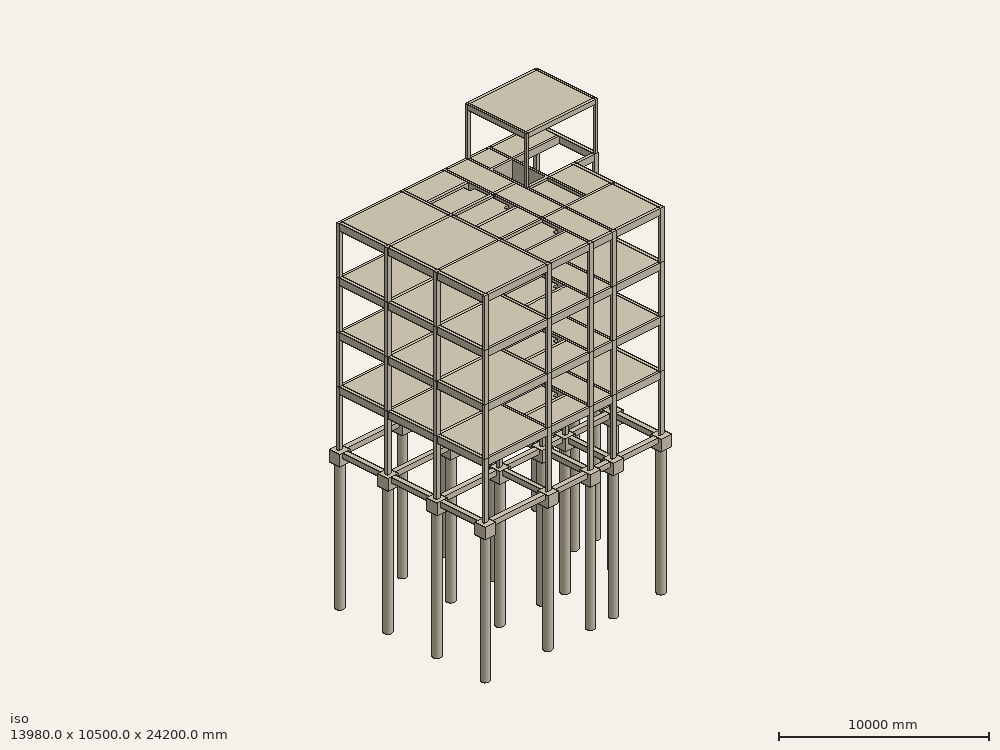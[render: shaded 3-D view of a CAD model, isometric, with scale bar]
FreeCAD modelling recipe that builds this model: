
FCSTD DOCUMENT  (FreeCAD 0.19R23074 (Git))
Label: 2020-12-18 Piloto estructural
License: All rights reserved
objects: Part::FeaturePython×393, Part::Part2DObjectPython×35, App::GeometryPython×28, App::FeaturePython×3, App::DocumentObjectGroup×2, TechDraw::DrawSVGTemplate×2, TechDraw::DrawViewArch×2, TechDraw::DrawPage×2, Spreadsheet::Sheet×1
note: 459 computed .brp shape members not serialized (recipe doc carries the construction recipe); baked Part::Feature solids carry a one-line shape summary decoded from their .brp

FEATURE [Part::FeaturePython] Axis  label="Vertical"  # WARN: FeaturePython — macro-defined, semantics opaque (R4)
  Angles = [0,0,0,0,0,0,0]
  Distances = [1930,4230,2850,1550,1450,1770,1430]
  Length = 12000
  Placement = pos=(0,-1350,0) rot=(0,0,1;0rad)
FEATURE [Part::FeaturePython] Axis002  label="HorizontaL"  # WARN: FeaturePython — macro-defined, semantics opaque (R4)
  Angles = [0,0,0,0,0,0]
  Distances = [100,3250,2620,670,1730,1530]
  Length = 32000
  Placement = pos=(31000,1.077e-12,0) rot=(0,0,1;1.5708rad)
FEATURE [App::DocumentObjectGroup] Group  label="Rejillas"
  Group = -> [Axis002,Axis]
FEATURE [TechDraw::DrawSVGTemplate] Template004
  Height = 841
  Orientation = 1
  Width = 1189
FEATURE [Part::Part2DObjectPython] Rectangle001  label="Lote"  # Draft 2D object (typed FeaturePython)
  Area = 0
  ChamferSize = 0
  Columns = 1
  FilletRadius = 0
  Height = 10000
  Length = 30000
  MakeFace = false
  Rows = 1
FEATURE [TechDraw::DrawSVGTemplate] Template005
  Height = 841
  Orientation = 1
  Width = 1189
FEATURE [Part::Part2DObjectPython] Rectangle002  # Draft 2D object (typed FeaturePython)
  Area = 0
  ChamferSize = 0
  Columns = 1
  FilletRadius = 0
  Height = 700
  Length = 700
  MakeFace = false
  Placement = pos=(14860,9550,0) rot=(0,0,1;0rad)
  Rows = 1
  expr: Height = <<Estructura>>.CabAncho
  expr: Length = <<Estructura>>.CabAncho
FEATURE [Part::Part2DObjectPython] Circle  # Draft 2D object (typed FeaturePython)
  Area = 0
  FirstAngle = 0
  LastAngle = 0
  MakeFace = false
  Placement = pos=(15210,9900,0) rot=(0,0,1;0rad)
  Radius = 250
  expr: Radius = <<Estructura>>.PilRad
FEATURE [Part::FeaturePython] Structure  label="CAB PIL 1"  # Arch/BIM 77 (typed FeaturePython)
  Base = -> Rectangle002
  Description = Pilote rectangular
  FaceMaker = 0
  Height = 700
  HorizontalArea = 490000
  IfcData = attributes={"GlobalId": {"name": "GlobalId", "type": "IfcGloballyUniqueId", "is_enum": false, "enum_values": []}, "Description": {"... (+532 chars omitted),+1 more (map truncated)
  IfcType = 77
  Length = 0
  MoveBase = false
  MoveWithHost = false
  Nodes = (2) [(15210,9900,0),(15210,9900,-700)]
  NodesOffset = 0
  Normal = (0,0,-1)
  PerimeterLength = 2800
  Placement = pos=(-13280,1.819e-12,-500) rot=(0,0,1;0rad)
  PredefinedType = 3
  VerticalArea = 1960000
  Width = 0
  expr: Height = <<Estructura>>.CabEsp
FEATURE [Part::FeaturePython] Structure001  label="PIL 1"  # Arch/BIM 96 (typed FeaturePython)
  Base = -> Circle
  ConstructionType = 0
  Description = Pilote circular
  FaceMaker = 0
  Height = 8000
  HorizontalArea = 196350
  IfcData = attributes={"GlobalId": {"name": "GlobalId", "type": "IfcGloballyUniqueId", "is_enum": false, "enum_values": []}, "Description": {"... (+752 chars omitted),+1 more (map truncated)
  IfcType = 96
  Length = 0
  MoveBase = false
  MoveWithHost = false
  Nodes = (2) [(15210,9900,0),(15210,9900,-8000)]
  NodesOffset = 0
  Normal = (0,0,-1)
  PerimeterLength = 1570.8
  Placement = pos=(-13280,1.819e-12,-1200) rot=(0,0,1;0rad)
  PredefinedType = 5
  VerticalArea = 1.25664e+07
  Width = 100
  expr: Height = <<Estructura>>.PilProf
FEATURE [Part::FeaturePython] Structure002  label="CAB PIL 6"  # Arch/BIM 172 (typed FeaturePython)
  CloneOf = -> Structure
  FaceMaker = 0
  Height = 700
  HorizontalArea = 490000
  IfcData = attributes={"GlobalId": {"name": "GlobalId", "type": "IfcGloballyUniqueId", "is_enum": false, "enum_values": []}, "Description": {"... (+484 chars omitted),+1 more (map truncated)
  IfcType = 172
  Length = 0
  MoveBase = false
  MoveWithHost = false
  Nodes = (2) [(15210,9900,0),(15210,9900,-700)]
  NodesOffset = 0
  Normal = (0,0,0)
  PerimeterLength = 2800
  Placement = pos=(-13280,-3260,-500) rot=(0,0,1;0rad)
  PredefinedType = 0
  VerticalArea = 1960000
  Width = 0
FEATURE [Part::FeaturePython] Structure003  label="PIL 6"  # Arch/BIM 172 (typed FeaturePython)
  CloneOf = -> Structure001
  FaceMaker = 0
  Height = 8000
  HorizontalArea = 196350
  IfcData = attributes={"GlobalId": {"name": "GlobalId", "type": "IfcGloballyUniqueId", "is_enum": false, "enum_values": []}, "Description": {"... (+484 chars omitted),+1 more (map truncated)
  IfcType = 172
  Length = 0
  MoveBase = false
  MoveWithHost = false
  Nodes = (2) [(15210,9900,0),(15210,9900,-8000)]
  NodesOffset = 0
  Normal = (0,0,0)
  PerimeterLength = 1570.8
  Placement = pos=(-13280,-3260,-1200) rot=(0,0,1;0rad)
  PredefinedType = 0
  VerticalArea = 1.25664e+07
  Width = 100
FEATURE [Part::FeaturePython] Structure004  label="CAB PIL 11"  # Arch/BIM 172 (typed FeaturePython)
  CloneOf = -> Structure
  FaceMaker = 0
  Height = 700
  HorizontalArea = 490000
  IfcData = attributes={"GlobalId": {"name": "GlobalId", "type": "IfcGloballyUniqueId", "is_enum": false, "enum_values": []}, "Description": {"... (+484 chars omitted),+1 more (map truncated)
  IfcType = 172
  Length = 0
  MoveBase = false
  MoveWithHost = false
  Nodes = (2) [(15210,9900,0),(15210,9900,-700)]
  NodesOffset = 0
  Normal = (0,0,0)
  PerimeterLength = 2800
  Placement = pos=(-13280,-6550,-500) rot=(0,0,1;0rad)
  PredefinedType = 0
  VerticalArea = 1960000
  Width = 0
FEATURE [Part::FeaturePython] Structure005  label="PIL 11"  # Arch/BIM 172 (typed FeaturePython)
  CloneOf = -> Structure001
  FaceMaker = 0
  Height = 8000
  HorizontalArea = 196350
  IfcData = attributes={"GlobalId": {"name": "GlobalId", "type": "IfcGloballyUniqueId", "is_enum": false, "enum_values": []}, "Description": {"... (+484 chars omitted),+1 more (map truncated)
  IfcType = 172
  Length = 0
  MoveBase = false
  MoveWithHost = false
  Nodes = (2) [(15210,9900,0),(15210,9900,-8000)]
  NodesOffset = 0
  Normal = (0,0,0)
  PerimeterLength = 1570.8
  Placement = pos=(-13280,-6550,-1200) rot=(0,0,1;0rad)
  PredefinedType = 0
  VerticalArea = 1.25664e+07
  Width = 100
FEATURE [Part::FeaturePython] Structure006  label="CAB PIL 2"  # Arch/BIM 172 (typed FeaturePython)
  CloneOf = -> Structure
  FaceMaker = 0
  Height = 700
  HorizontalArea = 490000
  IfcData = attributes={"GlobalId": {"name": "GlobalId", "type": "IfcGloballyUniqueId", "is_enum": false, "enum_values": []}, "Description": {"... (+484 chars omitted),+1 more (map truncated)
  IfcType = 172
  Length = 0
  MoveBase = false
  MoveWithHost = false
  Nodes = (2) [(15210,9900,0),(15210,9900,-700)]
  NodesOffset = 0
  Normal = (0,0,0)
  PerimeterLength = 2800
  Placement = pos=(-9050,0,-500) rot=(0,0,1;0rad)
  PredefinedType = 0
  VerticalArea = 1960000
  Width = 0
FEATURE [Part::FeaturePython] Structure007  label="PIL 2"  # Arch/BIM 172 (typed FeaturePython)
  CloneOf = -> Structure001
  FaceMaker = 0
  Height = 8000
  HorizontalArea = 196350
  IfcData = attributes={"GlobalId": {"name": "GlobalId", "type": "IfcGloballyUniqueId", "is_enum": false, "enum_values": []}, "Description": {"... (+484 chars omitted),+1 more (map truncated)
  IfcType = 172
  Length = 0
  MoveBase = false
  MoveWithHost = false
  Nodes = (2) [(15210,9900,0),(15210,9900,-8000)]
  NodesOffset = 0
  Normal = (0,0,0)
  PerimeterLength = 1570.8
  Placement = pos=(-9050,0,-1200) rot=(0,0,1;0rad)
  PredefinedType = 0
  VerticalArea = 1.25664e+07
  Width = 100
FEATURE [Part::FeaturePython] Structure008  label="CAB PIL 3"  # Arch/BIM 172 (typed FeaturePython)
  CloneOf = -> Structure
  FaceMaker = 0
  Height = 700
  HorizontalArea = 490000
  IfcData = attributes={"GlobalId": {"name": "GlobalId", "type": "IfcGloballyUniqueId", "is_enum": false, "enum_values": []}, "Description": {"... (+484 chars omitted),+1 more (map truncated)
  IfcType = 172
  Length = 0
  MoveBase = false
  MoveWithHost = false
  Nodes = (2) [(15210,9900,0),(15210,9900,-700)]
  NodesOffset = 0
  Normal = (0,0,0)
  PerimeterLength = 2800
  Placement = pos=(-6200,0,-500) rot=(0,0,1;0rad)
  PredefinedType = 0
  VerticalArea = 1960000
  Width = 0
FEATURE [Part::FeaturePython] Structure009  label="PIL 3"  # Arch/BIM 172 (typed FeaturePython)
  CloneOf = -> Structure001
  FaceMaker = 0
  Height = 8000
  HorizontalArea = 196350
  IfcData = attributes={"GlobalId": {"name": "GlobalId", "type": "IfcGloballyUniqueId", "is_enum": false, "enum_values": []}, "Description": {"... (+484 chars omitted),+1 more (map truncated)
  IfcType = 172
  Length = 0
  MoveBase = false
  MoveWithHost = false
  Nodes = (2) [(15210,9900,0),(15210,9900,-8000)]
  NodesOffset = 0
  Normal = (0,0,0)
  PerimeterLength = 1570.8
  Placement = pos=(-6200,0,-1200) rot=(0,0,1;0rad)
  PredefinedType = 0
  VerticalArea = 1.25664e+07
  Width = 100
FEATURE [Part::FeaturePython] Structure010  label="CAB PIL 4"  # Arch/BIM 172 (typed FeaturePython)
  CloneOf = -> Structure
  FaceMaker = 0
  Height = 700
  HorizontalArea = 490000
  IfcData = attributes={"GlobalId": {"name": "GlobalId", "type": "IfcGloballyUniqueId", "is_enum": false, "enum_values": []}, "Description": {"... (+484 chars omitted),+1 more (map truncated)
  IfcType = 172
  Length = 0
  MoveBase = false
  MoveWithHost = false
  Nodes = (2) [(15210,9900,0),(15210,9900,-700)]
  NodesOffset = 0
  Normal = (0,0,0)
  PerimeterLength = 2800
  Placement = pos=(-3200,0,-500) rot=(0,0,1;0rad)
  PredefinedType = 0
  VerticalArea = 1960000
  Width = 0
FEATURE [Part::FeaturePython] Structure011  label="PIL 4"  # Arch/BIM 172 (typed FeaturePython)
  CloneOf = -> Structure001
  FaceMaker = 0
  Height = 8000
  HorizontalArea = 196350
  IfcData = attributes={"GlobalId": {"name": "GlobalId", "type": "IfcGloballyUniqueId", "is_enum": false, "enum_values": []}, "Description": {"... (+484 chars omitted),+1 more (map truncated)
  IfcType = 172
  Length = 0
  MoveBase = false
  MoveWithHost = false
  Nodes = (2) [(15210,9900,0),(15210,9900,-8000)]
  NodesOffset = 0
  Normal = (0,0,0)
  PerimeterLength = 1570.8
  Placement = pos=(-3200,0,-1200) rot=(0,0,1;0rad)
  PredefinedType = 0
  VerticalArea = 1.25664e+07
  Width = 100
FEATURE [Part::FeaturePython] Structure012  label="CAB PIL 5"  # Arch/BIM 172 (typed FeaturePython)
  CloneOf = -> Structure
  FaceMaker = 0
  Height = 700
  HorizontalArea = 490000
  IfcData = attributes={"GlobalId": {"name": "GlobalId", "type": "IfcGloballyUniqueId", "is_enum": false, "enum_values": []}, "Description": {"... (+484 chars omitted),+1 more (map truncated)
  IfcType = 172
  Length = 0
  MoveBase = false
  MoveWithHost = false
  Nodes = (2) [(15210,9900,0),(15210,9900,-700)]
  NodesOffset = 0
  Normal = (0,0,0)
  PerimeterLength = 2800
  Placement = pos=(-9.09e-13,0,-500) rot=(0,0,1;0rad)
  PredefinedType = 0
  VerticalArea = 1960000
  Width = 0
FEATURE [Part::FeaturePython] Structure013  label="PIL 5"  # Arch/BIM 172 (typed FeaturePython)
  CloneOf = -> Structure001
  FaceMaker = 0
  Height = 8000
  HorizontalArea = 196350
  IfcData = attributes={"GlobalId": {"name": "GlobalId", "type": "IfcGloballyUniqueId", "is_enum": false, "enum_values": []}, "Description": {"... (+484 chars omitted),+1 more (map truncated)
  IfcType = 172
  Length = 0
  MoveBase = false
  MoveWithHost = false
  Nodes = (2) [(15210,9900,0),(15210,9900,-8000)]
  NodesOffset = 0
  Normal = (0,0,0)
  PerimeterLength = 1570.8
  Placement = pos=(-9.09e-13,0,-1200) rot=(0,0,1;0rad)
  PredefinedType = 0
  VerticalArea = 1.25664e+07
  Width = 100
FEATURE [Part::FeaturePython] Structure014  label="CAB PIL 7"  # Arch/BIM 172 (typed FeaturePython)
  CloneOf = -> Structure
  FaceMaker = 0
  Height = 700
  HorizontalArea = 490000
  IfcData = attributes={"GlobalId": {"name": "GlobalId", "type": "IfcGloballyUniqueId", "is_enum": false, "enum_values": []}, "Description": {"... (+484 chars omitted),+1 more (map truncated)
  IfcType = 172
  Length = 0
  MoveBase = false
  MoveWithHost = false
  Nodes = (2) [(15210,9900,0),(15210,9900,-700)]
  NodesOffset = 0
  Normal = (0,0,0)
  PerimeterLength = 2800
  Placement = pos=(-9050,-3260,-500) rot=(0,0,1;0rad)
  PredefinedType = 0
  VerticalArea = 1960000
  Width = 0
FEATURE [Part::FeaturePython] Structure015  label="PIL 7"  # Arch/BIM 172 (typed FeaturePython)
  CloneOf = -> Structure001
  FaceMaker = 0
  Height = 8000
  HorizontalArea = 196350
  IfcData = attributes={"GlobalId": {"name": "GlobalId", "type": "IfcGloballyUniqueId", "is_enum": false, "enum_values": []}, "Description": {"... (+484 chars omitted),+1 more (map truncated)
  IfcType = 172
  Length = 0
  MoveBase = false
  MoveWithHost = false
  Nodes = (2) [(15210,9900,0),(15210,9900,-8000)]
  NodesOffset = 0
  Normal = (0,0,0)
  PerimeterLength = 1570.8
  Placement = pos=(-9050,-3260,-1200) rot=(0,0,1;0rad)
  PredefinedType = 0
  VerticalArea = 1.25664e+07
  Width = 100
FEATURE [Part::FeaturePython] Structure016  label="CAB PIL 8"  # Arch/BIM 172 (typed FeaturePython)
  CloneOf = -> Structure
  FaceMaker = 0
  Height = 700
  HorizontalArea = 490000
  IfcData = attributes={"GlobalId": {"name": "GlobalId", "type": "IfcGloballyUniqueId", "is_enum": false, "enum_values": []}, "Description": {"... (+484 chars omitted),+1 more (map truncated)
  IfcType = 172
  Length = 0
  MoveBase = false
  MoveWithHost = false
  Nodes = (2) [(15210,9900,0),(15210,9900,-700)]
  NodesOffset = 0
  Normal = (0,0,0)
  PerimeterLength = 2800
  Placement = pos=(-6200,-3260,-500) rot=(0,0,1;0rad)
  PredefinedType = 0
  VerticalArea = 1960000
  Width = 0
FEATURE [Part::FeaturePython] Structure017  label="PIL 8"  # Arch/BIM 172 (typed FeaturePython)
  CloneOf = -> Structure001
  FaceMaker = 0
  Height = 8000
  HorizontalArea = 196350
  IfcData = attributes={"GlobalId": {"name": "GlobalId", "type": "IfcGloballyUniqueId", "is_enum": false, "enum_values": []}, "Description": {"... (+484 chars omitted),+1 more (map truncated)
  IfcType = 172
  Length = 0
  MoveBase = false
  MoveWithHost = false
  Nodes = (2) [(15210,9900,0),(15210,9900,-8000)]
  NodesOffset = 0
  Normal = (0,0,0)
  PerimeterLength = 1570.8
  Placement = pos=(-6200,-3260,-1200) rot=(0,0,1;0rad)
  PredefinedType = 0
  VerticalArea = 1.25664e+07
  Width = 100
FEATURE [Part::FeaturePython] Structure018  label="CAB PIL 9"  # Arch/BIM 172 (typed FeaturePython)
  CloneOf = -> Structure
  FaceMaker = 0
  Height = 700
  HorizontalArea = 490000
  IfcData = attributes={"GlobalId": {"name": "GlobalId", "type": "IfcGloballyUniqueId", "is_enum": false, "enum_values": []}, "Description": {"... (+484 chars omitted),+1 more (map truncated)
  IfcType = 172
  Length = 0
  MoveBase = false
  MoveWithHost = false
  Nodes = (2) [(15210,9900,0),(15210,9900,-700)]
  NodesOffset = 0
  Normal = (0,0,0)
  PerimeterLength = 2800
  Placement = pos=(-1430,-3930,-500) rot=(0,0,1;0rad)
  PredefinedType = 0
  VerticalArea = 1960000
  Width = 0
FEATURE [Part::FeaturePython] Structure019  label="PIL 9"  # Arch/BIM 172 (typed FeaturePython)
  CloneOf = -> Structure001
  FaceMaker = 0
  Height = 8000
  HorizontalArea = 196350
  IfcData = attributes={"GlobalId": {"name": "GlobalId", "type": "IfcGloballyUniqueId", "is_enum": false, "enum_values": []}, "Description": {"... (+484 chars omitted),+1 more (map truncated)
  IfcType = 172
  Length = 0
  MoveBase = false
  MoveWithHost = false
  Nodes = (2) [(15210,9900,0),(15210,9900,-8000)]
  NodesOffset = 0
  Normal = (0,0,0)
  PerimeterLength = 1570.8
  Placement = pos=(-1430,-3930,-1200) rot=(0,0,1;0rad)
  PredefinedType = 0
  VerticalArea = 1.25664e+07
  Width = 100
FEATURE [Part::FeaturePython] Structure020  label="CAB PIL 10"  # Arch/BIM 172 (typed FeaturePython)
  CloneOf = -> Structure
  FaceMaker = 0
  Height = 700
  HorizontalArea = 490000
  IfcData = attributes={"GlobalId": {"name": "GlobalId", "type": "IfcGloballyUniqueId", "is_enum": false, "enum_values": []}, "Description": {"... (+484 chars omitted),+1 more (map truncated)
  IfcType = 172
  Length = 0
  MoveBase = false
  MoveWithHost = false
  Nodes = (2) [(15210,9900,0),(15210,9900,-700)]
  NodesOffset = 0
  Normal = (0,0,0)
  PerimeterLength = 2800
  Placement = pos=(-9.09e-13,-3930,-500) rot=(0,0,1;0rad)
  PredefinedType = 0
  VerticalArea = 1960000
  Width = 0
FEATURE [Part::FeaturePython] Structure021  label="PIL 10"  # Arch/BIM 172 (typed FeaturePython)
  CloneOf = -> Structure001
  FaceMaker = 0
  Height = 8000
  HorizontalArea = 196350
  IfcData = attributes={"GlobalId": {"name": "GlobalId", "type": "IfcGloballyUniqueId", "is_enum": false, "enum_values": []}, "Description": {"... (+484 chars omitted),+1 more (map truncated)
  IfcType = 172
  Length = 0
  MoveBase = false
  MoveWithHost = false
  Nodes = (2) [(15210,9900,0),(15210,9900,-8000)]
  NodesOffset = 0
  Normal = (0,0,0)
  PerimeterLength = 1570.8
  Placement = pos=(-9.09e-13,-3930,-1200) rot=(0,0,1;0rad)
  PredefinedType = 0
  VerticalArea = 1.25664e+07
  Width = 100
FEATURE [Part::FeaturePython] Structure022  label="CAB PIL 12"  # Arch/BIM 172 (typed FeaturePython)
  CloneOf = -> Structure
  FaceMaker = 0
  Height = 700
  HorizontalArea = 490000
  IfcData = attributes={"GlobalId": {"name": "GlobalId", "type": "IfcGloballyUniqueId", "is_enum": false, "enum_values": []}, "Description": {"... (+484 chars omitted),+1 more (map truncated)
  IfcType = 172
  Length = 0
  MoveBase = false
  MoveWithHost = false
  Nodes = (2) [(15210,9900,0),(15210,9900,-700)]
  NodesOffset = 0
  Normal = (0,0,0)
  PerimeterLength = 2800
  Placement = pos=(-9050,-6550,-500) rot=(0,0,1;0rad)
  PredefinedType = 0
  VerticalArea = 1960000
  Width = 0
FEATURE [Part::FeaturePython] Structure023  label="PIL 12"  # Arch/BIM 172 (typed FeaturePython)
  CloneOf = -> Structure001
  FaceMaker = 0
  Height = 8000
  HorizontalArea = 196350
  IfcData = attributes={"GlobalId": {"name": "GlobalId", "type": "IfcGloballyUniqueId", "is_enum": false, "enum_values": []}, "Description": {"... (+484 chars omitted),+1 more (map truncated)
  IfcType = 172
  Length = 0
  MoveBase = false
  MoveWithHost = false
  Nodes = (2) [(15210,9900,0),(15210,9900,-8000)]
  NodesOffset = 0
  Normal = (0,0,0)
  PerimeterLength = 1570.8
  Placement = pos=(-9050,-6550,-1200) rot=(0,0,1;0rad)
  PredefinedType = 0
  VerticalArea = 1.25664e+07
  Width = 100
FEATURE [Part::FeaturePython] Structure024  label="CAB PIL 13"  # Arch/BIM 172 (typed FeaturePython)
  CloneOf = -> Structure
  FaceMaker = 0
  Height = 700
  HorizontalArea = 490000
  IfcData = attributes={"GlobalId": {"name": "GlobalId", "type": "IfcGloballyUniqueId", "is_enum": false, "enum_values": []}, "Description": {"... (+484 chars omitted),+1 more (map truncated)
  IfcType = 172
  Length = 0
  MoveBase = false
  MoveWithHost = false
  Nodes = (2) [(15210,9900,0),(15210,9900,-700)]
  NodesOffset = 0
  Normal = (0,0,0)
  PerimeterLength = 2800
  Placement = pos=(-6200,-6550,-500) rot=(0,0,1;0rad)
  PredefinedType = 0
  VerticalArea = 1960000
  Width = 0
FEATURE [Part::FeaturePython] Structure025  label="PIL 13"  # Arch/BIM 172 (typed FeaturePython)
  CloneOf = -> Structure001
  FaceMaker = 0
  Height = 8000
  HorizontalArea = 196350
  IfcData = attributes={"GlobalId": {"name": "GlobalId", "type": "IfcGloballyUniqueId", "is_enum": false, "enum_values": []}, "Description": {"... (+484 chars omitted),+1 more (map truncated)
  IfcType = 172
  Length = 0
  MoveBase = false
  MoveWithHost = false
  Nodes = (2) [(15210,9900,0),(15210,9900,-8000)]
  NodesOffset = 0
  Normal = (0,0,0)
  PerimeterLength = 1570.8
  Placement = pos=(-6200,-6550,-1200) rot=(0,0,1;0rad)
  PredefinedType = 0
  VerticalArea = 1.25664e+07
  Width = 100
FEATURE [Part::FeaturePython] Structure026  label="CAB PIL 14"  # Arch/BIM 172 (typed FeaturePython)
  CloneOf = -> Structure
  FaceMaker = 0
  Height = 700
  HorizontalArea = 490000
  IfcData = attributes={"GlobalId": {"name": "GlobalId", "type": "IfcGloballyUniqueId", "is_enum": false, "enum_values": []}, "Description": {"... (+484 chars omitted),+1 more (map truncated)
  IfcType = 172
  Length = 0
  MoveBase = false
  MoveWithHost = false
  Nodes = (2) [(15210,9900,0),(15210,9900,-700)]
  NodesOffset = 0
  Normal = (0,0,0)
  PerimeterLength = 2800
  Placement = pos=(-4650,-6550,-500) rot=(0,0,1;0rad)
  PredefinedType = 0
  VerticalArea = 1960000
  Width = 0
FEATURE [Part::FeaturePython] Structure027  label="PIL 14"  # Arch/BIM 172 (typed FeaturePython)
  CloneOf = -> Structure001
  FaceMaker = 0
  Height = 8000
  HorizontalArea = 196350
  IfcData = attributes={"GlobalId": {"name": "GlobalId", "type": "IfcGloballyUniqueId", "is_enum": false, "enum_values": []}, "Description": {"... (+484 chars omitted),+1 more (map truncated)
  IfcType = 172
  Length = 0
  MoveBase = false
  MoveWithHost = false
  Nodes = (2) [(15210,9900,0),(15210,9900,-8000)]
  NodesOffset = 0
  Normal = (0,0,0)
  PerimeterLength = 1570.8
  Placement = pos=(-4650,-6550,-1200) rot=(0,0,1;0rad)
  PredefinedType = 0
  VerticalArea = 1.25664e+07
  Width = 100
FEATURE [Part::FeaturePython] Structure028  label="PIL 15"  # Arch/BIM 172 (typed FeaturePython)
  CloneOf = -> Structure001
  FaceMaker = 0
  Height = 8000
  HorizontalArea = 196350
  IfcData = attributes={"GlobalId": {"name": "GlobalId", "type": "IfcGloballyUniqueId", "is_enum": false, "enum_values": []}, "Description": {"... (+484 chars omitted),+1 more (map truncated)
  IfcType = 172
  Length = 0
  MoveBase = false
  MoveWithHost = false
  Nodes = (2) [(15210,9900,0),(15210,9900,-8000)]
  NodesOffset = 0
  Normal = (0,0,0)
  PerimeterLength = 1570.8
  Placement = pos=(-1430,-6550,-1200) rot=(0,0,1;0rad)
  PredefinedType = 0
  VerticalArea = 1.25664e+07
  Width = 100
FEATURE [Part::FeaturePython] Structure029  label="CAB PIL 15"  # Arch/BIM 172 (typed FeaturePython)
  CloneOf = -> Structure
  FaceMaker = 0
  Height = 700
  HorizontalArea = 490000
  IfcData = attributes={"GlobalId": {"name": "GlobalId", "type": "IfcGloballyUniqueId", "is_enum": false, "enum_values": []}, "Description": {"... (+484 chars omitted),+1 more (map truncated)
  IfcType = 172
  Length = 0
  MoveBase = false
  MoveWithHost = false
  Nodes = (2) [(15210,9900,0),(15210,9900,-700)]
  NodesOffset = 0
  Normal = (0,0,0)
  PerimeterLength = 2800
  Placement = pos=(-1430,-6550,-500) rot=(0,0,1;0rad)
  PredefinedType = 0
  VerticalArea = 1960000
  Width = 0
FEATURE [Part::FeaturePython] Structure030  label="CAB PIL 16"  # Arch/BIM 172 (typed FeaturePython)
  CloneOf = -> Structure
  FaceMaker = 0
  Height = 700
  HorizontalArea = 490000
  IfcData = attributes={"GlobalId": {"name": "GlobalId", "type": "IfcGloballyUniqueId", "is_enum": false, "enum_values": []}, "Description": {"... (+484 chars omitted),+1 more (map truncated)
  IfcType = 172
  Length = 0
  MoveBase = false
  MoveWithHost = false
  Nodes = (2) [(15210,9900,0),(15210,9900,-700)]
  NodesOffset = 0
  Normal = (0,0,0)
  PerimeterLength = 2800
  Placement = pos=(-13280,-9800,-500) rot=(0,0,1;0rad)
  PredefinedType = 0
  VerticalArea = 1960000
  Width = 0
FEATURE [Part::FeaturePython] Structure031  label="PIL 16"  # Arch/BIM 172 (typed FeaturePython)
  CloneOf = -> Structure001
  FaceMaker = 0
  Height = 8000
  HorizontalArea = 196350
  IfcData = attributes={"GlobalId": {"name": "GlobalId", "type": "IfcGloballyUniqueId", "is_enum": false, "enum_values": []}, "Description": {"... (+484 chars omitted),+1 more (map truncated)
  IfcType = 172
  Length = 0
  MoveBase = false
  MoveWithHost = false
  Nodes = (2) [(15210,9900,0),(15210,9900,-8000)]
  NodesOffset = 0
  Normal = (0,0,0)
  PerimeterLength = 1570.8
  Placement = pos=(-13280,-9800,-1200) rot=(0,0,1;0rad)
  PredefinedType = 0
  VerticalArea = 1.25664e+07
  Width = 100
FEATURE [Part::FeaturePython] Structure032  label="CAB PIL 17"  # Arch/BIM 172 (typed FeaturePython)
  CloneOf = -> Structure
  FaceMaker = 0
  Height = 700
  HorizontalArea = 490000
  IfcData = attributes={"GlobalId": {"name": "GlobalId", "type": "IfcGloballyUniqueId", "is_enum": false, "enum_values": []}, "Description": {"... (+484 chars omitted),+1 more (map truncated)
  IfcType = 172
  Length = 0
  MoveBase = false
  MoveWithHost = false
  Nodes = (2) [(15210,9900,0),(15210,9900,-700)]
  NodesOffset = 0
  Normal = (0,0,0)
  PerimeterLength = 2800
  Placement = pos=(-9050,-9800,-500) rot=(0,0,1;0rad)
  PredefinedType = 0
  VerticalArea = 1960000
  Width = 0
FEATURE [Part::FeaturePython] Structure033  label="PIL 17"  # Arch/BIM 172 (typed FeaturePython)
  CloneOf = -> Structure001
  FaceMaker = 0
  Height = 8000
  HorizontalArea = 196350
  IfcData = attributes={"GlobalId": {"name": "GlobalId", "type": "IfcGloballyUniqueId", "is_enum": false, "enum_values": []}, "Description": {"... (+484 chars omitted),+1 more (map truncated)
  IfcType = 172
  Length = 0
  MoveBase = false
  MoveWithHost = false
  Nodes = (2) [(15210,9900,0),(15210,9900,-8000)]
  NodesOffset = 0
  Normal = (0,0,0)
  PerimeterLength = 1570.8
  Placement = pos=(-9050,-9800,-1200) rot=(0,0,1;0rad)
  PredefinedType = 0
  VerticalArea = 1.25664e+07
  Width = 100
FEATURE [Part::FeaturePython] Structure034  label="CAB PIL 18"  # Arch/BIM 172 (typed FeaturePython)
  CloneOf = -> Structure
  FaceMaker = 0
  Height = 700
  HorizontalArea = 490000
  IfcData = attributes={"GlobalId": {"name": "GlobalId", "type": "IfcGloballyUniqueId", "is_enum": false, "enum_values": []}, "Description": {"... (+484 chars omitted),+1 more (map truncated)
  IfcType = 172
  Length = 0
  MoveBase = false
  MoveWithHost = false
  Nodes = (2) [(15210,9900,0),(15210,9900,-700)]
  NodesOffset = 0
  Normal = (0,0,0)
  PerimeterLength = 2800
  Placement = pos=(-6200,-9800,-500) rot=(0,0,1;0rad)
  PredefinedType = 0
  VerticalArea = 1960000
  Width = 0
FEATURE [Part::FeaturePython] Structure035  label="PIL 18"  # Arch/BIM 172 (typed FeaturePython)
  CloneOf = -> Structure001
  FaceMaker = 0
  Height = 8000
  HorizontalArea = 196350
  IfcData = attributes={"GlobalId": {"name": "GlobalId", "type": "IfcGloballyUniqueId", "is_enum": false, "enum_values": []}, "Description": {"... (+484 chars omitted),+1 more (map truncated)
  IfcType = 172
  Length = 0
  MoveBase = false
  MoveWithHost = false
  Nodes = (2) [(15210,9900,0),(15210,9900,-8000)]
  NodesOffset = 0
  Normal = (0,0,0)
  PerimeterLength = 1570.8
  Placement = pos=(-6200,-9800,-1200) rot=(0,0,1;0rad)
  PredefinedType = 0
  VerticalArea = 1.25664e+07
  Width = 100
FEATURE [Part::FeaturePython] Structure036  label="CAB PIL 19"  # Arch/BIM 172 (typed FeaturePython)
  CloneOf = -> Structure
  FaceMaker = 0
  Height = 700
  HorizontalArea = 490000
  IfcData = attributes={"GlobalId": {"name": "GlobalId", "type": "IfcGloballyUniqueId", "is_enum": false, "enum_values": []}, "Description": {"... (+484 chars omitted),+1 more (map truncated)
  IfcType = 172
  Length = 0
  MoveBase = false
  MoveWithHost = false
  Nodes = (2) [(15210,9900,0),(15210,9900,-700)]
  NodesOffset = 0
  Normal = (0,0,0)
  PerimeterLength = 2800
  Placement = pos=(-4650,-9800,-500) rot=(0,0,1;0rad)
  PredefinedType = 0
  VerticalArea = 1960000
  Width = 0
FEATURE [Part::FeaturePython] Structure037  label="PIL 19"  # Arch/BIM 172 (typed FeaturePython)
  CloneOf = -> Structure001
  FaceMaker = 0
  Height = 8000
  HorizontalArea = 196350
  IfcData = attributes={"GlobalId": {"name": "GlobalId", "type": "IfcGloballyUniqueId", "is_enum": false, "enum_values": []}, "Description": {"... (+484 chars omitted),+1 more (map truncated)
  IfcType = 172
  Length = 0
  MoveBase = false
  MoveWithHost = false
  Nodes = (2) [(15210,9900,0),(15210,9900,-8000)]
  NodesOffset = 0
  Normal = (0,0,0)
  PerimeterLength = 1570.8
  Placement = pos=(-4650,-9800,-1200) rot=(0,0,1;0rad)
  PredefinedType = 0
  VerticalArea = 1.25664e+07
  Width = 100
FEATURE [Part::FeaturePython] Structure038  label="CAB PIL 20"  # Arch/BIM 172 (typed FeaturePython)
  CloneOf = -> Structure
  FaceMaker = 0
  Height = 700
  HorizontalArea = 490000
  IfcData = attributes={"GlobalId": {"name": "GlobalId", "type": "IfcGloballyUniqueId", "is_enum": false, "enum_values": []}, "Description": {"... (+484 chars omitted),+1 more (map truncated)
  IfcType = 172
  Length = 0
  MoveBase = false
  MoveWithHost = false
  Nodes = (2) [(15210,9900,0),(15210,9900,-700)]
  NodesOffset = 0
  Normal = (0,0,0)
  PerimeterLength = 2800
  Placement = pos=(-1430,-9800,-500) rot=(0,0,1;0rad)
  PredefinedType = 0
  VerticalArea = 1960000
  Width = 0
FEATURE [Part::FeaturePython] Structure039  label="PIL 20"  # Arch/BIM 172 (typed FeaturePython)
  CloneOf = -> Structure001
  FaceMaker = 0
  Height = 8000
  HorizontalArea = 196350
  IfcData = attributes={"GlobalId": {"name": "GlobalId", "type": "IfcGloballyUniqueId", "is_enum": false, "enum_values": []}, "Description": {"... (+484 chars omitted),+1 more (map truncated)
  IfcType = 172
  Length = 0
  MoveBase = false
  MoveWithHost = false
  Nodes = (2) [(15210,9900,0),(15210,9900,-8000)]
  NodesOffset = 0
  Normal = (0,0,0)
  PerimeterLength = 1570.8
  Placement = pos=(-1430,-9800,-1200) rot=(0,0,1;0rad)
  PredefinedType = 0
  VerticalArea = 1.25664e+07
  Width = 100
FEATURE [Part::FeaturePython] Structure040  label="L01"  # Arch/BIM 172 (typed FeaturePython)
  FaceMaker = 0
  Height = 250
  HorizontalArea = 9230000
  IfcData = attributes={"GlobalId": {"name": "GlobalId", "type": "IfcGloballyUniqueId", "is_enum": false, "enum_values": []}, "Description": {"... (+484 chars omitted),+1 more (map truncated)
  IfcType = 172
  Length = 0
  MoveBase = false
  MoveWithHost = false
  Nodes = (2) [(18300,6875,0),(18300,6875,-250)]
  NodesOffset = 0
  Normal = (0,0,-1)
  PerimeterLength = 12300
  Placement = pos=(-7015,295,-1000) rot=(0,0,1;0rad)
  PredefinedType = 0
  VerticalArea = 3075000
  Width = 100
FEATURE [Part::FeaturePython] Beam001  # Arch/BIM 7 (typed FeaturePython)
  Chamfer = 0
  DentHeight = 0
  DentLength = 0
  Height = 300
  HorizontalArea = 1059000
  IfcData = attributes={"GlobalId": {"name": "GlobalId", "type": "IfcGloballyUniqueId", "is_enum": false, "enum_values": []}, "Description": {"... (+475 chars omitted),+1 more (map truncated)
  IfcType = 7
  Length = 3530
  MoveBase = false
  MoveWithHost = false
  PerimeterLength = 7660
  Placement = pos=(2280,6490,-800) rot=(0,0,1;0rad)
  PredefinedType = 0
  VerticalArea = 2298000
  Width = 300
FEATURE [Part::FeaturePython] Structure041  label="Beam002"  # Arch/BIM 7 (typed FeaturePython)
  FaceMaker = 0
  Height = 300
  HorizontalArea = 768000
  IfcData = attributes={"GlobalId": {"name": "GlobalId", "type": "IfcGloballyUniqueId", "is_enum": false, "enum_values": []}, "Description": {"... (+475 chars omitted),+1 more (map truncated)
  IfcType = 7
  Length = 2560
  MoveBase = false
  MoveWithHost = false
  Nodes = (2) [(1.2326e-31,-1.51582e-15,5.55112e-16),(2560,-1.51582e-15,5.55112e-16)]
  NodesOffset = 0
  Normal = (0,0,0)
  PerimeterLength = 5720
  Placement = pos=(1930,9550,-650) rot=(0,0,-1;1.5708rad)
  PredefinedType = 0
  VerticalArea = 1.716e+06
  Width = 300
  expr: Height = <<Estructura>>.VRAlto
  expr: Width = <<Estructura>>.VRAncho
FEATURE [Part::FeaturePython] Structure042  label="Beam003"  # Arch/BIM 7 (typed FeaturePython)
  FaceMaker = 0
  Height = 300
  HorizontalArea = 777000
  IfcData = attributes={"GlobalId": {"name": "GlobalId", "type": "IfcGloballyUniqueId", "is_enum": false, "enum_values": []}, "Description": {"... (+475 chars omitted),+1 more (map truncated)
  IfcType = 7
  Length = 2590
  MoveBase = false
  MoveWithHost = false
  Nodes = (2) [(1.2326e-31,-1.51582e-15,5.55112e-16),(2590,-1.51582e-15,5.55112e-16)]
  NodesOffset = 0
  Normal = (0,0,0)
  PerimeterLength = 5780
  Placement = pos=(1930,6290,-650) rot=(0,0,-1;1.5708rad)
  PredefinedType = 0
  VerticalArea = 1.734e+06
  Width = 300
FEATURE [Part::FeaturePython] Structure043  label="Beam004"  # Arch/BIM 7 (typed FeaturePython)
  FaceMaker = 0
  Height = 300
  HorizontalArea = 765000
  IfcData = attributes={"GlobalId": {"name": "GlobalId", "type": "IfcGloballyUniqueId", "is_enum": false, "enum_values": []}, "Description": {"... (+475 chars omitted),+1 more (map truncated)
  IfcType = 7
  Length = 2550
  MoveBase = false
  MoveWithHost = false
  Nodes = (2) [(1.2326e-31,-1.51582e-15,5.55112e-16),(2550,-1.51582e-15,5.55112e-16)]
  NodesOffset = 0
  Normal = (0,0,0)
  PerimeterLength = 5700
  Placement = pos=(1930,3000,-650) rot=(0,0,-1;1.5708rad)
  PredefinedType = 0
  VerticalArea = 1.71e+06
  Width = 300
FEATURE [Part::FeaturePython] Structure044  label="Beam005"  # Arch/BIM 7 (typed FeaturePython)
  FaceMaker = 0
  Height = 300
  HorizontalArea = 768000
  IfcData = attributes={"GlobalId": {"name": "GlobalId", "type": "IfcGloballyUniqueId", "is_enum": false, "enum_values": []}, "Description": {"... (+475 chars omitted),+1 more (map truncated)
  IfcType = 7
  Length = 2560
  MoveBase = false
  MoveWithHost = false
  Nodes = (2) [(1.2326e-31,-1.51582e-15,5.55112e-16),(2560,-1.51582e-15,5.55112e-16)]
  NodesOffset = 0
  Normal = (0,0,0)
  PerimeterLength = 5720
  Placement = pos=(6160.36,9550,-650) rot=(0,0,-1;1.5708rad)
  PredefinedType = 0
  VerticalArea = 1.716e+06
  Width = 300
FEATURE [Part::FeaturePython] Structure045  label="Beam006"  # Arch/BIM 7 (typed FeaturePython)
  FaceMaker = 0
  Height = 300
  HorizontalArea = 777000
  IfcData = attributes={"GlobalId": {"name": "GlobalId", "type": "IfcGloballyUniqueId", "is_enum": false, "enum_values": []}, "Description": {"... (+475 chars omitted),+1 more (map truncated)
  IfcType = 7
  Length = 2590
  MoveBase = false
  MoveWithHost = false
  Nodes = (2) [(1.2326e-31,-1.51582e-15,5.55112e-16),(2590,-1.51582e-15,5.55112e-16)]
  NodesOffset = 0
  Normal = (0,0,0)
  PerimeterLength = 5780
  Placement = pos=(6160.36,6290,-650) rot=(0,0,-1;1.5708rad)
  PredefinedType = 0
  VerticalArea = 1.734e+06
  Width = 300
FEATURE [Part::FeaturePython] Structure046  label="Beam007"  # Arch/BIM 7 (typed FeaturePython)
  FaceMaker = 0
  Height = 300
  HorizontalArea = 765000
  IfcData = attributes={"GlobalId": {"name": "GlobalId", "type": "IfcGloballyUniqueId", "is_enum": false, "enum_values": []}, "Description": {"... (+475 chars omitted),+1 more (map truncated)
  IfcType = 7
  Length = 2550
  MoveBase = false
  MoveWithHost = false
  Nodes = (2) [(1.2326e-31,-1.51582e-15,5.55112e-16),(2550,-1.51582e-15,5.55112e-16)]
  NodesOffset = 0
  Normal = (0,0,0)
  PerimeterLength = 5700
  Placement = pos=(6160.36,3000,-650) rot=(0,0,-1;1.5708rad)
  PredefinedType = 0
  VerticalArea = 1.71e+06
  Width = 300
FEATURE [Part::FeaturePython] Structure048  label="Beam009"  # Arch/BIM 7 (typed FeaturePython)
  FaceMaker = 0
  Height = 300
  HorizontalArea = 777000
  IfcData = attributes={"GlobalId": {"name": "GlobalId", "type": "IfcGloballyUniqueId", "is_enum": false, "enum_values": []}, "Description": {"... (+475 chars omitted),+1 more (map truncated)
  IfcType = 7
  Length = 2590
  MoveBase = false
  MoveWithHost = false
  Nodes = (2) [(1.2326e-31,-1.51582e-15,5.55112e-16),(2590,-1.51582e-15,5.55112e-16)]
  NodesOffset = 0
  Normal = (0,0,0)
  PerimeterLength = 5780
  Placement = pos=(9010.18,6290,-650) rot=(0,0,-1;1.5708rad)
  PredefinedType = 0
  VerticalArea = 1.734e+06
  Width = 300
FEATURE [Part::FeaturePython] Structure049  label="Beam010"  # Arch/BIM 7 (typed FeaturePython)
  FaceMaker = 0
  Height = 300
  HorizontalArea = 765000
  IfcData = attributes={"GlobalId": {"name": "GlobalId", "type": "IfcGloballyUniqueId", "is_enum": false, "enum_values": []}, "Description": {"... (+475 chars omitted),+1 more (map truncated)
  IfcType = 7
  Length = 2550
  MoveBase = false
  MoveWithHost = false
  Nodes = (2) [(1.2326e-31,-1.51582e-15,5.55112e-16),(2550,-1.51582e-15,5.55112e-16)]
  NodesOffset = 0
  Normal = (0,0,0)
  PerimeterLength = 5700
  Placement = pos=(9010.18,3000,-650) rot=(0,0,-1;1.5708rad)
  PredefinedType = 0
  VerticalArea = 1.71e+06
  Width = 300
FEATURE [Part::FeaturePython] Structure053  label="Beam014"  # Arch/BIM 7 (typed FeaturePython)
  FaceMaker = 0
  Height = 300
  HorizontalArea = 765000
  IfcData = attributes={"GlobalId": {"name": "GlobalId", "type": "IfcGloballyUniqueId", "is_enum": false, "enum_values": []}, "Description": {"... (+475 chars omitted),+1 more (map truncated)
  IfcType = 7
  Length = 2550
  MoveBase = false
  MoveWithHost = false
  Nodes = (2) [(1.2326e-31,-1.51582e-15,5.55112e-16),(2550,-1.51582e-15,5.55112e-16)]
  NodesOffset = 0
  Normal = (0,0,0)
  PerimeterLength = 5700
  Placement = pos=(13778.3,3000,-650) rot=(0,0,-1;1.5708rad)
  PredefinedType = 0
  VerticalArea = 1.71e+06
  Width = 300
FEATURE [Part::FeaturePython] Structure056  label="Beam017"  # Arch/BIM 7 (typed FeaturePython)
  FaceMaker = 0
  Height = 300
  HorizontalArea = 765000
  IfcData = attributes={"GlobalId": {"name": "GlobalId", "type": "IfcGloballyUniqueId", "is_enum": false, "enum_values": []}, "Description": {"... (+475 chars omitted),+1 more (map truncated)
  IfcType = 7
  Length = 2550
  MoveBase = false
  MoveWithHost = false
  Nodes = (2) [(1.2326e-31,-1.51582e-15,5.55112e-16),(2550,-1.51582e-15,5.55112e-16)]
  NodesOffset = 0
  Normal = (0,0,0)
  PerimeterLength = 5700
  Placement = pos=(10560,3000,-650) rot=(0,0,-1;1.5708rad)
  PredefinedType = 0
  VerticalArea = 1.71e+06
  Width = 300
FEATURE [Part::FeaturePython] Structure059  label="Beam020"  # Arch/BIM 7 (typed FeaturePython)
  FaceMaker = 0
  Height = 300
  HorizontalArea = 645000
  IfcData = attributes={"GlobalId": {"name": "GlobalId", "type": "IfcGloballyUniqueId", "is_enum": false, "enum_values": []}, "Description": {"... (+475 chars omitted),+1 more (map truncated)
  IfcType = 7
  Length = 2150
  MoveBase = false
  MoveWithHost = false
  Nodes = (2) [(1.2326e-31,-1.51582e-15,5.55112e-16),(2150,-1.51582e-15,5.55112e-16)]
  NodesOffset = 0
  Normal = (0,0,0)
  PerimeterLength = 4900
  Placement = pos=(6510,9900,-650) rot=(0,0,1;0rad)
  PredefinedType = 0
  VerticalArea = 1.47e+06
  Width = 300
FEATURE [Part::FeaturePython] Structure060  label="Beam021"  # Arch/BIM 7 (typed FeaturePython)
  FaceMaker = 0
  Height = 300
  HorizontalArea = 690000
  IfcData = attributes={"GlobalId": {"name": "GlobalId", "type": "IfcGloballyUniqueId", "is_enum": false, "enum_values": []}, "Description": {"... (+475 chars omitted),+1 more (map truncated)
  IfcType = 7
  Length = 2300
  MoveBase = false
  MoveWithHost = false
  Nodes = (2) [(1.2326e-31,-1.51582e-15,5.55112e-16),(2300,-1.51582e-15,5.55112e-16)]
  NodesOffset = 0
  Normal = (0,0,0)
  PerimeterLength = 5200
  Placement = pos=(9360,9900,-650) rot=(0,0,1;0rad)
  PredefinedType = 0
  VerticalArea = 1.56e+06
  Width = 300
FEATURE [Part::FeaturePython] Structure061  label="Beam022"  # Arch/BIM 7 (typed FeaturePython)
  FaceMaker = 0
  Height = 300
  HorizontalArea = 750000
  IfcData = attributes={"GlobalId": {"name": "GlobalId", "type": "IfcGloballyUniqueId", "is_enum": false, "enum_values": []}, "Description": {"... (+475 chars omitted),+1 more (map truncated)
  IfcType = 7
  Length = 2500
  MoveBase = false
  MoveWithHost = false
  Nodes = (2) [(1.2326e-31,-1.51582e-15,5.55112e-16),(2500,-1.51582e-15,5.55112e-16)]
  NodesOffset = 0
  Normal = (0,0,0)
  PerimeterLength = 5600
  Placement = pos=(12360,9900,-650) rot=(0,0,1;0rad)
  PredefinedType = 0
  VerticalArea = 1680000
  Width = 300
FEATURE [Part::FeaturePython] Structure064  label="Beam025"  # Arch/BIM 7 (typed FeaturePython)
  FaceMaker = 0
  Height = 300
  HorizontalArea = 645000
  IfcData = attributes={"GlobalId": {"name": "GlobalId", "type": "IfcGloballyUniqueId", "is_enum": false, "enum_values": []}, "Description": {"... (+475 chars omitted),+1 more (map truncated)
  IfcType = 7
  Length = 2150
  MoveBase = false
  MoveWithHost = false
  Nodes = (2) [(1.2326e-31,-1.51582e-15,5.55112e-16),(2150,-1.51582e-15,5.55112e-16)]
  NodesOffset = 0
  Normal = (0,0,0)
  PerimeterLength = 4900
  Placement = pos=(6510,6640,-650) rot=(0,0,1;0rad)
  PredefinedType = 0
  VerticalArea = 1.47e+06
  Width = 300
FEATURE [Part::FeaturePython] Structure065  label="Beam026"  # Arch/BIM 7 (typed FeaturePython)
  FaceMaker = 0
  Height = 300
  HorizontalArea = 768000
  IfcData = attributes={"GlobalId": {"name": "GlobalId", "type": "IfcGloballyUniqueId", "is_enum": false, "enum_values": []}, "Description": {"... (+475 chars omitted),+1 more (map truncated)
  IfcType = 7
  Length = 2560
  MoveBase = false
  MoveWithHost = false
  Nodes = (2) [(1.2326e-31,-1.51582e-15,5.55112e-16),(2560,-1.51582e-15,5.55112e-16)]
  NodesOffset = 0
  Normal = (0,0,0)
  PerimeterLength = 5720
  Placement = pos=(9010,6990,-650) rot=(0,0,1;1.5708rad)
  PredefinedType = 0
  VerticalArea = 1.716e+06
  Width = 300
FEATURE [Part::FeaturePython] Structure066  label="Beam027"  # Arch/BIM 7 (typed FeaturePython)
  FaceMaker = 0
  Height = 300
  HorizontalArea = 1.059e+06
  IfcData = attributes={"GlobalId": {"name": "GlobalId", "type": "IfcGloballyUniqueId", "is_enum": false, "enum_values": []}, "Description": {"... (+475 chars omitted),+1 more (map truncated)
  IfcType = 7
  Length = 3530
  MoveBase = false
  MoveWithHost = false
  Nodes = (2) [(1.2326e-31,-1.51582e-15,5.55112e-16),(3530,-1.51582e-15,5.55112e-16)]
  NodesOffset = 0
  Normal = (0,0,0)
  PerimeterLength = 7660
  Placement = pos=(2280,3350,-650) rot=(0,0,1;0rad)
  PredefinedType = 0
  VerticalArea = 2.298e+06
  Width = 300
FEATURE [Part::FeaturePython] Structure067  label="Beam028"  # Arch/BIM 7 (typed FeaturePython)
  FaceMaker = 0
  Height = 300
  HorizontalArea = 645000
  IfcData = attributes={"GlobalId": {"name": "GlobalId", "type": "IfcGloballyUniqueId", "is_enum": false, "enum_values": []}, "Description": {"... (+475 chars omitted),+1 more (map truncated)
  IfcType = 7
  Length = 2150
  MoveBase = false
  MoveWithHost = false
  Nodes = (2) [(1.2326e-31,-1.51582e-15,5.55112e-16),(2150,-1.51582e-15,5.55112e-16)]
  NodesOffset = 0
  Normal = (0,0,0)
  PerimeterLength = 4900
  Placement = pos=(6510,3350,-650) rot=(0,0,1;0rad)
  PredefinedType = 0
  VerticalArea = 1.47e+06
  Width = 300
FEATURE [Part::FeaturePython] Structure068  label="Beam029"  # Arch/BIM 7 (typed FeaturePython)
  FaceMaker = 0
  Height = 300
  HorizontalArea = 1.059e+06
  IfcData = attributes={"GlobalId": {"name": "GlobalId", "type": "IfcGloballyUniqueId", "is_enum": false, "enum_values": []}, "Description": {"... (+475 chars omitted),+1 more (map truncated)
  IfcType = 7
  Length = 3530
  MoveBase = false
  MoveWithHost = false
  Nodes = (2) [(1.2326e-31,-1.51582e-15,5.55112e-16),(3530,-1.51582e-15,5.55112e-16)]
  NodesOffset = 0
  Normal = (0,0,0)
  PerimeterLength = 7660
  Placement = pos=(2280,100,-650) rot=(0,0,1;0rad)
  PredefinedType = 0
  VerticalArea = 2.298e+06
  Width = 300
FEATURE [Part::FeaturePython] Structure069  label="Beam030"  # Arch/BIM 7 (typed FeaturePython)
  FaceMaker = 0
  Height = 300
  HorizontalArea = 645000
  IfcData = attributes={"GlobalId": {"name": "GlobalId", "type": "IfcGloballyUniqueId", "is_enum": false, "enum_values": []}, "Description": {"... (+475 chars omitted),+1 more (map truncated)
  IfcType = 7
  Length = 2150
  MoveBase = false
  MoveWithHost = false
  Nodes = (2) [(1.2326e-31,-1.51582e-15,5.55112e-16),(2150,-1.51582e-15,5.55112e-16)]
  NodesOffset = 0
  Normal = (0,0,0)
  PerimeterLength = 4900
  Placement = pos=(6510,100,-650) rot=(0,0,1;0rad)
  PredefinedType = 0
  VerticalArea = 1.47e+06
  Width = 300
FEATURE [Part::FeaturePython] Structure070  label="Beam031"  # Arch/BIM 7 (typed FeaturePython)
  FaceMaker = 0
  Height = 300
  HorizontalArea = 255000
  IfcData = attributes={"GlobalId": {"name": "GlobalId", "type": "IfcGloballyUniqueId", "is_enum": false, "enum_values": []}, "Description": {"... (+475 chars omitted),+1 more (map truncated)
  IfcType = 7
  Length = 850
  MoveBase = false
  MoveWithHost = false
  Nodes = (2) [(1.2326e-31,-1.51582e-15,5.55112e-16),(850,-1.51582e-15,5.55112e-16)]
  NodesOffset = 0
  Normal = (0,0,0)
  PerimeterLength = 2300
  Placement = pos=(9360,100,-650) rot=(0,0,1;0rad)
  PredefinedType = 0
  VerticalArea = 690000
  Width = 300
FEATURE [Part::FeaturePython] Structure071  label="Beam032"  # Arch/BIM 7 (typed FeaturePython)
  FaceMaker = 0
  Height = 300
  HorizontalArea = 756000
  IfcData = attributes={"GlobalId": {"name": "GlobalId", "type": "IfcGloballyUniqueId", "is_enum": false, "enum_values": []}, "Description": {"... (+475 chars omitted),+1 more (map truncated)
  IfcType = 7
  Length = 2520
  MoveBase = false
  MoveWithHost = false
  Nodes = (2) [(1.2326e-31,-1.51582e-15,5.55112e-16),(2520,-1.51582e-15,5.55112e-16)]
  NodesOffset = 0
  Normal = (0,0,0)
  PerimeterLength = 5640
  Placement = pos=(10910,100,-650) rot=(0,0,1;0rad)
  PredefinedType = 0
  VerticalArea = 1.692e+06
  Width = 300
FEATURE [Part::FeaturePython] Structure072  label="Beam033"  # Arch/BIM 7 (typed FeaturePython)
  FaceMaker = 0
  Height = 300
  HorizontalArea = 255000
  IfcData = attributes={"GlobalId": {"name": "GlobalId", "type": "IfcGloballyUniqueId", "is_enum": false, "enum_values": []}, "Description": {"... (+475 chars omitted),+1 more (map truncated)
  IfcType = 7
  Length = 850
  MoveBase = false
  MoveWithHost = false
  Nodes = (2) [(1.2326e-31,-1.51582e-15,5.55112e-16),(850,-1.51582e-15,5.55112e-16)]
  NodesOffset = 0
  Normal = (0,0,0)
  PerimeterLength = 2300
  Placement = pos=(9360,3350,-650) rot=(0,0,1;0rad)
  PredefinedType = 0
  VerticalArea = 690000
  Width = 300
FEATURE [Part::FeaturePython] Structure073  label="Beam034"  # Arch/BIM 7 (typed FeaturePython)
  FaceMaker = 0
  Height = 300
  HorizontalArea = 756000
  IfcData = attributes={"GlobalId": {"name": "GlobalId", "type": "IfcGloballyUniqueId", "is_enum": false, "enum_values": []}, "Description": {"... (+475 chars omitted),+1 more (map truncated)
  IfcType = 7
  Length = 2520
  MoveBase = false
  MoveWithHost = false
  Nodes = (2) [(1.2326e-31,-1.51582e-15,5.55112e-16),(2520,-1.51582e-15,5.55112e-16)]
  NodesOffset = 0
  Normal = (0,0,0)
  PerimeterLength = 5640
  Placement = pos=(10910,3350,-650) rot=(0,0,1;0rad)
  PredefinedType = 0
  VerticalArea = 1.692e+06
  Width = 300
FEATURE [Part::FeaturePython] Structure074  label="Beam035"  # Arch/BIM 7 (typed FeaturePython)
  FaceMaker = 0
  Height = 300
  HorizontalArea = 969000
  IfcData = attributes={"GlobalId": {"name": "GlobalId", "type": "IfcGloballyUniqueId", "is_enum": false, "enum_values": []}, "Description": {"... (+475 chars omitted),+1 more (map truncated)
  IfcType = 7
  Length = 3230
  MoveBase = false
  MoveWithHost = false
  Nodes = (2) [(1.2326e-31,-1.51582e-15,5.55112e-16),(3230,-1.51582e-15,5.55112e-16)]
  NodesOffset = 0
  Normal = (0,0,0)
  PerimeterLength = 7060
  Placement = pos=(15210,9550,-650) rot=(0,0,-1;1.5708rad)
  PredefinedType = 0
  VerticalArea = 2.118e+06
  Width = 300
FEATURE [Part::FeaturePython] Structure075  label="Beam036"  # Arch/BIM 7 (typed FeaturePython)
  FaceMaker = 0
  Height = 300
  HorizontalArea = 576000
  IfcData = attributes={"GlobalId": {"name": "GlobalId", "type": "IfcGloballyUniqueId", "is_enum": false, "enum_values": []}, "Description": {"... (+475 chars omitted),+1 more (map truncated)
  IfcType = 7
  Length = 1920
  MoveBase = false
  MoveWithHost = false
  Nodes = (2) [(1.2326e-31,-1.51582e-15,5.55112e-16),(1920,-1.51582e-15,5.55112e-16)]
  NodesOffset = 0
  Normal = (0,0,0)
  PerimeterLength = 4440
  Placement = pos=(13780,3700,-650) rot=(0,0,1;1.5708rad)
  PredefinedType = 0
  VerticalArea = 1.332e+06
  Width = 300
FEATURE [Part::FeaturePython] Structure076  label="Beam037"  # Arch/BIM 7 (typed FeaturePython)
  FaceMaker = 0
  Height = 300
  HorizontalArea = 219000
  IfcData = attributes={"GlobalId": {"name": "GlobalId", "type": "IfcGloballyUniqueId", "is_enum": false, "enum_values": []}, "Description": {"... (+475 chars omitted),+1 more (map truncated)
  IfcType = 7
  Length = 730
  MoveBase = false
  MoveWithHost = false
  Nodes = (2) [(1.2326e-31,-1.51582e-15,5.55112e-16),(730,-1.51582e-15,5.55112e-16)]
  NodesOffset = 0
  Normal = (0,0,0)
  PerimeterLength = 2060
  Placement = pos=(14130,5970,-650) rot=(0,0,1;0rad)
  PredefinedType = 0
  VerticalArea = 618000
  Width = 300
FEATURE [Part::FeaturePython] Structure077  label="Beam038"  # Arch/BIM 7 (typed FeaturePython)
  FaceMaker = 0
  Height = 300
  HorizontalArea = 681000
  IfcData = attributes={"GlobalId": {"name": "GlobalId", "type": "IfcGloballyUniqueId", "is_enum": false, "enum_values": []}, "Description": {"... (+475 chars omitted),+1 more (map truncated)
  IfcType = 7
  Length = 2270
  MoveBase = false
  MoveWithHost = false
  Nodes = (2) [(1.2326e-31,-1.51582e-15,5.55112e-16),(2270,-1.51582e-15,5.55112e-16)]
  NodesOffset = 0
  Normal = (0,0,0)
  PerimeterLength = 5140
  Placement = pos=(10560,3700,-650) rot=(0,0,1;1.5708rad)
  PredefinedType = 0
  VerticalArea = 1.542e+06
  Width = 300
FEATURE [Part::FeaturePython] Structure078  label="Beam039"  # Arch/BIM 7 (typed FeaturePython)
  FaceMaker = 0
  Height = 300
  HorizontalArea = 414000
  IfcData = attributes={"GlobalId": {"name": "GlobalId", "type": "IfcGloballyUniqueId", "is_enum": false, "enum_values": []}, "Description": {"... (+475 chars omitted),+1 more (map truncated)
  IfcType = 7
  Length = 1380
  MoveBase = false
  MoveWithHost = false
  Nodes = (2) [(1.2326e-31,-1.51582e-15,5.55112e-16),(1380,-1.51582e-15,5.55112e-16)]
  NodesOffset = 0
  Normal = (0,0,0)
  PerimeterLength = 3360
  Placement = pos=(10560,9750,-650) rot=(0,0,-1;1.5708rad)
  PredefinedType = 0
  VerticalArea = 1.008e+06
  Width = 300
FEATURE [Part::FeaturePython] Structure079  label="Beam040"  # Arch/BIM 7 (typed FeaturePython)
  FaceMaker = 0
  Height = 300
  HorizontalArea = 354000
  IfcData = attributes={"GlobalId": {"name": "GlobalId", "type": "IfcGloballyUniqueId", "is_enum": false, "enum_values": []}, "Description": {"... (+475 chars omitted),+1 more (map truncated)
  IfcType = 7
  Length = 1180
  MoveBase = false
  MoveWithHost = false
  Nodes = (2) [(1.2326e-31,-1.51582e-15,5.55112e-16),(1180,-1.51582e-15,5.55112e-16)]
  NodesOffset = 0
  Normal = (0,0,0)
  PerimeterLength = 2960
  Placement = pos=(12010,9550,-650) rot=(0,0,-1;1.5708rad)
  PredefinedType = 0
  VerticalArea = 888000
  Width = 300
FEATURE [Part::FeaturePython] Structure080  label="Beam041"  # Arch/BIM 7 (typed FeaturePython)
  FaceMaker = 0
  Height = 300
  HorizontalArea = 426000
  IfcData = attributes={"GlobalId": {"name": "GlobalId", "type": "IfcGloballyUniqueId", "is_enum": false, "enum_values": []}, "Description": {"... (+475 chars omitted),+1 more (map truncated)
  IfcType = 7
  Length = 1420
  MoveBase = false
  MoveWithHost = false
  Nodes = (2) [(1.2326e-31,-1.51582e-15,5.55112e-16),(1420,-1.51582e-15,5.55112e-16)]
  NodesOffset = 0
  Normal = (0,0,0)
  PerimeterLength = 3440
  Placement = pos=(13430,5970,-650) rot=(0,0,1;3.14159rad)
  PredefinedType = 0
  VerticalArea = 1.032e+06
  Width = 300
FEATURE [Part::FeaturePython] Structure081  label="25x15 C1"  # Arch/BIM 24 (typed FeaturePython)
  FaceMaker = 0
  Height = 3500
  HorizontalArea = 37500
  IfcData = attributes={"GlobalId": {"name": "GlobalId", "type": "IfcGloballyUniqueId", "is_enum": false, "enum_values": []}, "Description": {"... (+438 chars omitted),+1 more (map truncated)
  IfcType = 24
  Length = 250
  MoveBase = false
  MoveWithHost = false
  Nodes = (2) [(-1.05471e-15,1.36424e-15,0),(-1.05471e-15,1.36424e-15,3500)]
  NodesOffset = 0
  Normal = (0,0,0)
  PerimeterLength = 800
  Placement = pos=(1930,9900,-500) rot=(0,0,1;0rad)
  PredefinedType = 0
  VerticalArea = 2.8e+06
  Width = 150
FEATURE [Part::FeaturePython] Structure084  label="25x15 C004"  # Arch/BIM 172 (typed FeaturePython)
  CloneOf = -> Structure081
  FaceMaker = 0
  Height = 3500
  HorizontalArea = 37500
  IfcData = attributes={"GlobalId": {"name": "GlobalId", "type": "IfcGloballyUniqueId", "is_enum": false, "enum_values": []}, "Description": {"... (+484 chars omitted),+1 more (map truncated)
  IfcType = 172
  Length = 250
  MoveBase = false
  MoveWithHost = false
  Nodes = (2) [(-1.05471e-15,1.36424e-15,0),(-1.05471e-15,1.36424e-15,3500)]
  NodesOffset = 0
  Normal = (0,0,0)
  PerimeterLength = 800
  Placement = pos=(1930,100,-500) rot=(0,0,1;0rad)
  PredefinedType = 0
  VerticalArea = 2.8e+06
  Width = 150
FEATURE [Part::FeaturePython] Structure085  label="25x20 C6"  # Arch/BIM 24 (typed FeaturePython)
  FaceMaker = 0
  Height = 3500
  HorizontalArea = 50000
  IfcData = attributes={"GlobalId": {"name": "GlobalId", "type": "IfcGloballyUniqueId", "is_enum": false, "enum_values": []}, "Description": {"... (+438 chars omitted),+1 more (map truncated)
  IfcType = 24
  Length = 250
  MoveBase = false
  MoveWithHost = false
  Nodes = (2) [(-1.05471e-15,-1.81899e-15,0),(-1.05471e-15,-1.81899e-15,3500)]
  NodesOffset = 0
  Normal = (0,0,0)
  PerimeterLength = 900
  Placement = pos=(1930,6640,-500) rot=(0,0,1;0rad)
  PredefinedType = 0
  VerticalArea = 3.15e+06
  Width = 200
FEATURE [Part::FeaturePython] Structure086  label="25x20 C007"  # Arch/BIM 172 (typed FeaturePython)
  CloneOf = -> Structure085
  FaceMaker = 0
  Height = 3500
  HorizontalArea = 50000
  IfcData = attributes={"GlobalId": {"name": "GlobalId", "type": "IfcGloballyUniqueId", "is_enum": false, "enum_values": []}, "Description": {"... (+484 chars omitted),+1 more (map truncated)
  IfcType = 172
  Length = 250
  MoveBase = false
  MoveWithHost = false
  Nodes = (2) [(-1.05471e-15,-1.81899e-15,0),(-1.05471e-15,-1.81899e-15,3500)]
  NodesOffset = 0
  Normal = (0,0,0)
  PerimeterLength = 900
  Placement = pos=(1930,3350,-500) rot=(0,0,1;0rad)
  PredefinedType = 0
  VerticalArea = 3.15e+06
  Width = 200
FEATURE [Part::FeaturePython] Structure088  label="25x15 C005"  # Arch/BIM 24 (typed FeaturePython)
  FaceMaker = 0
  Height = 3500
  HorizontalArea = 37500
  IfcData = attributes={"GlobalId": {"name": "GlobalId", "type": "IfcGloballyUniqueId", "is_enum": false, "enum_values": []}, "Description": {"... (+438 chars omitted),+1 more (map truncated)
  IfcType = 24
  Length = 250
  MoveBase = false
  MoveWithHost = false
  Nodes = (2) [(-1.05471e-15,1.36424e-15,0),(-1.05471e-15,1.36424e-15,3500)]
  NodesOffset = 0
  Normal = (0,0,0)
  PerimeterLength = 800
  Placement = pos=(6160,6640,-500) rot=(0,0,1;0rad)
  PredefinedType = 0
  VerticalArea = 2.8e+06
  Width = 150
FEATURE [Part::FeaturePython] Structure089  label="25x15 C006"  # Arch/BIM 24 (typed FeaturePython)
  FaceMaker = 0
  Height = 3500
  HorizontalArea = 37500
  IfcData = attributes={"GlobalId": {"name": "GlobalId", "type": "IfcGloballyUniqueId", "is_enum": false, "enum_values": []}, "Description": {"... (+438 chars omitted),+1 more (map truncated)
  IfcType = 24
  Length = 250
  MoveBase = false
  MoveWithHost = false
  Nodes = (2) [(-1.05471e-15,1.36424e-15,0),(-1.05471e-15,1.36424e-15,3500)]
  NodesOffset = 0
  Normal = (0,0,0)
  PerimeterLength = 800
  Placement = pos=(6160,3350,-500) rot=(0,0,1;0rad)
  PredefinedType = 0
  VerticalArea = 2.8e+06
  Width = 150
FEATURE [Part::FeaturePython] Structure090  label="25x15 C007"  # Arch/BIM 24 (typed FeaturePython)
  FaceMaker = 0
  Height = 3500
  HorizontalArea = 37500
  IfcData = attributes={"GlobalId": {"name": "GlobalId", "type": "IfcGloballyUniqueId", "is_enum": false, "enum_values": []}, "Description": {"... (+438 chars omitted),+1 more (map truncated)
  IfcType = 24
  Length = 250
  MoveBase = false
  MoveWithHost = false
  Nodes = (2) [(-1.05471e-15,1.36424e-15,0),(-1.05471e-15,1.36424e-15,3500)]
  NodesOffset = 0
  Normal = (0,0,0)
  PerimeterLength = 800
  Placement = pos=(6160,100,-500) rot=(0,0,1;0rad)
  PredefinedType = 0
  VerticalArea = 2.8e+06
  Width = 150
FEATURE [Part::FeaturePython] Structure091  label="25x15 C008"  # Arch/BIM 24 (typed FeaturePython)
  FaceMaker = 0
  Height = 3500
  HorizontalArea = 37500
  IfcData = attributes={"GlobalId": {"name": "GlobalId", "type": "IfcGloballyUniqueId", "is_enum": false, "enum_values": []}, "Description": {"... (+438 chars omitted),+1 more (map truncated)
  IfcType = 24
  Length = 250
  MoveBase = false
  MoveWithHost = false
  Nodes = (2) [(-1.05471e-15,1.36424e-15,0),(-1.05471e-15,1.36424e-15,3500)]
  NodesOffset = 0
  Normal = (0,0,0)
  PerimeterLength = 800
  Placement = pos=(9010,100,-500) rot=(0,0,1;0rad)
  PredefinedType = 0
  VerticalArea = 2.8e+06
  Width = 150
FEATURE [Part::FeaturePython] Structure092  label="25x15 C009"  # Arch/BIM 24 (typed FeaturePython)
  FaceMaker = 0
  Height = 3500
  HorizontalArea = 37500
  IfcData = attributes={"GlobalId": {"name": "GlobalId", "type": "IfcGloballyUniqueId", "is_enum": false, "enum_values": []}, "Description": {"... (+438 chars omitted),+1 more (map truncated)
  IfcType = 24
  Length = 250
  MoveBase = false
  MoveWithHost = false
  Nodes = (2) [(-1.05471e-15,1.36424e-15,0),(-1.05471e-15,1.36424e-15,3500)]
  NodesOffset = 0
  Normal = (0,0,0)
  PerimeterLength = 800
  Placement = pos=(10560,100,-500) rot=(0,0,1;0rad)
  PredefinedType = 0
  VerticalArea = 2.8e+06
  Width = 150
FEATURE [Part::FeaturePython] Structure093  label="25x15 C010"  # Arch/BIM 24 (typed FeaturePython)
  FaceMaker = 0
  Height = 3500
  HorizontalArea = 37500
  IfcData = attributes={"GlobalId": {"name": "GlobalId", "type": "IfcGloballyUniqueId", "is_enum": false, "enum_values": []}, "Description": {"... (+438 chars omitted),+1 more (map truncated)
  IfcType = 24
  Length = 250
  MoveBase = false
  MoveWithHost = false
  Nodes = (2) [(-1.05471e-15,1.36424e-15,0),(-1.05471e-15,1.36424e-15,3500)]
  NodesOffset = 0
  Normal = (0,0,0)
  PerimeterLength = 800
  Placement = pos=(13780,100,-500) rot=(0,0,1;0rad)
  PredefinedType = 0
  VerticalArea = 2.8e+06
  Width = 150
FEATURE [Part::FeaturePython] Structure097  label="25x15 C014"  # Arch/BIM 24 (typed FeaturePython)
  FaceMaker = 0
  Height = 3500
  HorizontalArea = 37500
  IfcData = attributes={"GlobalId": {"name": "GlobalId", "type": "IfcGloballyUniqueId", "is_enum": false, "enum_values": []}, "Description": {"... (+438 chars omitted),+1 more (map truncated)
  IfcType = 24
  Length = 250
  MoveBase = false
  MoveWithHost = false
  Nodes = (2) [(-1.05471e-15,1.36424e-15,0),(-1.05471e-15,1.36424e-15,3500)]
  NodesOffset = 0
  Normal = (0,0,0)
  PerimeterLength = 800
  Placement = pos=(15210,5970,-500) rot=(0,0,1;0rad)
  PredefinedType = 0
  VerticalArea = 2.8e+06
  Width = 150
FEATURE [Part::FeaturePython] Structure098  label="25x15 C015"  # Arch/BIM 24 (typed FeaturePython)
  FaceMaker = 0
  Height = 3500
  HorizontalArea = 37500
  IfcData = attributes={"GlobalId": {"name": "GlobalId", "type": "IfcGloballyUniqueId", "is_enum": false, "enum_values": []}, "Description": {"... (+438 chars omitted),+1 more (map truncated)
  IfcType = 24
  Length = 250
  MoveBase = false
  MoveWithHost = false
  Nodes = (2) [(-1.05471e-15,1.36424e-15,0),(-1.05471e-15,1.36424e-15,3500)]
  NodesOffset = 0
  Normal = (0,0,0)
  PerimeterLength = 800
  Placement = pos=(13780,5970,-500) rot=(0,0,1;0rad)
  PredefinedType = 0
  VerticalArea = 2.8e+06
  Width = 150
FEATURE [Part::Part2DObjectPython] Rectangle  # Draft 2D object (typed FeaturePython)
  Area = 0
  ChamferSize = 0
  Columns = 1
  FilletRadius = 0
  Height = 2550
  Length = 1600
  MakeFace = false
  Placement = pos=(10485,5895,0) rot=(0,0,1;0rad)
  Rows = 1
FEATURE [Part::FeaturePython] Wall  label="Tabique Ascensor"  # Arch/BIM 166 (typed FeaturePython)
  Align = 1
  Area = 8300000
  Base = -> Rectangle
  BlockHeight = 0
  BlockLength = 0
  CountBroken = 0
  CountEntire = 0
  Face = 0
  Height = 1000
  HorizontalArea = 1155000
  IfcData = attributes={"GlobalId": {"name": "GlobalId", "type": "IfcGloballyUniqueId", "is_enum": false, "enum_values": []}, "Description": {"... (+533 chars omitted),+1 more (map truncated)
  IfcType = 166
  Joint = 0
  Length = 8300
  MakeBlocks = false
  MoveBase = false
  MoveWithHost = false
  Normal = (0,0,0)
  OffsetFirst = 0
  OffsetSecond = 0
  PerimeterLength = 8300
  Placement = pos=(0,0,-1000) rot=(0,0,1;0rad)
  PredefinedType = 0
  VerticalArea = 15400000
  Width = 150
FEATURE [App::GeometryPython] BuildingPart006  label="Pilotes"  # Arch/BIM 172 (typed FeaturePython)
  Area = 0
  Group = -> [Structure001,Structure021,Structure005,Structure023,Structure025,Structure027,Structure028,Structure031,Structure033,Structure035,Structure037,Structure007,Structure039,Structure009,Structure011,Structure013,Structure003,Structure015,Structure017,Structure019]
  Height = 0
  HeightPropagate = true
  IfcData = attributes={"GlobalId": {"name": "GlobalId", "type": "IfcGloballyUniqueId", "is_enum": false, "enum_values": []}, "Description": {"... (+484 chars omitted),+1 more (map truncated)
  IfcType = 172
  LevelOffset = 0
  Placement = pos=(0,0,500) rot=(0,0,1;0rad)
  PredefinedType = 0
FEATURE [App::GeometryPython] BuildingPart007  label="Cabezales Pilotes"  # Arch/BIM 172 (typed FeaturePython)
  Area = 0
  Group = -> [Structure,Structure020,Structure004,Structure022,Structure024,Structure026,Structure029,Structure030,Structure032,Structure034,Structure036,Structure006,Structure038,Structure008,Structure010,Structure012,Structure002,Structure014,Structure016,Structure018]
  Height = 0
  HeightPropagate = true
  IfcData = attributes={"GlobalId": {"name": "GlobalId", "type": "IfcGloballyUniqueId", "is_enum": false, "enum_values": []}, "Description": {"... (+484 chars omitted),+1 more (map truncated)
  IfcType = 172
  LevelOffset = 0
  Placement = pos=(0,0,500) rot=(0,0,1;0rad)
  PredefinedType = 0
FEATURE [App::GeometryPython] BuildingPart008  label="Losa fundacion"  # Arch/BIM 172 (typed FeaturePython)
  Area = 0
  Group = -> [Structure040]
  Height = 0
  HeightPropagate = true
  IfcData = attributes={"GlobalId": {"name": "GlobalId", "type": "IfcGloballyUniqueId", "is_enum": false, "enum_values": []}, "Description": {"... (+484 chars omitted),+1 more (map truncated)
  IfcType = 172
  LevelOffset = 0
  Placement = pos=(0,0,500) rot=(0,0,1;0rad)
  PredefinedType = 0
FEATURE [Part::FeaturePython] Structure099  label="25x15 C016"  # Arch/BIM 172 (typed FeaturePython)
  CloneOf = -> Structure081
  FaceMaker = 0
  Height = 3500
  HorizontalArea = 37500
  IfcData = attributes={"GlobalId": {"name": "GlobalId", "type": "IfcGloballyUniqueId", "is_enum": false, "enum_values": []}, "Description": {"... (+484 chars omitted),+1 more (map truncated)
  IfcType = 172
  Length = 250
  MoveBase = false
  MoveWithHost = false
  Nodes = (2) [(-1.05471e-15,1.36424e-15,0),(-1.05471e-15,1.36424e-15,3500)]
  NodesOffset = 0
  Normal = (0,0,0)
  PerimeterLength = 800
  Placement = pos=(1930,9900,-500) rot=(0,0,1;0rad)
  PredefinedType = 0
  VerticalArea = 2.8e+06
  Width = 150
FEATURE [Part::FeaturePython] Structure100  label="25x15 C017"  # Arch/BIM 172 (typed FeaturePython)
  CloneOf = -> Structure081
  FaceMaker = 0
  Height = 3500
  HorizontalArea = 37500
  IfcData = attributes={"GlobalId": {"name": "GlobalId", "type": "IfcGloballyUniqueId", "is_enum": false, "enum_values": []}, "Description": {"... (+484 chars omitted),+1 more (map truncated)
  IfcType = 172
  Length = 250
  MoveBase = false
  MoveWithHost = false
  Nodes = (2) [(-1.05471e-15,1.36424e-15,0),(-1.05471e-15,1.36424e-15,3500)]
  NodesOffset = 0
  Normal = (0,0,0)
  PerimeterLength = 800
  Placement = pos=(9010,6640,-500) rot=(0,0,1;1.5708rad)
  PredefinedType = 0
  VerticalArea = 2.8e+06
  Width = 150
FEATURE [Part::FeaturePython] Structure101  label="25x15 C018"  # Arch/BIM 172 (typed FeaturePython)
  CloneOf = -> Structure081
  FaceMaker = 0
  Height = 3500
  HorizontalArea = 37500
  IfcData = attributes={"GlobalId": {"name": "GlobalId", "type": "IfcGloballyUniqueId", "is_enum": false, "enum_values": []}, "Description": {"... (+484 chars omitted),+1 more (map truncated)
  IfcType = 172
  Length = 250
  MoveBase = false
  MoveWithHost = false
  Nodes = (2) [(-1.05471e-15,1.36424e-15,0),(-1.05471e-15,1.36424e-15,3500)]
  NodesOffset = 0
  Normal = (0,0,0)
  PerimeterLength = 800
  Placement = pos=(9010,3350,-500) rot=(0,0,1;1.5708rad)
  PredefinedType = 0
  VerticalArea = 2.8e+06
  Width = 150
FEATURE [Part::FeaturePython] Structure102  label="25x15 C019"  # Arch/BIM 172 (typed FeaturePython)
  CloneOf = -> Structure081
  FaceMaker = 0
  Height = 3500
  HorizontalArea = 37500
  IfcData = attributes={"GlobalId": {"name": "GlobalId", "type": "IfcGloballyUniqueId", "is_enum": false, "enum_values": []}, "Description": {"... (+484 chars omitted),+1 more (map truncated)
  IfcType = 172
  Length = 250
  MoveBase = false
  MoveWithHost = false
  Nodes = (2) [(-1.05471e-15,1.36424e-15,0),(-1.05471e-15,1.36424e-15,3500)]
  NodesOffset = 0
  Normal = (0,0,0)
  PerimeterLength = 800
  Placement = pos=(10560,3350,-500) rot=(0,0,1;1.5708rad)
  PredefinedType = 0
  VerticalArea = 2.8e+06
  Width = 150
FEATURE [Part::FeaturePython] Structure103  label="25x15 C020"  # Arch/BIM 172 (typed FeaturePython)
  CloneOf = -> Structure081
  FaceMaker = 0
  Height = 3500
  HorizontalArea = 37500
  IfcData = attributes={"GlobalId": {"name": "GlobalId", "type": "IfcGloballyUniqueId", "is_enum": false, "enum_values": []}, "Description": {"... (+484 chars omitted),+1 more (map truncated)
  IfcType = 172
  Length = 250
  MoveBase = false
  MoveWithHost = false
  Nodes = (2) [(-1.05471e-15,1.36424e-15,0),(-1.05471e-15,1.36424e-15,3500)]
  NodesOffset = 0
  Normal = (0,0,0)
  PerimeterLength = 800
  Placement = pos=(13780,3350,-500) rot=(0,0,1;1.5708rad)
  PredefinedType = 0
  VerticalArea = 2.8e+06
  Width = 150
FEATURE [Spreadsheet::Sheet] Spreadsheet  label="Estructura"
  cells = A1=MODELO ESTRUCTURAL; A2=Descripcion; B2=Alias; C2=Valor; D2=Unidad; A3=Cabezal Ancho; B3=CabAncho; C3(CabAncho)=700; D3=mm; A4=Cabezal Espesor; B4=CabEsp; C4(CabEsp)=700; D4=mm; A5=Pilote Radio; B5=PilRad; C5(PilRad)=250; D5=mm; A6=Pilote Profundidad; B6=PilProf; C6(PilProf)=8000; D6=mm; A7=Viga Riostra Ancho; B7=VRAncho; C7(VRAncho)=300; D7=mm; A8=Viga Riostra Alto; B8=VRAlto; C8(VRAlto)=300; D8=mm
FEATURE [Part::FeaturePython] Structure104  label="25x15 C003"  # Arch/BIM 172 (typed FeaturePython)
  CloneOf = -> Structure081
  FaceMaker = 0
  Height = 3500
  HorizontalArea = 37500
  IfcData = attributes={"GlobalId": {"name": "GlobalId", "type": "IfcGloballyUniqueId", "is_enum": false, "enum_values": []}, "Description": {"... (+484 chars omitted),+1 more (map truncated)
  IfcType = 172
  Length = 250
  MoveBase = false
  MoveWithHost = false
  Nodes = (2) [(-1.05471e-15,1.36424e-15,0),(-1.05471e-15,1.36424e-15,3500)]
  NodesOffset = 0
  Normal = (0,0,0)
  PerimeterLength = 800
  Placement = pos=(9010,9900,-500) rot=(0,0,1;0rad)
  PredefinedType = 0
  VerticalArea = 2.8e+06
  Width = 150
FEATURE [Part::FeaturePython] Structure105  label="25x15 C002"  # Arch/BIM 172 (typed FeaturePython)
  CloneOf = -> Structure081
  FaceMaker = 0
  Height = 3500
  HorizontalArea = 37500
  IfcData = attributes={"GlobalId": {"name": "GlobalId", "type": "IfcGloballyUniqueId", "is_enum": false, "enum_values": []}, "Description": {"... (+484 chars omitted),+1 more (map truncated)
  IfcType = 172
  Length = 250
  MoveBase = false
  MoveWithHost = false
  Nodes = (2) [(-1.05471e-15,1.36424e-15,0),(-1.05471e-15,1.36424e-15,3500)]
  NodesOffset = 0
  Normal = (0,0,0)
  PerimeterLength = 800
  Placement = pos=(6160,9900,-500) rot=(0,0,1;0rad)
  PredefinedType = 0
  VerticalArea = 2.8e+06
  Width = 150
FEATURE [Part::FeaturePython] Structure106  label="25x15 C025"  # Arch/BIM 172 (typed FeaturePython)
  CloneOf = -> Structure081
  FaceMaker = 0
  Height = 3500
  HorizontalArea = 37500
  IfcData = attributes={"GlobalId": {"name": "GlobalId", "type": "IfcGloballyUniqueId", "is_enum": false, "enum_values": []}, "Description": {"... (+484 chars omitted),+1 more (map truncated)
  IfcType = 172
  Length = 250
  MoveBase = false
  MoveWithHost = false
  Nodes = (2) [(-1.05471e-15,1.36424e-15,0),(-1.05471e-15,1.36424e-15,3500)]
  NodesOffset = 0
  Normal = (0,0,0)
  PerimeterLength = 800
  Placement = pos=(12010,9900,-500) rot=(0,0,1;0rad)
  PredefinedType = 0
  VerticalArea = 2.8e+06
  Width = 150
FEATURE [Part::FeaturePython] Structure107  label="25x15 C024"  # Arch/BIM 172 (typed FeaturePython)
  CloneOf = -> Structure081
  FaceMaker = 0
  Height = 3500
  HorizontalArea = 37500
  IfcData = attributes={"GlobalId": {"name": "GlobalId", "type": "IfcGloballyUniqueId", "is_enum": false, "enum_values": []}, "Description": {"... (+484 chars omitted),+1 more (map truncated)
  IfcType = 172
  Length = 250
  MoveBase = false
  MoveWithHost = false
  Nodes = (2) [(-1.05471e-15,1.36424e-15,0),(-1.05471e-15,1.36424e-15,3500)]
  NodesOffset = 0
  Normal = (0,0,0)
  PerimeterLength = 800
  Placement = pos=(15210,9900,-500) rot=(0,0,1;0rad)
  PredefinedType = 0
  VerticalArea = 2.8e+06
  Width = 150
FEATURE [App::GeometryPython] BuildingPart004  label="Columnas"  # Arch/BIM 172 (typed FeaturePython)
  Area = 0
  Group = -> [Structure105,Structure104,Structure084,Structure088,Structure089,Structure090,Structure091,Structure092,Structure093,Structure097,Structure098,Structure099,Structure100,Structure101,Structure102,Structure103,Structure107,Structure106,Structure081,Structure086,Structure085]
  Height = 0
  HeightPropagate = true
  IfcData = attributes={"GlobalId": {"name": "GlobalId", "type": "IfcGloballyUniqueId", "is_enum": false, "enum_values": []}, "Description": {"... (+484 chars omitted),+1 more (map truncated)
  IfcType = 172
  LevelOffset = 0
  PredefinedType = 0
FEATURE [Part::FeaturePython] Beam  # Arch/BIM 7 (typed FeaturePython)
  Chamfer = 0
  DentHeight = 0
  DentLength = 0
  Height = 300
  HorizontalArea = 1059000
  IfcData = attributes={"GlobalId": {"name": "GlobalId", "type": "IfcGloballyUniqueId", "is_enum": false, "enum_values": []}, "Description": {"... (+475 chars omitted),+1 more (map truncated)
  IfcType = 7
  Length = 3530
  MoveBase = false
  MoveWithHost = false
  PerimeterLength = 7660
  Placement = pos=(2280,9750,-800) rot=(0,0,1;0rad)
  PredefinedType = 0
  VerticalArea = 2298000
  Width = 300
FEATURE [App::GeometryPython] BuildingPart005  label="Vigas riostras"  # Arch/BIM 172 (typed FeaturePython)
  Area = 0
  Group = -> [Beam,Beam001,Structure041,Structure042,Structure043,Structure044,Structure045,Structure046,Structure048,Structure049,Structure053,Structure056,Structure059,Structure060,Structure061,Structure064,Structure065,Structure066,Structure067,Structure068,Structure069,Structure070,Structure071,Structure072,Structure073,Structure074,Structure075,Structure076,Structure077,Structure078,Structure079,+1 more]
  Height = 0
  HeightPropagate = true
  IfcData = attributes={"GlobalId": {"name": "GlobalId", "type": "IfcGloballyUniqueId", "is_enum": false, "enum_values": []}, "Description": {"... (+484 chars omitted),+1 more (map truncated)
  IfcType = 172
  LevelOffset = 0
  Placement = pos=(0,0,500) rot=(0,0,1;0rad)
  PredefinedType = 0
FEATURE [App::GeometryPython] BuildingPart002  label="Fundaciones"  # Arch/BIM 172 (typed FeaturePython)
  Area = 8300000
  Group = -> [BuildingPart005,BuildingPart006,BuildingPart007,BuildingPart008,Wall]
  Height = 0
  HeightPropagate = true
  IfcData = attributes={"GlobalId": {"name": "GlobalId", "type": "IfcGloballyUniqueId", "is_enum": false, "enum_values": []}, "Description": {"... (+484 chars omitted),+1 more (map truncated)
  IfcType = 172
  LevelOffset = 0
  PredefinedType = 0
FEATURE [Part::Part2DObjectPython] Rectangle003  # Draft 2D object (typed FeaturePython)
  Area = 0
  ChamferSize = 0
  Columns = 1
  FilletRadius = 0
  Height = 2550
  Length = 1600
  MakeFace = false
  Placement = pos=(10485,5895,0) rot=(0,0,1;0rad)
  Rows = 1
FEATURE [Part::FeaturePython] Wall001  label="Tabique Ascensor PB"  # Arch/BIM 166 (typed FeaturePython)
  Align = 1
  Area = 24900000
  Base = -> Rectangle003
  BlockHeight = 0
  BlockLength = 0
  CountBroken = 0
  CountEntire = 0
  Face = 0
  Height = 3000
  HorizontalArea = 1155000
  IfcData = attributes={"GlobalId": {"name": "GlobalId", "type": "IfcGloballyUniqueId", "is_enum": false, "enum_values": []}, "Description": {"... (+533 chars omitted),+1 more (map truncated)
  IfcType = 166
  Joint = 0
  Length = 8300
  MakeBlocks = false
  MoveBase = false
  MoveWithHost = false
  Normal = (0,0,0)
  OffsetFirst = 0
  OffsetSecond = 0
  PerimeterLength = 8300
  PredefinedType = 0
  VerticalArea = 46200000
  Width = 150
FEATURE [Part::FeaturePython] Structure108  label="V20x40 V122"  # Arch/BIM 7 (typed FeaturePython)
  FaceMaker = 0
  Height = 400
  HorizontalArea = 617000
  IfcData = attributes={"GlobalId": {"name": "GlobalId", "type": "IfcGloballyUniqueId", "is_enum": false, "enum_values": []}, "Description": {"... (+475 chars omitted),+1 more (map truncated)
  IfcType = 7
  Length = 3085
  MoveBase = false
  MoveWithHost = false
  Nodes = (2) [(-1.72563e-31,0,-7.77156e-16),(3085,0,-7.77156e-16)]
  NodesOffset = 0
  Normal = (0,0,0)
  PerimeterLength = 6570
  Placement = pos=(1930,9825,2800) rot=(0,0,-1;1.5708rad)
  PredefinedType = 0
  VerticalArea = 2.628e+06
  Width = 200
FEATURE [Part::FeaturePython] Structure109  label="V15x40 V101"  # Arch/BIM 7 (typed FeaturePython)
  FaceMaker = 0
  Height = 400
  HorizontalArea = 597000
  IfcData = attributes={"GlobalId": {"name": "GlobalId", "type": "IfcGloballyUniqueId", "is_enum": false, "enum_values": []}, "Description": {"... (+475 chars omitted),+1 more (map truncated)
  IfcType = 7
  Length = 3980
  MoveBase = false
  MoveWithHost = false
  Nodes = (2) [(-1.72563e-31,-1.42109e-15,-7.77156e-16),(3980,-1.42109e-15,-7.77156e-16)]
  NodesOffset = 0
  Normal = (0,0,0)
  PerimeterLength = 8260
  Placement = pos=(2055,9900,2800) rot=(0,0,1;0rad)
  PredefinedType = 0
  VerticalArea = 3.304e+06
  Width = 150
FEATURE [Part::FeaturePython] Structure110  label="V20x40 V121"  # Arch/BIM 7 (typed FeaturePython)
  FaceMaker = 0
  Height = 400
  HorizontalArea = 618000
  IfcData = attributes={"GlobalId": {"name": "GlobalId", "type": "IfcGloballyUniqueId", "is_enum": false, "enum_values": []}, "Description": {"... (+475 chars omitted),+1 more (map truncated)
  IfcType = 7
  Length = 3090
  MoveBase = false
  MoveWithHost = false
  Nodes = (2) [(-1.72563e-31,0,-7.77156e-16),(3090,0,-7.77156e-16)]
  NodesOffset = 0
  Normal = (0,0,0)
  PerimeterLength = 6580
  Placement = pos=(1930,6540,2800) rot=(0,0,-1;1.5708rad)
  PredefinedType = 0
  VerticalArea = 2.632e+06
  Width = 200
FEATURE [Part::FeaturePython] Structure111  label="V20x40 V120"  # Arch/BIM 7 (typed FeaturePython)
  FaceMaker = 0
  Height = 400
  HorizontalArea = 615000
  IfcData = attributes={"GlobalId": {"name": "GlobalId", "type": "IfcGloballyUniqueId", "is_enum": false, "enum_values": []}, "Description": {"... (+475 chars omitted),+1 more (map truncated)
  IfcType = 7
  Length = 3075
  MoveBase = false
  MoveWithHost = false
  Nodes = (2) [(-1.72563e-31,0,-7.77156e-16),(3075,0,-7.77156e-16)]
  NodesOffset = 0
  Normal = (0,0,0)
  PerimeterLength = 6550
  Placement = pos=(1930,3250,2800) rot=(0,0,-1;1.5708rad)
  PredefinedType = 0
  VerticalArea = 2.62e+06
  Width = 200
FEATURE [Part::FeaturePython] Structure112  label="V15x40 V106"  # Arch/BIM 7 (typed FeaturePython)
  FaceMaker = 0
  Height = 400
  HorizontalArea = 597000
  IfcData = attributes={"GlobalId": {"name": "GlobalId", "type": "IfcGloballyUniqueId", "is_enum": false, "enum_values": []}, "Description": {"... (+475 chars omitted),+1 more (map truncated)
  IfcType = 7
  Length = 3980
  MoveBase = false
  MoveWithHost = false
  Nodes = (2) [(-1.72563e-31,-1.42109e-15,-7.77156e-16),(3980,-1.42109e-15,-7.77156e-16)]
  NodesOffset = 0
  Normal = (0,0,0)
  PerimeterLength = 8260
  Placement = pos=(2055,6640,2800) rot=(0,0,1;0rad)
  PredefinedType = 0
  VerticalArea = 3.304e+06
  Width = 150
FEATURE [Part::FeaturePython] Structure113  label="V15x40 V111"  # Arch/BIM 7 (typed FeaturePython)
  FaceMaker = 0
  Height = 400
  HorizontalArea = 597000
  IfcData = attributes={"GlobalId": {"name": "GlobalId", "type": "IfcGloballyUniqueId", "is_enum": false, "enum_values": []}, "Description": {"... (+475 chars omitted),+1 more (map truncated)
  IfcType = 7
  Length = 3980
  MoveBase = false
  MoveWithHost = false
  Nodes = (2) [(-1.72563e-31,-1.42109e-15,-7.77156e-16),(3980,-1.42109e-15,-7.77156e-16)]
  NodesOffset = 0
  Normal = (0,0,0)
  PerimeterLength = 8260
  Placement = pos=(2055,3350,2800) rot=(0,0,1;0rad)
  PredefinedType = 0
  VerticalArea = 3.304e+06
  Width = 150
FEATURE [Part::FeaturePython] Structure114  label="V15x40 V116"  # Arch/BIM 7 (typed FeaturePython)
  FaceMaker = 0
  Height = 400
  HorizontalArea = 597000
  IfcData = attributes={"GlobalId": {"name": "GlobalId", "type": "IfcGloballyUniqueId", "is_enum": false, "enum_values": []}, "Description": {"... (+475 chars omitted),+1 more (map truncated)
  IfcType = 7
  Length = 3980
  MoveBase = false
  MoveWithHost = false
  Nodes = (2) [(-1.72563e-31,-1.42109e-15,-7.77156e-16),(3980,-1.42109e-15,-7.77156e-16)]
  NodesOffset = 0
  Normal = (0,0,0)
  PerimeterLength = 8260
  Placement = pos=(2055,100,2800) rot=(0,0,1;0rad)
  PredefinedType = 0
  VerticalArea = 3.304e+06
  Width = 150
FEATURE [Part::FeaturePython] Structure115  label="V15x40 V102"  # Arch/BIM 7 (typed FeaturePython)
  FaceMaker = 0
  Height = 400
  HorizontalArea = 390000
  IfcData = attributes={"GlobalId": {"name": "GlobalId", "type": "IfcGloballyUniqueId", "is_enum": false, "enum_values": []}, "Description": {"... (+475 chars omitted),+1 more (map truncated)
  IfcType = 7
  Length = 2600
  MoveBase = false
  MoveWithHost = false
  Nodes = (2) [(-1.72563e-31,-1.42109e-15,-7.77156e-16),(2600,-1.42109e-15,-7.77156e-16)]
  NodesOffset = 0
  Normal = (0,0,0)
  PerimeterLength = 5500
  Placement = pos=(6285,9900,2800) rot=(0,0,1;0rad)
  PredefinedType = 0
  VerticalArea = 2200000
  Width = 150
FEATURE [Part::FeaturePython] Structure116  label="V15x40 V107"  # Arch/BIM 7 (typed FeaturePython)
  FaceMaker = 0
  Height = 400
  HorizontalArea = 397500
  IfcData = attributes={"GlobalId": {"name": "GlobalId", "type": "IfcGloballyUniqueId", "is_enum": false, "enum_values": []}, "Description": {"... (+475 chars omitted),+1 more (map truncated)
  IfcType = 7
  Length = 2650
  MoveBase = false
  MoveWithHost = false
  Nodes = (2) [(-1.72563e-31,-1.42109e-15,-7.77156e-16),(2650,-1.42109e-15,-7.77156e-16)]
  NodesOffset = 0
  Normal = (0,0,0)
  PerimeterLength = 5600
  Placement = pos=(6285,6640,2800) rot=(0,0,1;0rad)
  PredefinedType = 0
  VerticalArea = 2240000
  Width = 150
FEATURE [Part::FeaturePython] Structure117  label="V15x40 V112"  # Arch/BIM 7 (typed FeaturePython)
  FaceMaker = 0
  Height = 400
  HorizontalArea = 397500
  IfcData = attributes={"GlobalId": {"name": "GlobalId", "type": "IfcGloballyUniqueId", "is_enum": false, "enum_values": []}, "Description": {"... (+475 chars omitted),+1 more (map truncated)
  IfcType = 7
  Length = 2650
  MoveBase = false
  MoveWithHost = false
  Nodes = (2) [(-1.72563e-31,-1.42109e-15,-7.77156e-16),(2650,-1.42109e-15,-7.77156e-16)]
  NodesOffset = 0
  Normal = (0,0,0)
  PerimeterLength = 5600
  Placement = pos=(6285,3350,2800) rot=(0,0,1;0rad)
  PredefinedType = 0
  VerticalArea = 2240000
  Width = 150
FEATURE [Part::FeaturePython] Structure118  label="V15x40 V117"  # Arch/BIM 7 (typed FeaturePython)
  FaceMaker = 0
  Height = 400
  HorizontalArea = 390000
  IfcData = attributes={"GlobalId": {"name": "GlobalId", "type": "IfcGloballyUniqueId", "is_enum": false, "enum_values": []}, "Description": {"... (+475 chars omitted),+1 more (map truncated)
  IfcType = 7
  Length = 2600
  MoveBase = false
  MoveWithHost = false
  Nodes = (2) [(-1.72563e-31,-1.42109e-15,-7.77156e-16),(2600,-1.42109e-15,-7.77156e-16)]
  NodesOffset = 0
  Normal = (0,0,0)
  PerimeterLength = 5500
  Placement = pos=(6285,100,2800) rot=(0,0,1;0rad)
  PredefinedType = 0
  VerticalArea = 2200000
  Width = 150
FEATURE [Part::FeaturePython] Structure119  label="V15x40 V103"  # Arch/BIM 7 (typed FeaturePython)
  FaceMaker = 0
  Height = 400
  HorizontalArea = 412500
  IfcData = attributes={"GlobalId": {"name": "GlobalId", "type": "IfcGloballyUniqueId", "is_enum": false, "enum_values": []}, "Description": {"... (+475 chars omitted),+1 more (map truncated)
  IfcType = 7
  Length = 2750
  MoveBase = false
  MoveWithHost = false
  Nodes = (2) [(-1.72563e-31,-1.42109e-15,-7.77156e-16),(2750,-1.42109e-15,-7.77156e-16)]
  NodesOffset = 0
  Normal = (0,0,0)
  PerimeterLength = 5800
  Placement = pos=(9135,9900,2800) rot=(0,0,1;0rad)
  PredefinedType = 0
  VerticalArea = 2320000
  Width = 150
FEATURE [Part::FeaturePython] Structure120  label="V15x40 V104"  # Arch/BIM 7 (typed FeaturePython)
  FaceMaker = 0
  Height = 400
  HorizontalArea = 442500
  IfcData = attributes={"GlobalId": {"name": "GlobalId", "type": "IfcGloballyUniqueId", "is_enum": false, "enum_values": []}, "Description": {"... (+475 chars omitted),+1 more (map truncated)
  IfcType = 7
  Length = 2950
  MoveBase = false
  MoveWithHost = false
  Nodes = (2) [(-1.72563e-31,-1.42109e-15,-7.77156e-16),(2950,-1.42109e-15,-7.77156e-16)]
  NodesOffset = 0
  Normal = (0,0,0)
  PerimeterLength = 6200
  Placement = pos=(12135,9900,2800) rot=(0,0,1;0rad)
  PredefinedType = 0
  VerticalArea = 2.48e+06
  Width = 150
FEATURE [Part::FeaturePython] Structure121  label="V15x40 V108"  # Arch/BIM 7 (typed FeaturePython)
  FaceMaker = 0
  Height = 400
  HorizontalArea = 210000
  IfcData = attributes={"GlobalId": {"name": "GlobalId", "type": "IfcGloballyUniqueId", "is_enum": false, "enum_values": []}, "Description": {"... (+475 chars omitted),+1 more (map truncated)
  IfcType = 7
  Length = 1400
  MoveBase = false
  MoveWithHost = false
  Nodes = (2) [(-1.72563e-31,-1.42109e-15,-7.77156e-16),(1400,-1.42109e-15,-7.77156e-16)]
  NodesOffset = 0
  Normal = (0,0,0)
  PerimeterLength = 3100
  Placement = pos=(9085,6640,2800) rot=(0,0,1;0rad)
  PredefinedType = 0
  VerticalArea = 1240000
  Width = 150
FEATURE [Part::FeaturePython] Structure122  label="V15x40 V113"  # Arch/BIM 7 (typed FeaturePython)
  FaceMaker = 0
  Height = 400
  HorizontalArea = 210000
  IfcData = attributes={"GlobalId": {"name": "GlobalId", "type": "IfcGloballyUniqueId", "is_enum": false, "enum_values": []}, "Description": {"... (+475 chars omitted),+1 more (map truncated)
  IfcType = 7
  Length = 1400
  MoveBase = false
  MoveWithHost = false
  Nodes = (2) [(-1.72563e-31,-1.42109e-15,-7.77156e-16),(1400,-1.42109e-15,-7.77156e-16)]
  NodesOffset = 0
  Normal = (0,0,0)
  PerimeterLength = 3100
  Placement = pos=(9085,3350,2800) rot=(0,0,1;0rad)
  PredefinedType = 0
  VerticalArea = 1240000
  Width = 150
FEATURE [Part::FeaturePython] Structure123  label="V15x40 V118"  # Arch/BIM 7 (typed FeaturePython)
  FaceMaker = 0
  Height = 400
  HorizontalArea = 195000
  IfcData = attributes={"GlobalId": {"name": "GlobalId", "type": "IfcGloballyUniqueId", "is_enum": false, "enum_values": []}, "Description": {"... (+475 chars omitted),+1 more (map truncated)
  IfcType = 7
  Length = 1300
  MoveBase = false
  MoveWithHost = false
  Nodes = (2) [(-1.72563e-31,-1.42109e-15,-7.77156e-16),(1300,-1.42109e-15,-7.77156e-16)]
  NodesOffset = 0
  Normal = (0,0,0)
  PerimeterLength = 2900
  Placement = pos=(9135,100,2800) rot=(0,0,1;0rad)
  PredefinedType = 0
  VerticalArea = 1160000
  Width = 150
FEATURE [Part::FeaturePython] Structure124  label="V15x40 V119"  # Arch/BIM 7 (typed FeaturePython)
  FaceMaker = 0
  Height = 400
  HorizontalArea = 445500
  IfcData = attributes={"GlobalId": {"name": "GlobalId", "type": "IfcGloballyUniqueId", "is_enum": false, "enum_values": []}, "Description": {"... (+475 chars omitted),+1 more (map truncated)
  IfcType = 7
  Length = 2970
  MoveBase = false
  MoveWithHost = false
  Nodes = (2) [(-1.72563e-31,-1.42109e-15,-7.77156e-16),(2970,-1.42109e-15,-7.77156e-16)]
  NodesOffset = 0
  Normal = (0,0,0)
  PerimeterLength = 6240
  Placement = pos=(10685,100,2800) rot=(0,0,1;0rad)
  PredefinedType = 0
  VerticalArea = 2.496e+06
  Width = 150
FEATURE [Part::FeaturePython] Structure125  label="V15x40 V115"  # Arch/BIM 7 (typed FeaturePython)
  FaceMaker = 0
  Height = 400
  HorizontalArea = 460500
  IfcData = attributes={"GlobalId": {"name": "GlobalId", "type": "IfcGloballyUniqueId", "is_enum": false, "enum_values": []}, "Description": {"... (+475 chars omitted),+1 more (map truncated)
  IfcType = 7
  Length = 3070
  MoveBase = false
  MoveWithHost = false
  Nodes = (2) [(-1.72563e-31,-1.42109e-15,-7.77156e-16),(3070,-1.42109e-15,-7.77156e-16)]
  NodesOffset = 0
  Normal = (0,0,0)
  PerimeterLength = 6440
  Placement = pos=(10635,3350,2800) rot=(0,0,1;0rad)
  PredefinedType = 0
  VerticalArea = 2.576e+06
  Width = 150
FEATURE [Part::FeaturePython] Structure126  label="V20x40 V133"  # Arch/BIM 7 (typed FeaturePython)
  FaceMaker = 0
  Height = 400
  HorizontalArea = 635000
  IfcData = attributes={"GlobalId": {"name": "GlobalId", "type": "IfcGloballyUniqueId", "is_enum": false, "enum_values": []}, "Description": {"... (+475 chars omitted),+1 more (map truncated)
  IfcType = 7
  Length = 3175
  MoveBase = false
  MoveWithHost = false
  Nodes = (2) [(-1.72563e-31,0,-7.77156e-16),(3175,0,-7.77156e-16)]
  NodesOffset = 0
  Normal = (0,0,0)
  PerimeterLength = 6750
  Placement = pos=(13780,175,2800) rot=(0,0,1;1.5708rad)
  PredefinedType = 0
  VerticalArea = 2.7e+06
  Width = 200
FEATURE [Part::FeaturePython] Structure127  label="V20x40 V134"  # Arch/BIM 7 (typed FeaturePython)
  FaceMaker = 0
  Height = 400
  HorizontalArea = 509000
  IfcData = attributes={"GlobalId": {"name": "GlobalId", "type": "IfcGloballyUniqueId", "is_enum": false, "enum_values": []}, "Description": {"... (+475 chars omitted),+1 more (map truncated)
  IfcType = 7
  Length = 2545
  MoveBase = false
  MoveWithHost = false
  Nodes = (2) [(-1.72563e-31,0,-7.77156e-16),(2545,0,-7.77156e-16)]
  NodesOffset = 0
  Normal = (0,0,0)
  PerimeterLength = 5490
  Placement = pos=(13780,3350,2800) rot=(0,0,1;1.5708rad)
  PredefinedType = 0
  VerticalArea = 2.196e+06
  Width = 200
FEATURE [Part::FeaturePython] Structure128  label="V20x40 V135"  # Arch/BIM 7 (typed FeaturePython)
  FaceMaker = 0
  Height = 400
  HorizontalArea = 756000
  IfcData = attributes={"GlobalId": {"name": "GlobalId", "type": "IfcGloballyUniqueId", "is_enum": false, "enum_values": []}, "Description": {"... (+475 chars omitted),+1 more (map truncated)
  IfcType = 7
  Length = 3780
  MoveBase = false
  MoveWithHost = false
  Nodes = (2) [(-1.72563e-31,0,-7.77156e-16),(3780,0,-7.77156e-16)]
  NodesOffset = 0
  Normal = (0,0,0)
  PerimeterLength = 7960
  Placement = pos=(15210,6045,2800) rot=(0,0,1;1.5708rad)
  PredefinedType = 0
  VerticalArea = 3.184e+06
  Width = 200
FEATURE [Part::FeaturePython] Structure129  label="V15x40 V109"  # Arch/BIM 7 (typed FeaturePython)
  FaceMaker = 0
  Height = 400
  HorizontalArea = 235500
  IfcData = attributes={"GlobalId": {"name": "GlobalId", "type": "IfcGloballyUniqueId", "is_enum": false, "enum_values": []}, "Description": {"... (+475 chars omitted),+1 more (map truncated)
  IfcType = 7
  Length = 1570
  MoveBase = false
  MoveWithHost = false
  Nodes = (2) [(-1.72563e-31,-1.42109e-15,-7.77156e-16),(1570,-1.42109e-15,-7.77156e-16)]
  NodesOffset = 0
  Normal = (0,0,0)
  PerimeterLength = 3440
  Placement = pos=(13655,5970,2800) rot=(0,0,1;3.14159rad)
  PredefinedType = 0
  VerticalArea = 1.376e+06
  Width = 150
FEATURE [Part::FeaturePython] Structure130  label="V15x40 V110"  # Arch/BIM 7 (typed FeaturePython)
  FaceMaker = 0
  Height = 400
  HorizontalArea = 177000
  IfcData = attributes={"GlobalId": {"name": "GlobalId", "type": "IfcGloballyUniqueId", "is_enum": false, "enum_values": []}, "Description": {"... (+475 chars omitted),+1 more (map truncated)
  IfcType = 7
  Length = 1180
  MoveBase = false
  MoveWithHost = false
  Nodes = (2) [(-1.72563e-31,-1.42109e-15,-7.77156e-16),(1180,-1.42109e-15,-7.77156e-16)]
  NodesOffset = 0
  Normal = (0,0,0)
  PerimeterLength = 2660
  Placement = pos=(13905,5970,2800) rot=(0,0,1;0rad)
  PredefinedType = 0
  VerticalArea = 1064000
  Width = 150
FEATURE [Part::FeaturePython] Structure131  label="V15x40 V125"  # Arch/BIM 7 (typed FeaturePython)
  FaceMaker = 0
  Height = 400
  HorizontalArea = 466500
  IfcData = attributes={"GlobalId": {"name": "GlobalId", "type": "IfcGloballyUniqueId", "is_enum": false, "enum_values": []}, "Description": {"... (+475 chars omitted),+1 more (map truncated)
  IfcType = 7
  Length = 3110
  MoveBase = false
  MoveWithHost = false
  Nodes = (2) [(-1.72563e-31,-1.42109e-15,-7.77156e-16),(3110,-1.42109e-15,-7.77156e-16)]
  NodesOffset = 0
  Normal = (0,0,0)
  PerimeterLength = 6520
  Placement = pos=(6160,9825,2800) rot=(0,0,-1;1.5708rad)
  PredefinedType = 0
  VerticalArea = 2.608e+06
  Width = 150
FEATURE [Part::FeaturePython] Structure132  label="V15x40 V124"  # Arch/BIM 7 (typed FeaturePython)
  FaceMaker = 0
  Height = 400
  HorizontalArea = 471000
  IfcData = attributes={"GlobalId": {"name": "GlobalId", "type": "IfcGloballyUniqueId", "is_enum": false, "enum_values": []}, "Description": {"... (+475 chars omitted),+1 more (map truncated)
  IfcType = 7
  Length = 3140
  MoveBase = false
  MoveWithHost = false
  Nodes = (2) [(-1.72563e-31,-1.42109e-15,-7.77156e-16),(3140,-1.42109e-15,-7.77156e-16)]
  NodesOffset = 0
  Normal = (0,0,0)
  PerimeterLength = 6580
  Placement = pos=(6160,6565,2800) rot=(0,0,-1;1.5708rad)
  PredefinedType = 0
  VerticalArea = 2.632e+06
  Width = 150
FEATURE [Part::FeaturePython] Structure133  label="V15x40 V123"  # Arch/BIM 7 (typed FeaturePython)
  FaceMaker = 0
  Height = 400
  HorizontalArea = 465000
  IfcData = attributes={"GlobalId": {"name": "GlobalId", "type": "IfcGloballyUniqueId", "is_enum": false, "enum_values": []}, "Description": {"... (+475 chars omitted),+1 more (map truncated)
  IfcType = 7
  Length = 3100
  MoveBase = false
  MoveWithHost = false
  Nodes = (2) [(-1.72563e-31,-1.42109e-15,-7.77156e-16),(3100,-1.42109e-15,-7.77156e-16)]
  NodesOffset = 0
  Normal = (0,0,0)
  PerimeterLength = 6500
  Placement = pos=(6160,3275,2800) rot=(0,0,-1;1.5708rad)
  PredefinedType = 0
  VerticalArea = 2.6e+06
  Width = 150
FEATURE [Part::FeaturePython] Structure134  label="V15x40 V128"  # Arch/BIM 7 (typed FeaturePython)
  FaceMaker = 0
  Height = 400
  HorizontalArea = 459000
  IfcData = attributes={"GlobalId": {"name": "GlobalId", "type": "IfcGloballyUniqueId", "is_enum": false, "enum_values": []}, "Description": {"... (+475 chars omitted),+1 more (map truncated)
  IfcType = 7
  Length = 3060
  MoveBase = false
  MoveWithHost = false
  Nodes = (2) [(-1.72563e-31,-1.42109e-15,-7.77156e-16),(3060,-1.42109e-15,-7.77156e-16)]
  NodesOffset = 0
  Normal = (0,0,0)
  PerimeterLength = 6420
  Placement = pos=(9010,9825,2800) rot=(0,0,-1;1.5708rad)
  PredefinedType = 0
  VerticalArea = 2.568e+06
  Width = 150
FEATURE [Part::FeaturePython] Structure135  label="V15x40 V127"  # Arch/BIM 7 (typed FeaturePython)
  FaceMaker = 0
  Height = 400
  HorizontalArea = 456000
  IfcData = attributes={"GlobalId": {"name": "GlobalId", "type": "IfcGloballyUniqueId", "is_enum": false, "enum_values": []}, "Description": {"... (+475 chars omitted),+1 more (map truncated)
  IfcType = 7
  Length = 3040
  MoveBase = false
  MoveWithHost = false
  Nodes = (2) [(-1.72563e-31,-1.42109e-15,-7.77156e-16),(3040,-1.42109e-15,-7.77156e-16)]
  NodesOffset = 0
  Normal = (0,0,0)
  PerimeterLength = 6380
  Placement = pos=(9010,6515,2800) rot=(0,0,-1;1.5708rad)
  PredefinedType = 0
  VerticalArea = 2.552e+06
  Width = 150
FEATURE [Part::FeaturePython] Structure136  label="V15x40 V126"  # Arch/BIM 7 (typed FeaturePython)
  FaceMaker = 0
  Height = 400
  HorizontalArea = 457500
  IfcData = attributes={"GlobalId": {"name": "GlobalId", "type": "IfcGloballyUniqueId", "is_enum": false, "enum_values": []}, "Description": {"... (+475 chars omitted),+1 more (map truncated)
  IfcType = 7
  Length = 3050
  MoveBase = false
  MoveWithHost = false
  Nodes = (2) [(-1.72563e-31,-1.42109e-15,-7.77156e-16),(3050,-1.42109e-15,-7.77156e-16)]
  NodesOffset = 0
  Normal = (0,0,0)
  PerimeterLength = 6400
  Placement = pos=(9010,3225,2800) rot=(0,0,-1;1.5708rad)
  PredefinedType = 0
  VerticalArea = 2.56e+06
  Width = 150
FEATURE [Part::FeaturePython] Structure137  label="V15x40 V132"  # Arch/BIM 7 (typed FeaturePython)
  FaceMaker = 0
  Height = 400
  HorizontalArea = 207000
  IfcData = attributes={"GlobalId": {"name": "GlobalId", "type": "IfcGloballyUniqueId", "is_enum": false, "enum_values": []}, "Description": {"... (+475 chars omitted),+1 more (map truncated)
  IfcType = 7
  Length = 1380
  MoveBase = false
  MoveWithHost = false
  Nodes = (2) [(-1.72563e-31,-1.42109e-15,-7.77156e-16),(1380,-1.42109e-15,-7.77156e-16)]
  NodesOffset = 0
  Normal = (0,0,0)
  PerimeterLength = 3060
  Placement = pos=(12010,9825,2800) rot=(0,0,-1;1.5708rad)
  PredefinedType = 0
  VerticalArea = 1.224e+06
  Width = 150
FEATURE [Part::FeaturePython] Structure138  label="V15x40 V131"  # Arch/BIM 7 (typed FeaturePython)
  FaceMaker = 0
  Height = 400
  HorizontalArea = 207000
  IfcData = attributes={"GlobalId": {"name": "GlobalId", "type": "IfcGloballyUniqueId", "is_enum": false, "enum_values": []}, "Description": {"... (+475 chars omitted),+1 more (map truncated)
  IfcType = 7
  Length = 1380
  MoveBase = false
  MoveWithHost = false
  Nodes = (2) [(-1.72563e-31,-1.42109e-15,-7.77156e-16),(1380,-1.42109e-15,-7.77156e-16)]
  NodesOffset = 0
  Normal = (0,0,0)
  PerimeterLength = 3060
  Placement = pos=(10560,8445,2800) rot=(0,0,1;1.5708rad)
  PredefinedType = 0
  VerticalArea = 1.224e+06
  Width = 150
FEATURE [Part::FeaturePython] Structure139  label="V15x40 V130"  # Arch/BIM 7 (typed FeaturePython)
  FaceMaker = 0
  Height = 400
  HorizontalArea = 363000
  IfcData = attributes={"GlobalId": {"name": "GlobalId", "type": "IfcGloballyUniqueId", "is_enum": false, "enum_values": []}, "Description": {"... (+475 chars omitted),+1 more (map truncated)
  IfcType = 7
  Length = 2420
  MoveBase = false
  MoveWithHost = false
  Nodes = (2) [(-1.72563e-31,-1.42109e-15,-7.77156e-16),(2420,-1.42109e-15,-7.77156e-16)]
  NodesOffset = 0
  Normal = (0,0,0)
  PerimeterLength = 5140
  Placement = pos=(10560,3475,2800) rot=(0,0,1;1.5708rad)
  PredefinedType = 0
  VerticalArea = 2.056e+06
  Width = 150
FEATURE [Part::FeaturePython] Structure140  label="V15x40 V129"  # Arch/BIM 7 (typed FeaturePython)
  FaceMaker = 0
  Height = 400
  HorizontalArea = 457500
  IfcData = attributes={"GlobalId": {"name": "GlobalId", "type": "IfcGloballyUniqueId", "is_enum": false, "enum_values": []}, "Description": {"... (+475 chars omitted),+1 more (map truncated)
  IfcType = 7
  Length = 3050
  MoveBase = false
  MoveWithHost = false
  Nodes = (2) [(-1.72563e-31,-1.42109e-15,-7.77156e-16),(3050,-1.42109e-15,-7.77156e-16)]
  NodesOffset = 0
  Normal = (0,0,0)
  PerimeterLength = 6400
  Placement = pos=(10560,3225,2800) rot=(0,0,-1;1.5708rad)
  PredefinedType = 0
  VerticalArea = 2.56e+06
  Width = 150
FEATURE [Part::FeaturePython] Structure141  label="V15x40 V105"  # Arch/BIM 7 (typed FeaturePython)
  FaceMaker = 0
  Height = 400
  HorizontalArea = 453750
  IfcData = attributes={"GlobalId": {"name": "GlobalId", "type": "IfcGloballyUniqueId", "is_enum": false, "enum_values": []}, "Description": {"... (+475 chars omitted),+1 more (map truncated)
  IfcType = 7
  Length = 3025
  MoveBase = false
  MoveWithHost = false
  Nodes = (2) [(-1.72563e-31,-1.42109e-15,-7.77156e-16),(3025,-1.42109e-15,-7.77156e-16)]
  NodesOffset = 0
  Normal = (0,0,0)
  PerimeterLength = 6350
  Placement = pos=(12085,8370,2800) rot=(0,0,1;0rad)
  PredefinedType = 0
  VerticalArea = 2.54e+06
  Width = 150
FEATURE [Part::FeaturePython] Structure142  label="V15x40 V133"  # Arch/BIM 7 (typed FeaturePython)
  FaceMaker = 0
  Height = 400
  HorizontalArea = 597000
  IfcData = attributes={"GlobalId": {"name": "GlobalId", "type": "IfcGloballyUniqueId", "is_enum": false, "enum_values": []}, "Description": {"... (+475 chars omitted),+1 more (map truncated)
  IfcType = 7
  Length = 3980
  MoveBase = false
  MoveWithHost = false
  Nodes = (2) [(-1.72563e-31,-1.42109e-15,-7.77156e-16),(3980,-1.42109e-15,-7.77156e-16)]
  NodesOffset = 0
  Normal = (0,0,0)
  PerimeterLength = 8260
  Placement = pos=(2055,9900,5800) rot=(0,0,1;0rad)
  PredefinedType = 0
  VerticalArea = 3.304e+06
  Width = 150
FEATURE [Part::FeaturePython] Structure143  label="V15x40 V134"  # Arch/BIM 7 (typed FeaturePython)
  FaceMaker = 0
  Height = 400
  HorizontalArea = 390000
  IfcData = attributes={"GlobalId": {"name": "GlobalId", "type": "IfcGloballyUniqueId", "is_enum": false, "enum_values": []}, "Description": {"... (+475 chars omitted),+1 more (map truncated)
  IfcType = 7
  Length = 2600
  MoveBase = false
  MoveWithHost = false
  Nodes = (2) [(-1.72563e-31,-1.42109e-15,-7.77156e-16),(2600,-1.42109e-15,-7.77156e-16)]
  NodesOffset = 0
  Normal = (0,0,0)
  PerimeterLength = 5500
  Placement = pos=(6285,9900,5800) rot=(0,0,1;0rad)
  PredefinedType = 0
  VerticalArea = 2200000
  Width = 150
FEATURE [Part::FeaturePython] Structure144  label="V15x40 V135"  # Arch/BIM 7 (typed FeaturePython)
  FaceMaker = 0
  Height = 400
  HorizontalArea = 412500
  IfcData = attributes={"GlobalId": {"name": "GlobalId", "type": "IfcGloballyUniqueId", "is_enum": false, "enum_values": []}, "Description": {"... (+475 chars omitted),+1 more (map truncated)
  IfcType = 7
  Length = 2750
  MoveBase = false
  MoveWithHost = false
  Nodes = (2) [(-1.72563e-31,-1.42109e-15,-7.77156e-16),(2750,-1.42109e-15,-7.77156e-16)]
  NodesOffset = 0
  Normal = (0,0,0)
  PerimeterLength = 5800
  Placement = pos=(9135,9900,5800) rot=(0,0,1;0rad)
  PredefinedType = 0
  VerticalArea = 2320000
  Width = 150
FEATURE [Part::FeaturePython] Structure145  label="V15x40 V136"  # Arch/BIM 7 (typed FeaturePython)
  FaceMaker = 0
  Height = 400
  HorizontalArea = 442500
  IfcData = attributes={"GlobalId": {"name": "GlobalId", "type": "IfcGloballyUniqueId", "is_enum": false, "enum_values": []}, "Description": {"... (+475 chars omitted),+1 more (map truncated)
  IfcType = 7
  Length = 2950
  MoveBase = false
  MoveWithHost = false
  Nodes = (2) [(-1.72563e-31,-1.42109e-15,-7.77156e-16),(2950,-1.42109e-15,-7.77156e-16)]
  NodesOffset = 0
  Normal = (0,0,0)
  PerimeterLength = 6200
  Placement = pos=(12135,9900,5800) rot=(0,0,1;0rad)
  PredefinedType = 0
  VerticalArea = 2.48e+06
  Width = 150
FEATURE [Part::FeaturePython] Structure146  label="V15x40 V137"  # Arch/BIM 7 (typed FeaturePython)
  FaceMaker = 0
  Height = 400
  HorizontalArea = 453750
  IfcData = attributes={"GlobalId": {"name": "GlobalId", "type": "IfcGloballyUniqueId", "is_enum": false, "enum_values": []}, "Description": {"... (+475 chars omitted),+1 more (map truncated)
  IfcType = 7
  Length = 3025
  MoveBase = false
  MoveWithHost = false
  Nodes = (2) [(-1.72563e-31,-1.42109e-15,-7.77156e-16),(3025,-1.42109e-15,-7.77156e-16)]
  NodesOffset = 0
  Normal = (0,0,0)
  PerimeterLength = 6350
  Placement = pos=(12085,8370,5800) rot=(0,0,1;0rad)
  PredefinedType = 0
  VerticalArea = 2.54e+06
  Width = 150
FEATURE [Part::FeaturePython] Structure147  label="V15x40 V138"  # Arch/BIM 7 (typed FeaturePython)
  FaceMaker = 0
  Height = 400
  HorizontalArea = 597000
  IfcData = attributes={"GlobalId": {"name": "GlobalId", "type": "IfcGloballyUniqueId", "is_enum": false, "enum_values": []}, "Description": {"... (+475 chars omitted),+1 more (map truncated)
  IfcType = 7
  Length = 3980
  MoveBase = false
  MoveWithHost = false
  Nodes = (2) [(-1.72563e-31,-1.42109e-15,-7.77156e-16),(3980,-1.42109e-15,-7.77156e-16)]
  NodesOffset = 0
  Normal = (0,0,0)
  PerimeterLength = 8260
  Placement = pos=(2055,6640,5800) rot=(0,0,1;0rad)
  PredefinedType = 0
  VerticalArea = 3.304e+06
  Width = 150
FEATURE [Part::FeaturePython] Structure148  label="V15x40 V139"  # Arch/BIM 7 (typed FeaturePython)
  FaceMaker = 0
  Height = 400
  HorizontalArea = 397500
  IfcData = attributes={"GlobalId": {"name": "GlobalId", "type": "IfcGloballyUniqueId", "is_enum": false, "enum_values": []}, "Description": {"... (+475 chars omitted),+1 more (map truncated)
  IfcType = 7
  Length = 2650
  MoveBase = false
  MoveWithHost = false
  Nodes = (2) [(-1.72563e-31,-1.42109e-15,-7.77156e-16),(2650,-1.42109e-15,-7.77156e-16)]
  NodesOffset = 0
  Normal = (0,0,0)
  PerimeterLength = 5600
  Placement = pos=(6285,6640,5800) rot=(0,0,1;0rad)
  PredefinedType = 0
  VerticalArea = 2240000
  Width = 150
FEATURE [Part::FeaturePython] Structure149  label="V15x40 V140"  # Arch/BIM 7 (typed FeaturePython)
  FaceMaker = 0
  Height = 400
  HorizontalArea = 210000
  IfcData = attributes={"GlobalId": {"name": "GlobalId", "type": "IfcGloballyUniqueId", "is_enum": false, "enum_values": []}, "Description": {"... (+475 chars omitted),+1 more (map truncated)
  IfcType = 7
  Length = 1400
  MoveBase = false
  MoveWithHost = false
  Nodes = (2) [(-1.72563e-31,-1.42109e-15,-7.77156e-16),(1400,-1.42109e-15,-7.77156e-16)]
  NodesOffset = 0
  Normal = (0,0,0)
  PerimeterLength = 3100
  Placement = pos=(9085,6640,5800) rot=(0,0,1;0rad)
  PredefinedType = 0
  VerticalArea = 1240000
  Width = 150
FEATURE [Part::FeaturePython] Structure150  label="V15x40 V141"  # Arch/BIM 7 (typed FeaturePython)
  FaceMaker = 0
  Height = 400
  HorizontalArea = 235500
  IfcData = attributes={"GlobalId": {"name": "GlobalId", "type": "IfcGloballyUniqueId", "is_enum": false, "enum_values": []}, "Description": {"... (+475 chars omitted),+1 more (map truncated)
  IfcType = 7
  Length = 1570
  MoveBase = false
  MoveWithHost = false
  Nodes = (2) [(-1.72563e-31,-1.42109e-15,-7.77156e-16),(1570,-1.42109e-15,-7.77156e-16)]
  NodesOffset = 0
  Normal = (0,0,0)
  PerimeterLength = 3440
  Placement = pos=(13655,5970,5800) rot=(0,0,1;3.14159rad)
  PredefinedType = 0
  VerticalArea = 1.376e+06
  Width = 150
FEATURE [Part::FeaturePython] Structure151  label="V15x40 V142"  # Arch/BIM 7 (typed FeaturePython)
  FaceMaker = 0
  Height = 400
  HorizontalArea = 177000
  IfcData = attributes={"GlobalId": {"name": "GlobalId", "type": "IfcGloballyUniqueId", "is_enum": false, "enum_values": []}, "Description": {"... (+475 chars omitted),+1 more (map truncated)
  IfcType = 7
  Length = 1180
  MoveBase = false
  MoveWithHost = false
  Nodes = (2) [(-1.72563e-31,-1.42109e-15,-7.77156e-16),(1180,-1.42109e-15,-7.77156e-16)]
  NodesOffset = 0
  Normal = (0,0,0)
  PerimeterLength = 2660
  Placement = pos=(13905,5970,5800) rot=(0,0,1;0rad)
  PredefinedType = 0
  VerticalArea = 1064000
  Width = 150
FEATURE [Part::FeaturePython] Structure152  label="V15x40 V143"  # Arch/BIM 7 (typed FeaturePython)
  FaceMaker = 0
  Height = 400
  HorizontalArea = 597000
  IfcData = attributes={"GlobalId": {"name": "GlobalId", "type": "IfcGloballyUniqueId", "is_enum": false, "enum_values": []}, "Description": {"... (+475 chars omitted),+1 more (map truncated)
  IfcType = 7
  Length = 3980
  MoveBase = false
  MoveWithHost = false
  Nodes = (2) [(-1.72563e-31,-1.42109e-15,-7.77156e-16),(3980,-1.42109e-15,-7.77156e-16)]
  NodesOffset = 0
  Normal = (0,0,0)
  PerimeterLength = 8260
  Placement = pos=(2055,3350,5800) rot=(0,0,1;0rad)
  PredefinedType = 0
  VerticalArea = 3.304e+06
  Width = 150
FEATURE [Part::FeaturePython] Structure153  label="V15x40 V144"  # Arch/BIM 7 (typed FeaturePython)
  FaceMaker = 0
  Height = 400
  HorizontalArea = 397500
  IfcData = attributes={"GlobalId": {"name": "GlobalId", "type": "IfcGloballyUniqueId", "is_enum": false, "enum_values": []}, "Description": {"... (+475 chars omitted),+1 more (map truncated)
  IfcType = 7
  Length = 2650
  MoveBase = false
  MoveWithHost = false
  Nodes = (2) [(-1.72563e-31,-1.42109e-15,-7.77156e-16),(2650,-1.42109e-15,-7.77156e-16)]
  NodesOffset = 0
  Normal = (0,0,0)
  PerimeterLength = 5600
  Placement = pos=(6285,3350,5800) rot=(0,0,1;0rad)
  PredefinedType = 0
  VerticalArea = 2240000
  Width = 150
FEATURE [Part::FeaturePython] Structure154  label="V15x40 V145"  # Arch/BIM 7 (typed FeaturePython)
  FaceMaker = 0
  Height = 400
  HorizontalArea = 210000
  IfcData = attributes={"GlobalId": {"name": "GlobalId", "type": "IfcGloballyUniqueId", "is_enum": false, "enum_values": []}, "Description": {"... (+475 chars omitted),+1 more (map truncated)
  IfcType = 7
  Length = 1400
  MoveBase = false
  MoveWithHost = false
  Nodes = (2) [(-1.72563e-31,-1.42109e-15,-7.77156e-16),(1400,-1.42109e-15,-7.77156e-16)]
  NodesOffset = 0
  Normal = (0,0,0)
  PerimeterLength = 3100
  Placement = pos=(9085,3350,5800) rot=(0,0,1;0rad)
  PredefinedType = 0
  VerticalArea = 1240000
  Width = 150
FEATURE [Part::FeaturePython] Structure155  label="V15x40 V146"  # Arch/BIM 7 (typed FeaturePython)
  FaceMaker = 0
  Height = 400
  HorizontalArea = 460500
  IfcData = attributes={"GlobalId": {"name": "GlobalId", "type": "IfcGloballyUniqueId", "is_enum": false, "enum_values": []}, "Description": {"... (+475 chars omitted),+1 more (map truncated)
  IfcType = 7
  Length = 3070
  MoveBase = false
  MoveWithHost = false
  Nodes = (2) [(-1.72563e-31,-1.42109e-15,-7.77156e-16),(3070,-1.42109e-15,-7.77156e-16)]
  NodesOffset = 0
  Normal = (0,0,0)
  PerimeterLength = 6440
  Placement = pos=(10635,3350,5800) rot=(0,0,1;0rad)
  PredefinedType = 0
  VerticalArea = 2.576e+06
  Width = 150
FEATURE [Part::FeaturePython] Structure156  label="V15x40 V147"  # Arch/BIM 7 (typed FeaturePython)
  FaceMaker = 0
  Height = 400
  HorizontalArea = 597000
  IfcData = attributes={"GlobalId": {"name": "GlobalId", "type": "IfcGloballyUniqueId", "is_enum": false, "enum_values": []}, "Description": {"... (+475 chars omitted),+1 more (map truncated)
  IfcType = 7
  Length = 3980
  MoveBase = false
  MoveWithHost = false
  Nodes = (2) [(-1.72563e-31,-1.42109e-15,-7.77156e-16),(3980,-1.42109e-15,-7.77156e-16)]
  NodesOffset = 0
  Normal = (0,0,0)
  PerimeterLength = 8260
  Placement = pos=(2055,100,5800) rot=(0,0,1;0rad)
  PredefinedType = 0
  VerticalArea = 3.304e+06
  Width = 150
FEATURE [Part::FeaturePython] Structure157  label="V15x40 V148"  # Arch/BIM 7 (typed FeaturePython)
  FaceMaker = 0
  Height = 400
  HorizontalArea = 390000
  IfcData = attributes={"GlobalId": {"name": "GlobalId", "type": "IfcGloballyUniqueId", "is_enum": false, "enum_values": []}, "Description": {"... (+475 chars omitted),+1 more (map truncated)
  IfcType = 7
  Length = 2600
  MoveBase = false
  MoveWithHost = false
  Nodes = (2) [(-1.72563e-31,-1.42109e-15,-7.77156e-16),(2600,-1.42109e-15,-7.77156e-16)]
  NodesOffset = 0
  Normal = (0,0,0)
  PerimeterLength = 5500
  Placement = pos=(6285,100,5800) rot=(0,0,1;0rad)
  PredefinedType = 0
  VerticalArea = 2200000
  Width = 150
FEATURE [Part::FeaturePython] Structure158  label="V15x40 V149"  # Arch/BIM 7 (typed FeaturePython)
  FaceMaker = 0
  Height = 400
  HorizontalArea = 195000
  IfcData = attributes={"GlobalId": {"name": "GlobalId", "type": "IfcGloballyUniqueId", "is_enum": false, "enum_values": []}, "Description": {"... (+475 chars omitted),+1 more (map truncated)
  IfcType = 7
  Length = 1300
  MoveBase = false
  MoveWithHost = false
  Nodes = (2) [(-1.72563e-31,-1.42109e-15,-7.77156e-16),(1300,-1.42109e-15,-7.77156e-16)]
  NodesOffset = 0
  Normal = (0,0,0)
  PerimeterLength = 2900
  Placement = pos=(9135,100,5800) rot=(0,0,1;0rad)
  PredefinedType = 0
  VerticalArea = 1160000
  Width = 150
FEATURE [Part::FeaturePython] Structure159  label="V15x40 V150"  # Arch/BIM 7 (typed FeaturePython)
  FaceMaker = 0
  Height = 400
  HorizontalArea = 445500
  IfcData = attributes={"GlobalId": {"name": "GlobalId", "type": "IfcGloballyUniqueId", "is_enum": false, "enum_values": []}, "Description": {"... (+475 chars omitted),+1 more (map truncated)
  IfcType = 7
  Length = 2970
  MoveBase = false
  MoveWithHost = false
  Nodes = (2) [(-1.72563e-31,-1.42109e-15,-7.77156e-16),(2970,-1.42109e-15,-7.77156e-16)]
  NodesOffset = 0
  Normal = (0,0,0)
  PerimeterLength = 6240
  Placement = pos=(10685,100,5800) rot=(0,0,1;0rad)
  PredefinedType = 0
  VerticalArea = 2.496e+06
  Width = 150
FEATURE [Part::FeaturePython] Structure160  label="V15x40 V151"  # Arch/BIM 7 (typed FeaturePython)
  FaceMaker = 0
  Height = 400
  HorizontalArea = 465000
  IfcData = attributes={"GlobalId": {"name": "GlobalId", "type": "IfcGloballyUniqueId", "is_enum": false, "enum_values": []}, "Description": {"... (+475 chars omitted),+1 more (map truncated)
  IfcType = 7
  Length = 3100
  MoveBase = false
  MoveWithHost = false
  Nodes = (2) [(-1.72563e-31,-1.42109e-15,-7.77156e-16),(3100,-1.42109e-15,-7.77156e-16)]
  NodesOffset = 0
  Normal = (0,0,0)
  PerimeterLength = 6500
  Placement = pos=(6160,3275,5800) rot=(0,0,-1;1.5708rad)
  PredefinedType = 0
  VerticalArea = 2.6e+06
  Width = 150
FEATURE [Part::FeaturePython] Structure161  label="V15x40 V152"  # Arch/BIM 7 (typed FeaturePython)
  FaceMaker = 0
  Height = 400
  HorizontalArea = 471000
  IfcData = attributes={"GlobalId": {"name": "GlobalId", "type": "IfcGloballyUniqueId", "is_enum": false, "enum_values": []}, "Description": {"... (+475 chars omitted),+1 more (map truncated)
  IfcType = 7
  Length = 3140
  MoveBase = false
  MoveWithHost = false
  Nodes = (2) [(-1.72563e-31,-1.42109e-15,-7.77156e-16),(3140,-1.42109e-15,-7.77156e-16)]
  NodesOffset = 0
  Normal = (0,0,0)
  PerimeterLength = 6580
  Placement = pos=(6160,6565,5800) rot=(0,0,-1;1.5708rad)
  PredefinedType = 0
  VerticalArea = 2.632e+06
  Width = 150
FEATURE [Part::FeaturePython] Structure162  label="V15x40 V153"  # Arch/BIM 7 (typed FeaturePython)
  FaceMaker = 0
  Height = 400
  HorizontalArea = 466500
  IfcData = attributes={"GlobalId": {"name": "GlobalId", "type": "IfcGloballyUniqueId", "is_enum": false, "enum_values": []}, "Description": {"... (+475 chars omitted),+1 more (map truncated)
  IfcType = 7
  Length = 3110
  MoveBase = false
  MoveWithHost = false
  Nodes = (2) [(-1.72563e-31,-1.42109e-15,-7.77156e-16),(3110,-1.42109e-15,-7.77156e-16)]
  NodesOffset = 0
  Normal = (0,0,0)
  PerimeterLength = 6520
  Placement = pos=(6160,9825,5800) rot=(0,0,-1;1.5708rad)
  PredefinedType = 0
  VerticalArea = 2.608e+06
  Width = 150
FEATURE [Part::FeaturePython] Structure163  label="V15x40 V154"  # Arch/BIM 7 (typed FeaturePython)
  FaceMaker = 0
  Height = 400
  HorizontalArea = 457500
  IfcData = attributes={"GlobalId": {"name": "GlobalId", "type": "IfcGloballyUniqueId", "is_enum": false, "enum_values": []}, "Description": {"... (+475 chars omitted),+1 more (map truncated)
  IfcType = 7
  Length = 3050
  MoveBase = false
  MoveWithHost = false
  Nodes = (2) [(-1.72563e-31,-1.42109e-15,-7.77156e-16),(3050,-1.42109e-15,-7.77156e-16)]
  NodesOffset = 0
  Normal = (0,0,0)
  PerimeterLength = 6400
  Placement = pos=(9010,3225,5800) rot=(0,0,-1;1.5708rad)
  PredefinedType = 0
  VerticalArea = 2.56e+06
  Width = 150
FEATURE [Part::FeaturePython] Structure164  label="V15x40 V155"  # Arch/BIM 7 (typed FeaturePython)
  FaceMaker = 0
  Height = 400
  HorizontalArea = 456000
  IfcData = attributes={"GlobalId": {"name": "GlobalId", "type": "IfcGloballyUniqueId", "is_enum": false, "enum_values": []}, "Description": {"... (+475 chars omitted),+1 more (map truncated)
  IfcType = 7
  Length = 3040
  MoveBase = false
  MoveWithHost = false
  Nodes = (2) [(-1.72563e-31,-1.42109e-15,-7.77156e-16),(3040,-1.42109e-15,-7.77156e-16)]
  NodesOffset = 0
  Normal = (0,0,0)
  PerimeterLength = 6380
  Placement = pos=(9010,6515,5800) rot=(0,0,-1;1.5708rad)
  PredefinedType = 0
  VerticalArea = 2.552e+06
  Width = 150
FEATURE [Part::FeaturePython] Structure165  label="V15x40 V156"  # Arch/BIM 7 (typed FeaturePython)
  FaceMaker = 0
  Height = 400
  HorizontalArea = 459000
  IfcData = attributes={"GlobalId": {"name": "GlobalId", "type": "IfcGloballyUniqueId", "is_enum": false, "enum_values": []}, "Description": {"... (+475 chars omitted),+1 more (map truncated)
  IfcType = 7
  Length = 3060
  MoveBase = false
  MoveWithHost = false
  Nodes = (2) [(-1.72563e-31,-1.42109e-15,-7.77156e-16),(3060,-1.42109e-15,-7.77156e-16)]
  NodesOffset = 0
  Normal = (0,0,0)
  PerimeterLength = 6420
  Placement = pos=(9010,9825,5800) rot=(0,0,-1;1.5708rad)
  PredefinedType = 0
  VerticalArea = 2.568e+06
  Width = 150
FEATURE [Part::FeaturePython] Structure166  label="V15x40 V157"  # Arch/BIM 7 (typed FeaturePython)
  FaceMaker = 0
  Height = 400
  HorizontalArea = 457500
  IfcData = attributes={"GlobalId": {"name": "GlobalId", "type": "IfcGloballyUniqueId", "is_enum": false, "enum_values": []}, "Description": {"... (+475 chars omitted),+1 more (map truncated)
  IfcType = 7
  Length = 3050
  MoveBase = false
  MoveWithHost = false
  Nodes = (2) [(-1.72563e-31,-1.42109e-15,-7.77156e-16),(3050,-1.42109e-15,-7.77156e-16)]
  NodesOffset = 0
  Normal = (0,0,0)
  PerimeterLength = 6400
  Placement = pos=(10560,3225,5800) rot=(0,0,-1;1.5708rad)
  PredefinedType = 0
  VerticalArea = 2.56e+06
  Width = 150
FEATURE [Part::FeaturePython] Structure167  label="V15x40 V158"  # Arch/BIM 7 (typed FeaturePython)
  FaceMaker = 0
  Height = 400
  HorizontalArea = 363000
  IfcData = attributes={"GlobalId": {"name": "GlobalId", "type": "IfcGloballyUniqueId", "is_enum": false, "enum_values": []}, "Description": {"... (+475 chars omitted),+1 more (map truncated)
  IfcType = 7
  Length = 2420
  MoveBase = false
  MoveWithHost = false
  Nodes = (2) [(-1.72563e-31,-1.42109e-15,-7.77156e-16),(2420,-1.42109e-15,-7.77156e-16)]
  NodesOffset = 0
  Normal = (0,0,0)
  PerimeterLength = 5140
  Placement = pos=(10560,3475,5800) rot=(0,0,1;1.5708rad)
  PredefinedType = 0
  VerticalArea = 2056000
  Width = 150
FEATURE [Part::FeaturePython] Structure168  label="V15x40 V159"  # Arch/BIM 7 (typed FeaturePython)
  FaceMaker = 0
  Height = 400
  HorizontalArea = 207000
  IfcData = attributes={"GlobalId": {"name": "GlobalId", "type": "IfcGloballyUniqueId", "is_enum": false, "enum_values": []}, "Description": {"... (+475 chars omitted),+1 more (map truncated)
  IfcType = 7
  Length = 1380
  MoveBase = false
  MoveWithHost = false
  Nodes = (2) [(-1.72563e-31,-1.42109e-15,-7.77156e-16),(1380,-1.42109e-15,-7.77156e-16)]
  NodesOffset = 0
  Normal = (0,0,0)
  PerimeterLength = 3060
  Placement = pos=(10560,8445,5800) rot=(0,0,1;1.5708rad)
  PredefinedType = 0
  VerticalArea = 1224000
  Width = 150
FEATURE [Part::FeaturePython] Structure169  label="V15x40 V160"  # Arch/BIM 7 (typed FeaturePython)
  FaceMaker = 0
  Height = 400
  HorizontalArea = 207000
  IfcData = attributes={"GlobalId": {"name": "GlobalId", "type": "IfcGloballyUniqueId", "is_enum": false, "enum_values": []}, "Description": {"... (+475 chars omitted),+1 more (map truncated)
  IfcType = 7
  Length = 1380
  MoveBase = false
  MoveWithHost = false
  Nodes = (2) [(-1.72563e-31,-1.42109e-15,-7.77156e-16),(1380,-1.42109e-15,-7.77156e-16)]
  NodesOffset = 0
  Normal = (0,0,0)
  PerimeterLength = 3060
  Placement = pos=(12010,9825,5800) rot=(0,0,-1;1.5708rad)
  PredefinedType = 0
  VerticalArea = 1224000
  Width = 150
FEATURE [Part::FeaturePython] Structure170  label="V20x40 V136"  # Arch/BIM 7 (typed FeaturePython)
  FaceMaker = 0
  Height = 400
  HorizontalArea = 615000
  IfcData = attributes={"GlobalId": {"name": "GlobalId", "type": "IfcGloballyUniqueId", "is_enum": false, "enum_values": []}, "Description": {"... (+475 chars omitted),+1 more (map truncated)
  IfcType = 7
  Length = 3075
  MoveBase = false
  MoveWithHost = false
  Nodes = (2) [(-1.72563e-31,0,-7.77156e-16),(3075,0,-7.77156e-16)]
  NodesOffset = 0
  Normal = (0,0,0)
  PerimeterLength = 6550
  Placement = pos=(1930,3250,5800) rot=(0,0,-1;1.5708rad)
  PredefinedType = 0
  VerticalArea = 2.62e+06
  Width = 200
FEATURE [Part::FeaturePython] Structure171  label="V20x40 V137"  # Arch/BIM 7 (typed FeaturePython)
  FaceMaker = 0
  Height = 400
  HorizontalArea = 618000
  IfcData = attributes={"GlobalId": {"name": "GlobalId", "type": "IfcGloballyUniqueId", "is_enum": false, "enum_values": []}, "Description": {"... (+475 chars omitted),+1 more (map truncated)
  IfcType = 7
  Length = 3090
  MoveBase = false
  MoveWithHost = false
  Nodes = (2) [(-1.72563e-31,0,-7.77156e-16),(3090,0,-7.77156e-16)]
  NodesOffset = 0
  Normal = (0,0,0)
  PerimeterLength = 6580
  Placement = pos=(1930,6540,5800) rot=(0,0,-1;1.5708rad)
  PredefinedType = 0
  VerticalArea = 2.632e+06
  Width = 200
FEATURE [Part::FeaturePython] Structure172  label="V20x40 V138"  # Arch/BIM 7 (typed FeaturePython)
  FaceMaker = 0
  Height = 400
  HorizontalArea = 617000
  IfcData = attributes={"GlobalId": {"name": "GlobalId", "type": "IfcGloballyUniqueId", "is_enum": false, "enum_values": []}, "Description": {"... (+475 chars omitted),+1 more (map truncated)
  IfcType = 7
  Length = 3085
  MoveBase = false
  MoveWithHost = false
  Nodes = (2) [(-1.72563e-31,0,-7.77156e-16),(3085,0,-7.77156e-16)]
  NodesOffset = 0
  Normal = (0,0,0)
  PerimeterLength = 6570
  Placement = pos=(1930,9825,5800) rot=(0,0,-1;1.5708rad)
  PredefinedType = 0
  VerticalArea = 2.628e+06
  Width = 200
FEATURE [Part::FeaturePython] Structure173  label="V20x40 V139"  # Arch/BIM 7 (typed FeaturePython)
  FaceMaker = 0
  Height = 400
  HorizontalArea = 635000
  IfcData = attributes={"GlobalId": {"name": "GlobalId", "type": "IfcGloballyUniqueId", "is_enum": false, "enum_values": []}, "Description": {"... (+475 chars omitted),+1 more (map truncated)
  IfcType = 7
  Length = 3175
  MoveBase = false
  MoveWithHost = false
  Nodes = (2) [(-1.72563e-31,0,-7.77156e-16),(3175,0,-7.77156e-16)]
  NodesOffset = 0
  Normal = (0,0,0)
  PerimeterLength = 6750
  Placement = pos=(13780,175,5800) rot=(0,0,1;1.5708rad)
  PredefinedType = 0
  VerticalArea = 2.7e+06
  Width = 200
FEATURE [Part::FeaturePython] Structure174  label="V20x40 V140"  # Arch/BIM 7 (typed FeaturePython)
  FaceMaker = 0
  Height = 400
  HorizontalArea = 509000
  IfcData = attributes={"GlobalId": {"name": "GlobalId", "type": "IfcGloballyUniqueId", "is_enum": false, "enum_values": []}, "Description": {"... (+475 chars omitted),+1 more (map truncated)
  IfcType = 7
  Length = 2545
  MoveBase = false
  MoveWithHost = false
  Nodes = (2) [(-1.72563e-31,0,-7.77156e-16),(2545,0,-7.77156e-16)]
  NodesOffset = 0
  Normal = (0,0,0)
  PerimeterLength = 5490
  Placement = pos=(13780,3350,5800) rot=(0,0,1;1.5708rad)
  PredefinedType = 0
  VerticalArea = 2196000
  Width = 200
FEATURE [Part::FeaturePython] Structure175  label="V20x40 V141"  # Arch/BIM 7 (typed FeaturePython)
  FaceMaker = 0
  Height = 400
  HorizontalArea = 756000
  IfcData = attributes={"GlobalId": {"name": "GlobalId", "type": "IfcGloballyUniqueId", "is_enum": false, "enum_values": []}, "Description": {"... (+475 chars omitted),+1 more (map truncated)
  IfcType = 7
  Length = 3780
  MoveBase = false
  MoveWithHost = false
  Nodes = (2) [(-1.72563e-31,0,-7.77156e-16),(3780,0,-7.77156e-16)]
  NodesOffset = 0
  Normal = (0,0,0)
  PerimeterLength = 7960
  Placement = pos=(15210,6045,5800) rot=(0,0,1;1.5708rad)
  PredefinedType = 0
  VerticalArea = 3.184e+06
  Width = 200
FEATURE [Part::FeaturePython] Structure176  label="25x15 C026"  # Arch/BIM 24 (typed FeaturePython)
  FaceMaker = 0
  Height = 3000
  HorizontalArea = 37500
  IfcData = attributes={"GlobalId": {"name": "GlobalId", "type": "IfcGloballyUniqueId", "is_enum": false, "enum_values": []}, "Description": {"... (+438 chars omitted),+1 more (map truncated)
  IfcType = 24
  Length = 250
  MoveBase = false
  MoveWithHost = false
  Nodes = (2) [(-1.05471e-15,1.36424e-15,0),(-1.05471e-15,1.36424e-15,3000)]
  NodesOffset = 0
  Normal = (0,0,0)
  PerimeterLength = 800
  Placement = pos=(1930,9900,3000) rot=(0,0,1;0rad)
  PredefinedType = 0
  VerticalArea = 2400000
  Width = 150
FEATURE [Part::FeaturePython] Structure177  label="25x15 C027"  # Arch/BIM 172 (typed FeaturePython)
  FaceMaker = 0
  Height = 3000
  HorizontalArea = 37500
  IfcData = attributes={"GlobalId": {"name": "GlobalId", "type": "IfcGloballyUniqueId", "is_enum": false, "enum_values": []}, "Description": {"... (+484 chars omitted),+1 more (map truncated)
  IfcType = 172
  Length = 250
  MoveBase = false
  MoveWithHost = false
  Nodes = (2) [(-1.05471e-15,1.36424e-15,0),(-1.05471e-15,1.36424e-15,3000)]
  NodesOffset = 0
  Normal = (0,0,0)
  PerimeterLength = 800
  Placement = pos=(1930,100,3000) rot=(0,0,1;0rad)
  PredefinedType = 0
  VerticalArea = 2400000
  Width = 150
FEATURE [Part::FeaturePython] Structure178  label="25x20 C008"  # Arch/BIM 24 (typed FeaturePython)
  FaceMaker = 0
  Height = 3000
  HorizontalArea = 50000
  IfcData = attributes={"GlobalId": {"name": "GlobalId", "type": "IfcGloballyUniqueId", "is_enum": false, "enum_values": []}, "Description": {"... (+438 chars omitted),+1 more (map truncated)
  IfcType = 24
  Length = 250
  MoveBase = false
  MoveWithHost = false
  Nodes = (2) [(-1.05471e-15,-1.81899e-15,0),(-1.05471e-15,-1.81899e-15,3000)]
  NodesOffset = 0
  Normal = (0,0,0)
  PerimeterLength = 900
  Placement = pos=(1930,6640,3000) rot=(0,0,1;0rad)
  PredefinedType = 0
  VerticalArea = 2700000
  Width = 200
FEATURE [Part::FeaturePython] Structure180  label="25x15 C028"  # Arch/BIM 24 (typed FeaturePython)
  FaceMaker = 0
  Height = 3000
  HorizontalArea = 37500
  IfcData = attributes={"GlobalId": {"name": "GlobalId", "type": "IfcGloballyUniqueId", "is_enum": false, "enum_values": []}, "Description": {"... (+438 chars omitted),+1 more (map truncated)
  IfcType = 24
  Length = 250
  MoveBase = false
  MoveWithHost = false
  Nodes = (2) [(-1.05471e-15,1.36424e-15,0),(-1.05471e-15,1.36424e-15,3000)]
  NodesOffset = 0
  Normal = (0,0,0)
  PerimeterLength = 800
  Placement = pos=(6160,6640,3000) rot=(0,0,1;0rad)
  PredefinedType = 0
  VerticalArea = 2400000
  Width = 150
FEATURE [Part::FeaturePython] Structure181  label="25x15 C029"  # Arch/BIM 24 (typed FeaturePython)
  FaceMaker = 0
  Height = 3000
  HorizontalArea = 37500
  IfcData = attributes={"GlobalId": {"name": "GlobalId", "type": "IfcGloballyUniqueId", "is_enum": false, "enum_values": []}, "Description": {"... (+438 chars omitted),+1 more (map truncated)
  IfcType = 24
  Length = 250
  MoveBase = false
  MoveWithHost = false
  Nodes = (2) [(-1.05471e-15,1.36424e-15,0),(-1.05471e-15,1.36424e-15,3000)]
  NodesOffset = 0
  Normal = (0,0,0)
  PerimeterLength = 800
  Placement = pos=(6160,3350,3000) rot=(0,0,1;0rad)
  PredefinedType = 0
  VerticalArea = 2400000
  Width = 150
FEATURE [Part::FeaturePython] Structure182  label="25x15 C030"  # Arch/BIM 24 (typed FeaturePython)
  FaceMaker = 0
  Height = 3000
  HorizontalArea = 37500
  IfcData = attributes={"GlobalId": {"name": "GlobalId", "type": "IfcGloballyUniqueId", "is_enum": false, "enum_values": []}, "Description": {"... (+438 chars omitted),+1 more (map truncated)
  IfcType = 24
  Length = 250
  MoveBase = false
  MoveWithHost = false
  Nodes = (2) [(-1.05471e-15,1.36424e-15,0),(-1.05471e-15,1.36424e-15,3000)]
  NodesOffset = 0
  Normal = (0,0,0)
  PerimeterLength = 800
  Placement = pos=(6160,100,3000) rot=(0,0,1;0rad)
  PredefinedType = 0
  VerticalArea = 2400000
  Width = 150
FEATURE [Part::FeaturePython] Structure183  label="25x15 C031"  # Arch/BIM 24 (typed FeaturePython)
  FaceMaker = 0
  Height = 3000
  HorizontalArea = 37500
  IfcData = attributes={"GlobalId": {"name": "GlobalId", "type": "IfcGloballyUniqueId", "is_enum": false, "enum_values": []}, "Description": {"... (+438 chars omitted),+1 more (map truncated)
  IfcType = 24
  Length = 250
  MoveBase = false
  MoveWithHost = false
  Nodes = (2) [(-1.05471e-15,1.36424e-15,0),(-1.05471e-15,1.36424e-15,3000)]
  NodesOffset = 0
  Normal = (0,0,0)
  PerimeterLength = 800
  Placement = pos=(9010,100,3000) rot=(0,0,1;0rad)
  PredefinedType = 0
  VerticalArea = 2400000
  Width = 150
FEATURE [Part::FeaturePython] Structure184  label="25x15 C032"  # Arch/BIM 24 (typed FeaturePython)
  FaceMaker = 0
  Height = 3000
  HorizontalArea = 37500
  IfcData = attributes={"GlobalId": {"name": "GlobalId", "type": "IfcGloballyUniqueId", "is_enum": false, "enum_values": []}, "Description": {"... (+438 chars omitted),+1 more (map truncated)
  IfcType = 24
  Length = 250
  MoveBase = false
  MoveWithHost = false
  Nodes = (2) [(-1.05471e-15,1.36424e-15,0),(-1.05471e-15,1.36424e-15,3000)]
  NodesOffset = 0
  Normal = (0,0,0)
  PerimeterLength = 800
  Placement = pos=(10560,100,3000) rot=(0,0,1;0rad)
  PredefinedType = 0
  VerticalArea = 2400000
  Width = 150
FEATURE [Part::FeaturePython] Structure185  label="25x15 C033"  # Arch/BIM 24 (typed FeaturePython)
  FaceMaker = 0
  Height = 3000
  HorizontalArea = 37500
  IfcData = attributes={"GlobalId": {"name": "GlobalId", "type": "IfcGloballyUniqueId", "is_enum": false, "enum_values": []}, "Description": {"... (+438 chars omitted),+1 more (map truncated)
  IfcType = 24
  Length = 250
  MoveBase = false
  MoveWithHost = false
  Nodes = (2) [(-1.05471e-15,1.36424e-15,0),(-1.05471e-15,1.36424e-15,3000)]
  NodesOffset = 0
  Normal = (0,0,0)
  PerimeterLength = 800
  Placement = pos=(13780,100,3000) rot=(0,0,1;0rad)
  PredefinedType = 0
  VerticalArea = 2400000
  Width = 150
FEATURE [Part::FeaturePython] Structure186  label="25x15 C034"  # Arch/BIM 24 (typed FeaturePython)
  FaceMaker = 0
  Height = 3000
  HorizontalArea = 37500
  IfcData = attributes={"GlobalId": {"name": "GlobalId", "type": "IfcGloballyUniqueId", "is_enum": false, "enum_values": []}, "Description": {"... (+438 chars omitted),+1 more (map truncated)
  IfcType = 24
  Length = 250
  MoveBase = false
  MoveWithHost = false
  Nodes = (2) [(-1.05471e-15,1.36424e-15,0),(-1.05471e-15,1.36424e-15,3000)]
  NodesOffset = 0
  Normal = (0,0,0)
  PerimeterLength = 800
  Placement = pos=(15210,5970,3000) rot=(0,0,1;0rad)
  PredefinedType = 0
  VerticalArea = 2400000
  Width = 150
FEATURE [Part::FeaturePython] Structure187  label="25x15 C035"  # Arch/BIM 24 (typed FeaturePython)
  FaceMaker = 0
  Height = 3000
  HorizontalArea = 37500
  IfcData = attributes={"GlobalId": {"name": "GlobalId", "type": "IfcGloballyUniqueId", "is_enum": false, "enum_values": []}, "Description": {"... (+438 chars omitted),+1 more (map truncated)
  IfcType = 24
  Length = 250
  MoveBase = false
  MoveWithHost = false
  Nodes = (2) [(-1.05471e-15,1.36424e-15,0),(-1.05471e-15,1.36424e-15,3000)]
  NodesOffset = 0
  Normal = (0,0,0)
  PerimeterLength = 800
  Placement = pos=(13780,5970,3000) rot=(0,0,1;0rad)
  PredefinedType = 0
  VerticalArea = 2400000
  Width = 150
FEATURE [Part::FeaturePython] Structure188  label="25x15 C036"  # Arch/BIM 172 (typed FeaturePython)
  FaceMaker = 0
  Height = 3000
  HorizontalArea = 37500
  IfcData = attributes={"GlobalId": {"name": "GlobalId", "type": "IfcGloballyUniqueId", "is_enum": false, "enum_values": []}, "Description": {"... (+484 chars omitted),+1 more (map truncated)
  IfcType = 172
  Length = 250
  MoveBase = false
  MoveWithHost = false
  Nodes = (2) [(-1.05471e-15,1.36424e-15,0),(-1.05471e-15,1.36424e-15,3000)]
  NodesOffset = 0
  Normal = (0,0,0)
  PerimeterLength = 800
  Placement = pos=(1930,9900,3000) rot=(0,0,1;0rad)
  PredefinedType = 0
  VerticalArea = 2400000
  Width = 150
FEATURE [Part::FeaturePython] Structure189  label="25x15 C037"  # Arch/BIM 172 (typed FeaturePython)
  FaceMaker = 0
  Height = 3000
  HorizontalArea = 37500
  IfcData = attributes={"GlobalId": {"name": "GlobalId", "type": "IfcGloballyUniqueId", "is_enum": false, "enum_values": []}, "Description": {"... (+484 chars omitted),+1 more (map truncated)
  IfcType = 172
  Length = 250
  MoveBase = false
  MoveWithHost = false
  Nodes = (2) [(-1.05471e-15,1.36424e-15,0),(-1.05471e-15,1.36424e-15,3000)]
  NodesOffset = 0
  Normal = (0,0,0)
  PerimeterLength = 800
  Placement = pos=(9010,6640,3000) rot=(0,0,1;1.5708rad)
  PredefinedType = 0
  VerticalArea = 2400000
  Width = 150
FEATURE [Part::FeaturePython] Structure190  label="25x15 C038"  # Arch/BIM 172 (typed FeaturePython)
  FaceMaker = 0
  Height = 3000
  HorizontalArea = 37500
  IfcData = attributes={"GlobalId": {"name": "GlobalId", "type": "IfcGloballyUniqueId", "is_enum": false, "enum_values": []}, "Description": {"... (+484 chars omitted),+1 more (map truncated)
  IfcType = 172
  Length = 250
  MoveBase = false
  MoveWithHost = false
  Nodes = (2) [(-1.05471e-15,1.36424e-15,0),(-1.05471e-15,1.36424e-15,3000)]
  NodesOffset = 0
  Normal = (0,0,0)
  PerimeterLength = 800
  Placement = pos=(9010,3350,3000) rot=(0,0,1;1.5708rad)
  PredefinedType = 0
  VerticalArea = 2400000
  Width = 150
FEATURE [Part::FeaturePython] Structure191  label="25x15 C039"  # Arch/BIM 172 (typed FeaturePython)
  FaceMaker = 0
  Height = 3000
  HorizontalArea = 37500
  IfcData = attributes={"GlobalId": {"name": "GlobalId", "type": "IfcGloballyUniqueId", "is_enum": false, "enum_values": []}, "Description": {"... (+484 chars omitted),+1 more (map truncated)
  IfcType = 172
  Length = 250
  MoveBase = false
  MoveWithHost = false
  Nodes = (2) [(-1.05471e-15,1.36424e-15,0),(-1.05471e-15,1.36424e-15,3000)]
  NodesOffset = 0
  Normal = (0,0,0)
  PerimeterLength = 800
  Placement = pos=(10560,3350,3000) rot=(0,0,1;1.5708rad)
  PredefinedType = 0
  VerticalArea = 2400000
  Width = 150
FEATURE [Part::FeaturePython] Structure192  label="25x15 C040"  # Arch/BIM 172 (typed FeaturePython)
  FaceMaker = 0
  Height = 3000
  HorizontalArea = 37500
  IfcData = attributes={"GlobalId": {"name": "GlobalId", "type": "IfcGloballyUniqueId", "is_enum": false, "enum_values": []}, "Description": {"... (+484 chars omitted),+1 more (map truncated)
  IfcType = 172
  Length = 250
  MoveBase = false
  MoveWithHost = false
  Nodes = (2) [(-1.05471e-15,1.36424e-15,0),(-1.05471e-15,1.36424e-15,3000)]
  NodesOffset = 0
  Normal = (0,0,0)
  PerimeterLength = 800
  Placement = pos=(13780,3350,3000) rot=(0,0,1;1.5708rad)
  PredefinedType = 0
  VerticalArea = 2400000
  Width = 150
FEATURE [Part::FeaturePython] Structure193  label="25x15 C041"  # Arch/BIM 172 (typed FeaturePython)
  FaceMaker = 0
  Height = 3000
  HorizontalArea = 37500
  IfcData = attributes={"GlobalId": {"name": "GlobalId", "type": "IfcGloballyUniqueId", "is_enum": false, "enum_values": []}, "Description": {"... (+484 chars omitted),+1 more (map truncated)
  IfcType = 172
  Length = 250
  MoveBase = false
  MoveWithHost = false
  Nodes = (2) [(-1.05471e-15,1.36424e-15,0),(-1.05471e-15,1.36424e-15,3000)]
  NodesOffset = 0
  Normal = (0,0,0)
  PerimeterLength = 800
  Placement = pos=(9010,9900,3000) rot=(0,0,1;0rad)
  PredefinedType = 0
  VerticalArea = 2400000
  Width = 150
FEATURE [Part::FeaturePython] Structure194  label="25x15 C042"  # Arch/BIM 172 (typed FeaturePython)
  FaceMaker = 0
  Height = 3000
  HorizontalArea = 37500
  IfcData = attributes={"GlobalId": {"name": "GlobalId", "type": "IfcGloballyUniqueId", "is_enum": false, "enum_values": []}, "Description": {"... (+484 chars omitted),+1 more (map truncated)
  IfcType = 172
  Length = 250
  MoveBase = false
  MoveWithHost = false
  Nodes = (2) [(-1.05471e-15,1.36424e-15,0),(-1.05471e-15,1.36424e-15,3000)]
  NodesOffset = 0
  Normal = (0,0,0)
  PerimeterLength = 800
  Placement = pos=(6160,9900,3000) rot=(0,0,1;0rad)
  PredefinedType = 0
  VerticalArea = 2400000
  Width = 150
FEATURE [Part::FeaturePython] Structure195  label="25x15 C043"  # Arch/BIM 172 (typed FeaturePython)
  FaceMaker = 0
  Height = 3000
  HorizontalArea = 37500
  IfcData = attributes={"GlobalId": {"name": "GlobalId", "type": "IfcGloballyUniqueId", "is_enum": false, "enum_values": []}, "Description": {"... (+484 chars omitted),+1 more (map truncated)
  IfcType = 172
  Length = 250
  MoveBase = false
  MoveWithHost = false
  Nodes = (2) [(-1.05471e-15,1.36424e-15,0),(-1.05471e-15,1.36424e-15,3000)]
  NodesOffset = 0
  Normal = (0,0,0)
  PerimeterLength = 800
  Placement = pos=(12010,9900,3000) rot=(0,0,1;0rad)
  PredefinedType = 0
  VerticalArea = 2400000
  Width = 150
FEATURE [Part::FeaturePython] Structure196  label="25x15 C044"  # Arch/BIM 172 (typed FeaturePython)
  FaceMaker = 0
  Height = 3000
  HorizontalArea = 37500
  IfcData = attributes={"GlobalId": {"name": "GlobalId", "type": "IfcGloballyUniqueId", "is_enum": false, "enum_values": []}, "Description": {"... (+484 chars omitted),+1 more (map truncated)
  IfcType = 172
  Length = 250
  MoveBase = false
  MoveWithHost = false
  Nodes = (2) [(-1.05471e-15,1.36424e-15,0),(-1.05471e-15,1.36424e-15,3000)]
  NodesOffset = 0
  Normal = (0,0,0)
  PerimeterLength = 800
  Placement = pos=(15210,9900,3000) rot=(0,0,1;0rad)
  PredefinedType = 0
  VerticalArea = 2400000
  Width = 150
FEATURE [Part::FeaturePython] Structure179  label="25x20 C009"  # Arch/BIM 172 (typed FeaturePython)
  FaceMaker = 0
  Height = 3000
  HorizontalArea = 50000
  IfcData = attributes={"GlobalId": {"name": "GlobalId", "type": "IfcGloballyUniqueId", "is_enum": false, "enum_values": []}, "Description": {"... (+484 chars omitted),+1 more (map truncated)
  IfcType = 172
  Length = 250
  MoveBase = false
  MoveWithHost = false
  Nodes = (2) [(-1.05471e-15,-1.81899e-15,0),(-1.05471e-15,-1.81899e-15,3000)]
  NodesOffset = 0
  Normal = (0,0,0)
  PerimeterLength = 900
  Placement = pos=(1930,3350,3000) rot=(0,0,1;0rad)
  PredefinedType = 0
  VerticalArea = 2700000
  Width = 200
FEATURE [App::GeometryPython] BuildingPart012  label="Columnas P1"  # Arch/BIM 172 (typed FeaturePython)
  Area = 0
  Group = -> [Structure176,Structure177,Structure180,Structure181,Structure182,Structure183,Structure184,Structure185,Structure186,Structure187,Structure188,Structure189,Structure190,Structure191,Structure192,Structure193,Structure194,Structure195,Structure196,Structure178,Structure179]
  Height = 0
  HeightPropagate = true
  IfcData = attributes={"GlobalId": {"name": "GlobalId", "type": "IfcGloballyUniqueId", "is_enum": false, "enum_values": []}, "Description": {"... (+484 chars omitted),+1 more (map truncated)
  IfcType = 172
  LevelOffset = 0
  PredefinedType = 0
FEATURE [Part::FeaturePython] Wall002  label="Tabique Ascensor P1"  # Arch/BIM 166 (typed FeaturePython)
  Align = 1
  Area = 24900000
  Base = -> Rectangle003
  BlockHeight = 0
  BlockLength = 0
  CountBroken = 0
  CountEntire = 0
  Face = 0
  Height = 3000
  HorizontalArea = 1155000
  IfcData = attributes={"GlobalId": {"name": "GlobalId", "type": "IfcGloballyUniqueId", "is_enum": false, "enum_values": []}, "Description": {"... (+533 chars omitted),+1 more (map truncated)
  IfcType = 166
  Joint = 0
  Length = 8300
  MakeBlocks = false
  MoveBase = false
  MoveWithHost = false
  Normal = (0,0,0)
  OffsetFirst = 0
  OffsetSecond = 0
  PerimeterLength = 8300
  Placement = pos=(0,0,3000) rot=(0,0,1;0rad)
  PredefinedType = 0
  VerticalArea = 46200000
  Width = 150
FEATURE [Part::Part2DObjectPython] Rectangle004  # Draft 2D object (typed FeaturePython)
  Area = 12611050
  ChamferSize = 0
  Columns = 1
  FilletRadius = 0
  Height = 3110
  Length = 4055
  MakeFace = true
  Placement = pos=(2030,6715,3000) rot=(0,0,1;0rad)
  Rows = 1
FEATURE [Part::FeaturePython] Structure197  label="L101"  # Arch/BIM 172 (typed FeaturePython)
  Base = -> Rectangle004
  FaceMaker = 0
  Height = 150
  HorizontalArea = 12611050
  IfcData = attributes={"GlobalId": {"name": "GlobalId", "type": "IfcGloballyUniqueId", "is_enum": false, "enum_values": []}, "Description": {"... (+484 chars omitted),+1 more (map truncated)
  IfcType = 172
  Length = 0
  MoveBase = false
  MoveWithHost = false
  Nodes = (2) [(4057.5,8270,3000),(4057.5,8270,2850)]
  NodesOffset = 0
  Normal = (0,0,-1)
  PerimeterLength = 14330
  PredefinedType = 0
  VerticalArea = 2149500
  Width = 150
FEATURE [Part::Part2DObjectPython] Rectangle005  # Draft 2D object (typed FeaturePython)
  Area = 12732700
  ChamferSize = 0
  Columns = 1
  FilletRadius = 0
  Height = 3140
  Length = 4055
  MakeFace = true
  Placement = pos=(2030,3425,3000) rot=(0,0,1;0rad)
  Rows = 1
FEATURE [Part::FeaturePython] Structure198  label="L107"  # Arch/BIM 172 (typed FeaturePython)
  Base = -> Rectangle005
  FaceMaker = 0
  Height = 150
  HorizontalArea = 12732700
  IfcData = attributes={"GlobalId": {"name": "GlobalId", "type": "IfcGloballyUniqueId", "is_enum": false, "enum_values": []}, "Description": {"... (+484 chars omitted),+1 more (map truncated)
  IfcType = 172
  Length = 0
  MoveBase = false
  MoveWithHost = false
  Nodes = (2) [(4057.5,4995,3000),(4057.5,4995,2850)]
  NodesOffset = 0
  Normal = (0,0,-1)
  PerimeterLength = 14390
  PredefinedType = 0
  VerticalArea = 2158500
  Width = 150
FEATURE [Part::Part2DObjectPython] Rectangle006  # Draft 2D object (typed FeaturePython)
  Area = 1.25705e+07
  ChamferSize = 0
  Columns = 1
  FilletRadius = 0
  Height = 3100
  Length = 4055
  MakeFace = true
  Placement = pos=(2030,175,3000) rot=(0,0,1;0rad)
  Rows = 1
FEATURE [Part::FeaturePython] Structure199  label="L113"  # Arch/BIM 172 (typed FeaturePython)
  Base = -> Rectangle006
  FaceMaker = 0
  Height = 150
  HorizontalArea = 1.25705e+07
  IfcData = attributes={"GlobalId": {"name": "GlobalId", "type": "IfcGloballyUniqueId", "is_enum": false, "enum_values": []}, "Description": {"... (+484 chars omitted),+1 more (map truncated)
  IfcType = 172
  Length = 0
  MoveBase = false
  MoveWithHost = false
  Nodes = (2) [(4057.5,1725,3000),(4057.5,1725,2850)]
  NodesOffset = 0
  Normal = (0,0,-1)
  PerimeterLength = 14310
  PredefinedType = 0
  VerticalArea = 2146500
  Width = 150
FEATURE [Part::Part2DObjectPython] Rectangle008  # Draft 2D object (typed FeaturePython)
  Area = 4354000
  ChamferSize = 0
  Columns = 1
  FilletRadius = 0
  Height = 3110
  Length = 1400
  MakeFace = true
  Placement = pos=(9085,6715,3000) rot=(0,0,1;0rad)
  Rows = 1
FEATURE [Part::Part2DObjectPython] Rectangle009  # Draft 2D object (typed FeaturePython)
  Area = 1.794e+06
  ChamferSize = 0
  Columns = 1
  FilletRadius = 0
  Height = 1380
  Length = 1300
  MakeFace = true
  Placement = pos=(10635,8445,3000) rot=(0,0,1;0rad)
  Rows = 1
FEATURE [Part::Part2DObjectPython] Rectangle011  # Draft 2D object (typed FeaturePython)
  Area = 4396000
  ChamferSize = 0
  Columns = 1
  FilletRadius = 0
  Height = 3140
  Length = 1400
  MakeFace = true
  Placement = pos=(9085,3425,3000) rot=(0,0,1;0rad)
  Rows = 1
FEATURE [Part::Part2DObjectPython] Rectangle013  # Draft 2D object (typed FeaturePython)
  Area = 4.34e+06
  ChamferSize = 0
  Columns = 1
  FilletRadius = 0
  Height = 3100
  Length = 1400
  MakeFace = true
  Placement = pos=(9085,175,3000) rot=(0,0,1;0rad)
  Rows = 1
FEATURE [Part::FeaturePython] Structure200  label="V15x40 V102a"  # Arch/BIM 7 (typed FeaturePython)
  FaceMaker = 0
  Height = 400
  HorizontalArea = 405000
  IfcData = attributes={"GlobalId": {"name": "GlobalId", "type": "IfcGloballyUniqueId", "is_enum": false, "enum_values": []}, "Description": {"... (+475 chars omitted),+1 more (map truncated)
  IfcType = 7
  Length = 2700
  MoveBase = false
  MoveWithHost = false
  Nodes = (2) [(-1.72563e-31,-1.42109e-15,-7.77156e-16),(2700,-1.42109e-15,-7.77156e-16)]
  NodesOffset = 0
  Normal = (0,0,0)
  PerimeterLength = 5700
  Placement = pos=(8935,8295,2800) rot=(0,0,1;3.14159rad)
  PredefinedType = 0
  VerticalArea = 2.28e+06
  Width = 150
FEATURE [Part::FeaturePython] Structure201  label="V15x40 V107a"  # Arch/BIM 7 (typed FeaturePython)
  FaceMaker = 0
  Height = 400
  HorizontalArea = 405000
  IfcData = attributes={"GlobalId": {"name": "GlobalId", "type": "IfcGloballyUniqueId", "is_enum": false, "enum_values": []}, "Description": {"... (+475 chars omitted),+1 more (map truncated)
  IfcType = 7
  Length = 2700
  MoveBase = false
  MoveWithHost = false
  Nodes = (2) [(-1.72563e-31,-1.42109e-15,-7.77156e-16),(2700,-1.42109e-15,-7.77156e-16)]
  NodesOffset = 0
  Normal = (0,0,0)
  PerimeterLength = 5700
  Placement = pos=(8935,4995,2800) rot=(0,0,1;3.14159rad)
  PredefinedType = 0
  VerticalArea = 2.28e+06
  Width = 150
FEATURE [Part::FeaturePython] Structure202  label="V15x40 V112a"  # Arch/BIM 7 (typed FeaturePython)
  FaceMaker = 0
  Height = 400
  HorizontalArea = 405000
  IfcData = attributes={"GlobalId": {"name": "GlobalId", "type": "IfcGloballyUniqueId", "is_enum": false, "enum_values": []}, "Description": {"... (+475 chars omitted),+1 more (map truncated)
  IfcType = 7
  Length = 2700
  MoveBase = false
  MoveWithHost = false
  Nodes = (2) [(-1.72563e-31,-1.42109e-15,-7.77156e-16),(2700,-1.42109e-15,-7.77156e-16)]
  NodesOffset = 0
  Normal = (0,0,0)
  PerimeterLength = 5700
  Placement = pos=(8935,1700,2800) rot=(0,0,1;3.14159rad)
  PredefinedType = 0
  VerticalArea = 2.28e+06
  Width = 150
FEATURE [Part::Part2DObjectPython] Rectangle014  # Draft 2D object (typed FeaturePython)
  Area = 3928500
  ChamferSize = 0
  Columns = 1
  FilletRadius = 0
  Height = 1455
  Length = 2700
  MakeFace = true
  Placement = pos=(6235,8370,3000) rot=(0,0,1;0rad)
  Rows = 1
FEATURE [Part::Part2DObjectPython] Rectangle015  # Draft 2D object (typed FeaturePython)
  Area = 4.0365e+06
  ChamferSize = 0
  Columns = 1
  FilletRadius = 0
  Height = 1495
  Length = 2700
  MakeFace = true
  Placement = pos=(6235,3425,3000) rot=(0,0,1;0rad)
  Rows = 1
FEATURE [Part::Part2DObjectPython] Rectangle016  # Draft 2D object (typed FeaturePython)
  Area = 3.915e+06
  ChamferSize = 0
  Columns = 1
  FilletRadius = 0
  Height = 1450
  Length = 2700
  MakeFace = true
  Placement = pos=(6235,175,3000) rot=(0,0,1;0rad)
  Rows = 1
FEATURE [Part::Part2DObjectPython] Line  # Draft 2D object (typed FeaturePython)
  Area = 0
  ChamferSize = 0
  Closed = false
  End = (8635,7770,3000)
  FilletRadius = 0
  Length = 450
  MakeFace = true
  Placement = pos=(8635,8220,3000) rot=(0,0,1;0rad)
  Points = (2) [(0,0,0),(0,-450,0)]
  Start = (8635,8220,3000)
  Subdivisions = 0
FEATURE [Part::Part2DObjectPython] Line001  # Draft 2D object (typed FeaturePython)
  Area = 0
  ChamferSize = 0
  Closed = false
  End = (8935,7770,3000)
  FilletRadius = 0
  Length = 300
  MakeFace = true
  Placement = pos=(8635,7770,3000) rot=(0,0,1;0rad)
  Points = (2) [(0,0,0),(300,0,0)]
  Start = (8635,7770,3000)
  Subdivisions = 0
FEATURE [Part::Part2DObjectPython] Line002  # Draft 2D object (typed FeaturePython)
  Area = 0
  ChamferSize = 0
  Closed = false
  End = (8635,5070.11,3000)
  FilletRadius = 0
  Length = 450
  MakeFace = true
  Placement = pos=(8635,5520.11,3000) rot=(0,0,1;0rad)
  Points = (2) [(0,0,0),(0,-450,0)]
  Start = (8635,5520.11,3000)
  Subdivisions = 0
FEATURE [Part::Part2DObjectPython] Line003  # Draft 2D object (typed FeaturePython)
  Area = 0
  ChamferSize = 0
  Closed = false
  End = (8935,5520.11,3000)
  FilletRadius = 0
  Length = 300
  MakeFace = true
  Placement = pos=(8635,5520.11,3000) rot=(0,0,1;0rad)
  Points = (2) [(0,0,0),(300,0,0)]
  Start = (8635,5520.11,3000)
  Subdivisions = 0
FEATURE [Part::Part2DObjectPython] Line004  # Draft 2D object (typed FeaturePython)
  Area = 0
  ChamferSize = 0
  Closed = false
  End = (8935,2225.11,3000)
  FilletRadius = 0
  Length = 300
  MakeFace = true
  Placement = pos=(8635,2225.11,3000) rot=(0,0,1;0rad)
  Points = (2) [(0,0,0),(300,0,0)]
  Start = (8635,2225.11,3000)
  Subdivisions = 0
FEATURE [Part::Part2DObjectPython] Line005  # Draft 2D object (typed FeaturePython)
  Area = 0
  ChamferSize = 0
  Closed = false
  End = (8635,1775.11,3000)
  FilletRadius = 0
  Length = 450
  MakeFace = true
  Placement = pos=(8635,2225.11,3000) rot=(0,0,1;0rad)
  Points = (2) [(0,0,0),(0,-450,0)]
  Start = (8635,2225.11,3000)
  Subdivisions = 0
FEATURE [Part::Part2DObjectPython] Line006  # Draft 2D object (typed FeaturePython)
  Area = 0
  ChamferSize = 0
  Closed = false
  End = (8935,8220,3000)
  FilletRadius = 0
  Length = 540.833
  MakeFace = true
  Placement = pos=(8635,7770,3000) rot=(0,0,1;0rad)
  Points = (2) [(0,0,0),(300,450,0)]
  Start = (8635,7770,3000)
  Subdivisions = 0
FEATURE [Part::Part2DObjectPython] Line007  # Draft 2D object (typed FeaturePython)
  Area = 0
  ChamferSize = 0
  Closed = false
  End = (8935,7770,3000)
  FilletRadius = 0
  Length = 540.833
  MakeFace = true
  Placement = pos=(8635,8220,3000) rot=(0,0,1;0rad)
  Points = (2) [(0,0,0),(300,-450,0)]
  Start = (8635,8220,3000)
  Subdivisions = 0
FEATURE [Part::Part2DObjectPython] Line008  # Draft 2D object (typed FeaturePython)
  Area = 0
  ChamferSize = 0
  Closed = false
  End = (8935,5070,3000)
  FilletRadius = 0
  Length = 540.921
  MakeFace = true
  Placement = pos=(8635,5520.11,3000) rot=(0,0,1;0rad)
  Points = (2) [(0,0,0),(300,-450.106,0)]
  Start = (8635,5520.11,3000)
  Subdivisions = 0
FEATURE [Part::Part2DObjectPython] Line009  # Draft 2D object (typed FeaturePython)
  Area = 0
  ChamferSize = 0
  Closed = false
  End = (8935,5520.11,3000)
  FilletRadius = 0
  Length = 540.833
  MakeFace = true
  Placement = pos=(8635,5070.11,3000) rot=(0,0,1;0rad)
  Points = (2) [(0,0,0),(300,450,0)]
  Start = (8635,5070.11,3000)
  Subdivisions = 0
FEATURE [Part::Part2DObjectPython] Line010  # Draft 2D object (typed FeaturePython)
  Area = 0
  ChamferSize = 0
  Closed = false
  End = (8935,2225.11,3000)
  FilletRadius = 0
  Length = 540.833
  MakeFace = true
  Placement = pos=(8635,1775.11,3000) rot=(0,0,1;0rad)
  Points = (2) [(0,0,0),(300,450,0)]
  Start = (8635,1775.11,3000)
  Subdivisions = 0
FEATURE [Part::Part2DObjectPython] Line011  # Draft 2D object (typed FeaturePython)
  Area = 0
  ChamferSize = 0
  Closed = false
  End = (8935,1775,3000)
  FilletRadius = 0
  Length = 540.921
  MakeFace = true
  Placement = pos=(8635,2225.11,3000) rot=(0,0,1;0rad)
  Points = (2) [(0,0,0),(300,-450.106,0)]
  Start = (8635,2225.11,3000)
  Subdivisions = 0
FEATURE [Part::Part2DObjectPython] Wire  # Draft 2D object (typed FeaturePython)
  Area = 3.9285e+06
  ChamferSize = 0
  Closed = true
  End = (8935,6715,3000)
  FilletRadius = 0
  Length = 8410
  MakeFace = true
  Placement = pos=(6235,6715,3000) rot=(0,0,1;0rad)
  Points = (6) [(0,0,0),(0,1505,0),(2400,1505,0),(2400,1055,0),(2700,1055,0),(2700,9.09495e-13,0)]
  Start = (6235,6715,3000)
  Subdivisions = 0
FEATURE [Part::Part2DObjectPython] Wire001  # Draft 2D object (typed FeaturePython)
  Area = 3.90134e+06
  ChamferSize = 0
  Closed = true
  End = (6235,5070,3000)
  FilletRadius = 0
  Length = 8389.89
  MakeFace = true
  Placement = pos=(6235,6565,3000) rot=(0,0,1;0rad)
  Points = (6) [(0,0,0),(2700,0,0),(2700,-1044.89,0),(2400,-1044.89,0),(2400,-1494.89,0),(0,-1495,0)]
  Start = (6235,6565,3000)
  Subdivisions = 0
FEATURE [Part::Part2DObjectPython] Wire002  # Draft 2D object (typed FeaturePython)
  Area = 3.91484e+06
  ChamferSize = 0
  Closed = true
  End = (6235,1775,3000)
  FilletRadius = 0
  Length = 8399.89
  MakeFace = true
  Placement = pos=(6235,3275,3000) rot=(0,0,1;0rad)
  Points = (6) [(0,0,0),(2700,-4.54747e-13,0),(2700,-1049.89,0),(2400,-1049.89,0),(2400,-1499.89,0),(0,-1500,0)]
  Start = (6235,3275,3000)
  Subdivisions = 0
FEATURE [Part::Part2DObjectPython] Rectangle017  # Draft 2D object (typed FeaturePython)
  Area = 4174500
  ChamferSize = 0
  Columns = 1
  FilletRadius = 0
  Height = 1380
  Length = 3025
  MakeFace = true
  Placement = pos=(12085,8445,3000) rot=(0,0,1;0rad)
  Rows = 1
FEATURE [Part::FeaturePython] Structure204  label="V15x40 V130a"  # Arch/BIM 7 (typed FeaturePython)
  FaceMaker = 0
  Height = 400
  HorizontalArea = 370500
  IfcData = attributes={"GlobalId": {"name": "GlobalId", "type": "IfcGloballyUniqueId", "is_enum": false, "enum_values": []}, "Description": {"... (+475 chars omitted),+1 more (map truncated)
  IfcType = 7
  Length = 2470
  MoveBase = false
  MoveWithHost = false
  Nodes = (2) [(-1.72563e-31,-1.42109e-15,-7.77156e-16),(2470,-1.42109e-15,-7.77156e-16)]
  NodesOffset = 0
  Normal = (0,0,0)
  PerimeterLength = 5240
  Placement = pos=(12010,3425,2800) rot=(0,0,1;1.5708rad)
  PredefinedType = 0
  VerticalArea = 2096000
  Width = 150
FEATURE [App::GeometryPython] BuildingPart009  label="Vigas sobre PB"  # Arch/BIM 172 (typed FeaturePython)
  Area = 0
  Group = -> [Structure109,Structure115,Structure200,Structure119,Structure120,Structure141,Structure112,Structure116,Structure201,Structure121,Structure129,Structure130,Structure113,Structure117,Structure202,Structure122,Structure125,Structure114,Structure118,Structure123,Structure124,Structure133,Structure132,Structure131,Structure136,Structure135,Structure134,Structure140,Structure139,Structure204,+8 more]
  Height = 0
  HeightPropagate = true
  IfcData = attributes={"GlobalId": {"name": "GlobalId", "type": "IfcGloballyUniqueId", "is_enum": false, "enum_values": []}, "Description": {"... (+484 chars omitted),+1 more (map truncated)
  IfcType = 172
  LevelOffset = 0
  PredefinedType = 0
FEATURE [Part::Part2DObjectPython] Rectangle018  # Draft 2D object (typed FeaturePython)
  Area = 3.211e+06
  ChamferSize = 0
  Columns = 1
  FilletRadius = 0
  Height = 2470
  Length = 1300
  MakeFace = true
  Placement = pos=(10635,3425,3000) rot=(0,0,1;0rad)
  Rows = 1
FEATURE [Part::Part2DObjectPython] Rectangle019  # Draft 2D object (typed FeaturePython)
  Area = 3.93965e+06
  ChamferSize = 0
  Columns = 1
  FilletRadius = 0
  Height = 2470
  Length = 1595
  MakeFace = true
  Placement = pos=(12085,3425,3000) rot=(0,0,1;0rad)
  Rows = 1
FEATURE [Part::Part2DObjectPython] Rectangle020  # Draft 2D object (typed FeaturePython)
  Area = 9439500
  ChamferSize = 0
  Columns = 1
  FilletRadius = 0
  Height = 3100
  Length = 3045
  MakeFace = true
  Placement = pos=(10635,175,3000) rot=(0,0,1;0rad)
  Rows = 1
FEATURE [Part::FeaturePython] Structure205  label="L102"  # Arch/BIM 172 (typed FeaturePython)
  Base = -> Rectangle014
  FaceMaker = 0
  Height = 150
  HorizontalArea = 3928500
  IfcData = attributes={"GlobalId": {"name": "GlobalId", "type": "IfcGloballyUniqueId", "is_enum": false, "enum_values": []}, "Description": {"... (+484 chars omitted),+1 more (map truncated)
  IfcType = 172
  Length = 0
  MoveBase = false
  MoveWithHost = false
  Nodes = (2) [(7585,9097.5,3000),(7585,9097.5,2850)]
  NodesOffset = 0
  Normal = (0,0,-1)
  PerimeterLength = 8310
  PredefinedType = 0
  VerticalArea = 1246500
  Width = 150
FEATURE [Part::FeaturePython] Structure206  label="L103"  # Arch/BIM 172 (typed FeaturePython)
  Base = -> Wire
  FaceMaker = 0
  Height = 150
  HorizontalArea = 3.9285e+06
  IfcData = attributes={"GlobalId": {"name": "GlobalId", "type": "IfcGloballyUniqueId", "is_enum": false, "enum_values": []}, "Description": {"... (+484 chars omitted),+1 more (map truncated)
  IfcType = 172
  Length = 0
  MoveBase = false
  MoveWithHost = false
  Nodes = (2) [(7543.76,7449.37,3000),(7543.76,7449.37,2850)]
  NodesOffset = 0
  Normal = (0,0,-1)
  PerimeterLength = 8410
  Placement = pos=(0,0,-150) rot=(0,0,1;0rad)
  PredefinedType = 0
  VerticalArea = 1261500
  Width = 150
FEATURE [Part::FeaturePython] Structure207  label="L108"  # Arch/BIM 172 (typed FeaturePython)
  Base = -> Wire001
  FaceMaker = 0
  Height = 150
  HorizontalArea = 3.90134e+06
  IfcData = attributes={"GlobalId": {"name": "GlobalId", "type": "IfcGloballyUniqueId", "is_enum": false, "enum_values": []}, "Description": {"... (+484 chars omitted),+1 more (map truncated)
  IfcType = 172
  Length = 0
  MoveBase = false
  MoveWithHost = false
  Nodes = (2) [(7543.46,5835.61,3000),(7543.46,5835.61,2850)]
  NodesOffset = 0
  Normal = (0,0,-1)
  PerimeterLength = 8389.89
  Placement = pos=(0,0,-150) rot=(0,0,1;0rad)
  PredefinedType = 0
  VerticalArea = 1.25848e+06
  Width = 150
FEATURE [Part::FeaturePython] Structure208  label="L109"  # Arch/BIM 172 (typed FeaturePython)
  Base = -> Rectangle015
  FaceMaker = 0
  Height = 150
  HorizontalArea = 4.0365e+06
  IfcData = attributes={"GlobalId": {"name": "GlobalId", "type": "IfcGloballyUniqueId", "is_enum": false, "enum_values": []}, "Description": {"... (+484 chars omitted),+1 more (map truncated)
  IfcType = 172
  Length = 0
  MoveBase = false
  MoveWithHost = false
  Nodes = (2) [(7585,4172.5,3000),(7585,4172.5,2850)]
  NodesOffset = 0
  Normal = (0,0,-1)
  PerimeterLength = 8390
  PredefinedType = 0
  VerticalArea = 1258500
  Width = 150
FEATURE [Part::FeaturePython] Structure209  label="L114"  # Arch/BIM 172 (typed FeaturePython)
  Base = -> Wire002
  FaceMaker = 0
  Height = 150
  HorizontalArea = 3.91484e+06
  IfcData = attributes={"GlobalId": {"name": "GlobalId", "type": "IfcGloballyUniqueId", "is_enum": false, "enum_values": []}, "Description": {"... (+484 chars omitted),+1 more (map truncated)
  IfcType = 172
  Length = 0
  MoveBase = false
  MoveWithHost = false
  Nodes = (2) [(7543.6,2543.13,3000),(7543.6,2543.13,2850)]
  NodesOffset = 0
  Normal = (0,0,-1)
  PerimeterLength = 8399.89
  Placement = pos=(0,0,-150) rot=(0,0,1;0rad)
  PredefinedType = 0
  VerticalArea = 1.25998e+06
  Width = 150
FEATURE [Part::FeaturePython] Structure210  label="L115"  # Arch/BIM 172 (typed FeaturePython)
  Base = -> Rectangle016
  FaceMaker = 0
  Height = 150
  HorizontalArea = 3.915e+06
  IfcData = attributes={"GlobalId": {"name": "GlobalId", "type": "IfcGloballyUniqueId", "is_enum": false, "enum_values": []}, "Description": {"... (+484 chars omitted),+1 more (map truncated)
  IfcType = 172
  Length = 0
  MoveBase = false
  MoveWithHost = false
  Nodes = (2) [(7585,900,3000),(7585,900,2850)]
  NodesOffset = 0
  Normal = (0,0,-1)
  PerimeterLength = 8300
  PredefinedType = 0
  VerticalArea = 1.245e+06
  Width = 150
FEATURE [Part::FeaturePython] Structure211  label="L104"  # Arch/BIM 172 (typed FeaturePython)
  Base = -> Rectangle008
  FaceMaker = 0
  Height = 150
  HorizontalArea = 4354000
  IfcData = attributes={"GlobalId": {"name": "GlobalId", "type": "IfcGloballyUniqueId", "is_enum": false, "enum_values": []}, "Description": {"... (+484 chars omitted),+1 more (map truncated)
  IfcType = 172
  Length = 0
  MoveBase = false
  MoveWithHost = false
  Nodes = (2) [(9785,8270,3000),(9785,8270,2850)]
  NodesOffset = 0
  Normal = (0,0,-1)
  PerimeterLength = 9020
  PredefinedType = 0
  VerticalArea = 1353000
  Width = 150
FEATURE [Part::FeaturePython] Structure212  label="L110"  # Arch/BIM 172 (typed FeaturePython)
  Base = -> Rectangle011
  FaceMaker = 0
  Height = 150
  HorizontalArea = 4396000
  IfcData = attributes={"GlobalId": {"name": "GlobalId", "type": "IfcGloballyUniqueId", "is_enum": false, "enum_values": []}, "Description": {"... (+484 chars omitted),+1 more (map truncated)
  IfcType = 172
  Length = 0
  MoveBase = false
  MoveWithHost = false
  Nodes = (2) [(9785,4995,3000),(9785,4995,2850)]
  NodesOffset = 0
  Normal = (0,0,-1)
  PerimeterLength = 9080
  PredefinedType = 0
  VerticalArea = 1362000
  Width = 150
FEATURE [Part::FeaturePython] Structure213  label="L116"  # Arch/BIM 172 (typed FeaturePython)
  Base = -> Rectangle013
  FaceMaker = 0
  Height = 150
  HorizontalArea = 4.34e+06
  IfcData = attributes={"GlobalId": {"name": "GlobalId", "type": "IfcGloballyUniqueId", "is_enum": false, "enum_values": []}, "Description": {"... (+484 chars omitted),+1 more (map truncated)
  IfcType = 172
  Length = 0
  MoveBase = false
  MoveWithHost = false
  Nodes = (2) [(9785,1725,3000),(9785,1725,2850)]
  NodesOffset = 0
  Normal = (0,0,-1)
  PerimeterLength = 9000
  PredefinedType = 0
  VerticalArea = 1350000
  Width = 150
FEATURE [Part::FeaturePython] Structure214  label="L105"  # Arch/BIM 172 (typed FeaturePython)
  Base = -> Rectangle009
  FaceMaker = 0
  Height = 150
  HorizontalArea = 1.794e+06
  IfcData = attributes={"GlobalId": {"name": "GlobalId", "type": "IfcGloballyUniqueId", "is_enum": false, "enum_values": []}, "Description": {"... (+484 chars omitted),+1 more (map truncated)
  IfcType = 172
  Length = 0
  MoveBase = false
  MoveWithHost = false
  Nodes = (2) [(11285,9135,3000),(11285,9135,2850)]
  NodesOffset = 0
  Normal = (0,0,-1)
  PerimeterLength = 5360
  PredefinedType = 0
  VerticalArea = 804000
  Width = 150
FEATURE [Part::FeaturePython] Structure215  label="L111"  # Arch/BIM 172 (typed FeaturePython)
  Base = -> Rectangle018
  FaceMaker = 0
  Height = 150
  HorizontalArea = 3.211e+06
  IfcData = attributes={"GlobalId": {"name": "GlobalId", "type": "IfcGloballyUniqueId", "is_enum": false, "enum_values": []}, "Description": {"... (+484 chars omitted),+1 more (map truncated)
  IfcType = 172
  Length = 0
  MoveBase = false
  MoveWithHost = false
  Nodes = (2) [(11285,4660,3000),(11285,4660,2850)]
  NodesOffset = 0
  Normal = (0,0,-1)
  PerimeterLength = 7540
  Placement = pos=(0,0,-150) rot=(0,0,1;0rad)
  PredefinedType = 0
  VerticalArea = 1.131e+06
  Width = 150
FEATURE [Part::FeaturePython] Structure216  label="L117"  # Arch/BIM 172 (typed FeaturePython)
  Base = -> Rectangle020
  FaceMaker = 0
  Height = 150
  HorizontalArea = 9439500
  IfcData = attributes={"GlobalId": {"name": "GlobalId", "type": "IfcGloballyUniqueId", "is_enum": false, "enum_values": []}, "Description": {"... (+484 chars omitted),+1 more (map truncated)
  IfcType = 172
  Length = 0
  MoveBase = false
  MoveWithHost = false
  Nodes = (2) [(12157.5,1725,3000),(12157.5,1725,2850)]
  NodesOffset = 0
  Normal = (0,0,-1)
  PerimeterLength = 12290
  PredefinedType = 0
  VerticalArea = 1843500
  Width = 150
FEATURE [Part::FeaturePython] Structure217  label="L112"  # Arch/BIM 172 (typed FeaturePython)
  Base = -> Rectangle019
  FaceMaker = 0
  Height = 150
  HorizontalArea = 3.93965e+06
  IfcData = attributes={"GlobalId": {"name": "GlobalId", "type": "IfcGloballyUniqueId", "is_enum": false, "enum_values": []}, "Description": {"... (+484 chars omitted),+1 more (map truncated)
  IfcType = 172
  Length = 0
  MoveBase = false
  MoveWithHost = false
  Nodes = (2) [(12882.5,4660,3000),(12882.5,4660,2850)]
  NodesOffset = 0
  Normal = (0,0,-1)
  PerimeterLength = 8130
  PredefinedType = 0
  VerticalArea = 1.2195e+06
  Width = 150
FEATURE [Part::FeaturePython] Structure218  label="L106"  # Arch/BIM 172 (typed FeaturePython)
  Base = -> Rectangle017
  FaceMaker = 0
  Height = 150
  HorizontalArea = 4174500
  IfcData = attributes={"GlobalId": {"name": "GlobalId", "type": "IfcGloballyUniqueId", "is_enum": false, "enum_values": []}, "Description": {"... (+484 chars omitted),+1 more (map truncated)
  IfcType = 172
  Length = 0
  MoveBase = false
  MoveWithHost = false
  Nodes = (2) [(13597.5,9135,3000),(13597.5,9135,2850)]
  NodesOffset = 0
  Normal = (0,0,-1)
  PerimeterLength = 8810
  PredefinedType = 0
  VerticalArea = 1321500
  Width = 150
FEATURE [App::GeometryPython] BuildingPart013  label="Lineas 2D"  # Arch/BIM 172 (typed FeaturePython)
  Area = 0
  Group = -> [Line,Line001,Line002,Line003,Line004,Line005,Line006,Line007,Line008,Line009,Line010,Line011]
  Height = 0
  HeightPropagate = true
  IfcData = attributes={"GlobalId": {"name": "GlobalId", "type": "IfcGloballyUniqueId", "is_enum": false, "enum_values": []}, "Description": {"... (+484 chars omitted),+1 more (map truncated)
  IfcType = 172
  LevelOffset = 0
  PredefinedType = 0
FEATURE [App::GeometryPython] BuildingPart014  label="Losas sobre PB"  # Arch/BIM 172 (typed FeaturePython)
  Area = 0
  Group = -> [Structure197,Structure205,Structure206,Structure211,Structure214,Structure218,Structure198,Structure207,Structure208,Structure212,Structure215,Structure217,Structure199,Structure209,Structure210,Structure213,Structure216]
  Height = 0
  HeightPropagate = true
  IfcData = attributes={"GlobalId": {"name": "GlobalId", "type": "IfcGloballyUniqueId", "is_enum": false, "enum_values": []}, "Description": {"... (+484 chars omitted),+1 more (map truncated)
  IfcType = 172
  LevelOffset = 0
  PredefinedType = 0
FEATURE [App::GeometryPython] BuildingPart001  label="Nivel 0"  # Arch/BIM 172 (typed FeaturePython)
  Area = 24900000
  Group = -> [BuildingPart004,BuildingPart013,BuildingPart014,Wall001,BuildingPart009]
  Height = 0
  HeightPropagate = true
  IfcData = attributes={"GlobalId": {"name": "GlobalId", "type": "IfcGloballyUniqueId", "is_enum": false, "enum_values": []}, "Description": {"... (+484 chars omitted),+1 more (map truncated)
  IfcType = 172
  LevelOffset = 0
  PredefinedType = 0
FEATURE [Part::FeaturePython] Structure219  label="L118"  # Arch/BIM 172 (typed FeaturePython)
  Base = -> Rectangle004
  FaceMaker = 0
  Height = 150
  HorizontalArea = 12611050
  IfcData = attributes={"GlobalId": {"name": "GlobalId", "type": "IfcGloballyUniqueId", "is_enum": false, "enum_values": []}, "Description": {"... (+484 chars omitted),+1 more (map truncated)
  IfcType = 172
  Length = 0
  MoveBase = false
  MoveWithHost = false
  Nodes = (2) [(4057.5,8270,3000),(4057.5,8270,2850)]
  NodesOffset = 0
  Normal = (0,0,-1)
  PerimeterLength = 14330
  Placement = pos=(0,0,3000) rot=(0,0,1;0rad)
  PredefinedType = 0
  VerticalArea = 2149500
  Width = 150
FEATURE [Part::FeaturePython] Structure220  label="L119"  # Arch/BIM 172 (typed FeaturePython)
  Base = -> Rectangle005
  FaceMaker = 0
  Height = 150
  HorizontalArea = 12732700
  IfcData = attributes={"GlobalId": {"name": "GlobalId", "type": "IfcGloballyUniqueId", "is_enum": false, "enum_values": []}, "Description": {"... (+484 chars omitted),+1 more (map truncated)
  IfcType = 172
  Length = 0
  MoveBase = false
  MoveWithHost = false
  Nodes = (2) [(4057.5,4995,3000),(4057.5,4995,2850)]
  NodesOffset = 0
  Normal = (0,0,-1)
  PerimeterLength = 14390
  Placement = pos=(0,0,3000) rot=(0,0,1;0rad)
  PredefinedType = 0
  VerticalArea = 2158500
  Width = 150
FEATURE [Part::FeaturePython] Structure221  label="L120"  # Arch/BIM 172 (typed FeaturePython)
  Base = -> Rectangle006
  FaceMaker = 0
  Height = 150
  HorizontalArea = 1.25705e+07
  IfcData = attributes={"GlobalId": {"name": "GlobalId", "type": "IfcGloballyUniqueId", "is_enum": false, "enum_values": []}, "Description": {"... (+484 chars omitted),+1 more (map truncated)
  IfcType = 172
  Length = 0
  MoveBase = false
  MoveWithHost = false
  Nodes = (2) [(4057.5,1725,3000),(4057.5,1725,2850)]
  NodesOffset = 0
  Normal = (0,0,-1)
  PerimeterLength = 14310
  Placement = pos=(0,0,3000) rot=(0,0,1;0rad)
  PredefinedType = 0
  VerticalArea = 2146500
  Width = 150
FEATURE [Part::FeaturePython] Structure222  label="V15x40 V102a001"  # Arch/BIM 7 (typed FeaturePython)
  FaceMaker = 0
  Height = 400
  HorizontalArea = 405000
  IfcData = attributes={"GlobalId": {"name": "GlobalId", "type": "IfcGloballyUniqueId", "is_enum": false, "enum_values": []}, "Description": {"... (+475 chars omitted),+1 more (map truncated)
  IfcType = 7
  Length = 2700
  MoveBase = false
  MoveWithHost = false
  Nodes = (2) [(-1.72563e-31,-1.42109e-15,-7.77156e-16),(2700,-1.42109e-15,-7.77156e-16)]
  NodesOffset = 0
  Normal = (0,0,0)
  PerimeterLength = 5700
  Placement = pos=(8935,8295,5800) rot=(0,0,1;3.14159rad)
  PredefinedType = 0
  VerticalArea = 2.28e+06
  Width = 150
FEATURE [Part::FeaturePython] Structure223  label="V15x40 V107a001"  # Arch/BIM 7 (typed FeaturePython)
  FaceMaker = 0
  Height = 400
  HorizontalArea = 405000
  IfcData = attributes={"GlobalId": {"name": "GlobalId", "type": "IfcGloballyUniqueId", "is_enum": false, "enum_values": []}, "Description": {"... (+475 chars omitted),+1 more (map truncated)
  IfcType = 7
  Length = 2700
  MoveBase = false
  MoveWithHost = false
  Nodes = (2) [(-1.72563e-31,-1.42109e-15,-7.77156e-16),(2700,-1.42109e-15,-7.77156e-16)]
  NodesOffset = 0
  Normal = (0,0,0)
  PerimeterLength = 5700
  Placement = pos=(8935,4995,5800) rot=(0,0,1;3.14159rad)
  PredefinedType = 0
  VerticalArea = 2.28e+06
  Width = 150
FEATURE [Part::FeaturePython] Structure224  label="V15x40 V112a001"  # Arch/BIM 7 (typed FeaturePython)
  FaceMaker = 0
  Height = 400
  HorizontalArea = 405000
  IfcData = attributes={"GlobalId": {"name": "GlobalId", "type": "IfcGloballyUniqueId", "is_enum": false, "enum_values": []}, "Description": {"... (+475 chars omitted),+1 more (map truncated)
  IfcType = 7
  Length = 2700
  MoveBase = false
  MoveWithHost = false
  Nodes = (2) [(-1.72563e-31,-1.42109e-15,-7.77156e-16),(2700,-1.42109e-15,-7.77156e-16)]
  NodesOffset = 0
  Normal = (0,0,0)
  PerimeterLength = 5700
  Placement = pos=(8935,1700,5800) rot=(0,0,1;3.14159rad)
  PredefinedType = 0
  VerticalArea = 2.28e+06
  Width = 150
FEATURE [Part::FeaturePython] Structure225  label="V15x40 V130a001"  # Arch/BIM 7 (typed FeaturePython)
  FaceMaker = 0
  Height = 400
  HorizontalArea = 370500
  IfcData = attributes={"GlobalId": {"name": "GlobalId", "type": "IfcGloballyUniqueId", "is_enum": false, "enum_values": []}, "Description": {"... (+475 chars omitted),+1 more (map truncated)
  IfcType = 7
  Length = 2470
  MoveBase = false
  MoveWithHost = false
  Nodes = (2) [(-1.72563e-31,-1.42109e-15,-7.77156e-16),(2470,-1.42109e-15,-7.77156e-16)]
  NodesOffset = 0
  Normal = (0,0,0)
  PerimeterLength = 5240
  Placement = pos=(12010,3425,5800) rot=(0,0,1;1.5708rad)
  PredefinedType = 0
  VerticalArea = 2096000
  Width = 150
FEATURE [App::GeometryPython] BuildingPart011  label="Vigas sobre P1"  # Arch/BIM 172 (typed FeaturePython)
  Area = 0
  Group = -> [Structure222,Structure223,Structure224,Structure225,Structure142,Structure143,Structure144,Structure145,Structure146,Structure147,Structure148,Structure149,Structure150,Structure151,Structure152,Structure153,Structure154,Structure155,Structure156,Structure157,Structure158,Structure159,Structure160,Structure161,Structure162,Structure163,Structure164,Structure165,Structure166,Structure167,+8 more]
  Height = 0
  HeightPropagate = true
  IfcData = attributes={"GlobalId": {"name": "GlobalId", "type": "IfcGloballyUniqueId", "is_enum": false, "enum_values": []}, "Description": {"... (+484 chars omitted),+1 more (map truncated)
  IfcType = 172
  LevelOffset = 0
  PredefinedType = 0
FEATURE [Part::FeaturePython] Structure226  label="L121"  # Arch/BIM 172 (typed FeaturePython)
  Base = -> Rectangle014
  FaceMaker = 0
  Height = 150
  HorizontalArea = 3928500
  IfcData = attributes={"GlobalId": {"name": "GlobalId", "type": "IfcGloballyUniqueId", "is_enum": false, "enum_values": []}, "Description": {"... (+484 chars omitted),+1 more (map truncated)
  IfcType = 172
  Length = 0
  MoveBase = false
  MoveWithHost = false
  Nodes = (2) [(7585,9097.5,3000),(7585,9097.5,2850)]
  NodesOffset = 0
  Normal = (0,0,-1)
  PerimeterLength = 8310
  Placement = pos=(0,0,3000) rot=(0,0,1;0rad)
  PredefinedType = 0
  VerticalArea = 1246500
  Width = 150
FEATURE [Part::FeaturePython] Structure227  label="L122"  # Arch/BIM 172 (typed FeaturePython)
  Base = -> Wire
  FaceMaker = 0
  Height = 150
  HorizontalArea = 3.9285e+06
  IfcData = attributes={"GlobalId": {"name": "GlobalId", "type": "IfcGloballyUniqueId", "is_enum": false, "enum_values": []}, "Description": {"... (+484 chars omitted),+1 more (map truncated)
  IfcType = 172
  Length = 0
  MoveBase = false
  MoveWithHost = false
  Nodes = (2) [(7543.76,7449.37,3000),(7543.76,7449.37,2850)]
  NodesOffset = 0
  Normal = (0,0,-1)
  PerimeterLength = 8410
  Placement = pos=(0,0,2850) rot=(0,0,1;0rad)
  PredefinedType = 0
  VerticalArea = 1261500
  Width = 150
FEATURE [Part::FeaturePython] Structure228  label="L123"  # Arch/BIM 172 (typed FeaturePython)
  Base = -> Wire001
  FaceMaker = 0
  Height = 150
  HorizontalArea = 3.90134e+06
  IfcData = attributes={"GlobalId": {"name": "GlobalId", "type": "IfcGloballyUniqueId", "is_enum": false, "enum_values": []}, "Description": {"... (+484 chars omitted),+1 more (map truncated)
  IfcType = 172
  Length = 0
  MoveBase = false
  MoveWithHost = false
  Nodes = (2) [(7543.46,5835.61,3000),(7543.46,5835.61,2850)]
  NodesOffset = 0
  Normal = (0,0,-1)
  PerimeterLength = 8389.89
  Placement = pos=(0,0,2850) rot=(0,0,1;0rad)
  PredefinedType = 0
  VerticalArea = 1.25848e+06
  Width = 150
FEATURE [Part::FeaturePython] Structure229  label="L124"  # Arch/BIM 172 (typed FeaturePython)
  Base = -> Rectangle015
  FaceMaker = 0
  Height = 150
  HorizontalArea = 4.0365e+06
  IfcData = attributes={"GlobalId": {"name": "GlobalId", "type": "IfcGloballyUniqueId", "is_enum": false, "enum_values": []}, "Description": {"... (+484 chars omitted),+1 more (map truncated)
  IfcType = 172
  Length = 0
  MoveBase = false
  MoveWithHost = false
  Nodes = (2) [(7585,4172.5,3000),(7585,4172.5,2850)]
  NodesOffset = 0
  Normal = (0,0,-1)
  PerimeterLength = 8390
  Placement = pos=(0,0,3000) rot=(0,0,1;0rad)
  PredefinedType = 0
  VerticalArea = 1258500
  Width = 150
FEATURE [Part::FeaturePython] Structure230  label="L125"  # Arch/BIM 172 (typed FeaturePython)
  Base = -> Wire002
  FaceMaker = 0
  Height = 150
  HorizontalArea = 3.91484e+06
  IfcData = attributes={"GlobalId": {"name": "GlobalId", "type": "IfcGloballyUniqueId", "is_enum": false, "enum_values": []}, "Description": {"... (+484 chars omitted),+1 more (map truncated)
  IfcType = 172
  Length = 0
  MoveBase = false
  MoveWithHost = false
  Nodes = (2) [(7543.6,2543.13,3000),(7543.6,2543.13,2850)]
  NodesOffset = 0
  Normal = (0,0,-1)
  PerimeterLength = 8399.89
  Placement = pos=(0,0,2850) rot=(0,0,1;0rad)
  PredefinedType = 0
  VerticalArea = 1.25998e+06
  Width = 150
FEATURE [Part::FeaturePython] Structure231  label="L126"  # Arch/BIM 172 (typed FeaturePython)
  Base = -> Rectangle016
  FaceMaker = 0
  Height = 150
  HorizontalArea = 3.915e+06
  IfcData = attributes={"GlobalId": {"name": "GlobalId", "type": "IfcGloballyUniqueId", "is_enum": false, "enum_values": []}, "Description": {"... (+484 chars omitted),+1 more (map truncated)
  IfcType = 172
  Length = 0
  MoveBase = false
  MoveWithHost = false
  Nodes = (2) [(7585,900,3000),(7585,900,2850)]
  NodesOffset = 0
  Normal = (0,0,-1)
  PerimeterLength = 8300
  Placement = pos=(0,0,3000) rot=(0,0,1;0rad)
  PredefinedType = 0
  VerticalArea = 1.245e+06
  Width = 150
FEATURE [Part::FeaturePython] Structure232  label="L127"  # Arch/BIM 172 (typed FeaturePython)
  Base = -> Rectangle008
  FaceMaker = 0
  Height = 150
  HorizontalArea = 4354000
  IfcData = attributes={"GlobalId": {"name": "GlobalId", "type": "IfcGloballyUniqueId", "is_enum": false, "enum_values": []}, "Description": {"... (+484 chars omitted),+1 more (map truncated)
  IfcType = 172
  Length = 0
  MoveBase = false
  MoveWithHost = false
  Nodes = (2) [(9785,8270,3000),(9785,8270,2850)]
  NodesOffset = 0
  Normal = (0,0,-1)
  PerimeterLength = 9020
  Placement = pos=(0,0,3000) rot=(0,0,1;0rad)
  PredefinedType = 0
  VerticalArea = 1353000
  Width = 150
FEATURE [Part::FeaturePython] Structure233  label="L128"  # Arch/BIM 172 (typed FeaturePython)
  Base = -> Rectangle011
  FaceMaker = 0
  Height = 150
  HorizontalArea = 4396000
  IfcData = attributes={"GlobalId": {"name": "GlobalId", "type": "IfcGloballyUniqueId", "is_enum": false, "enum_values": []}, "Description": {"... (+484 chars omitted),+1 more (map truncated)
  IfcType = 172
  Length = 0
  MoveBase = false
  MoveWithHost = false
  Nodes = (2) [(9785,4995,3000),(9785,4995,2850)]
  NodesOffset = 0
  Normal = (0,0,-1)
  PerimeterLength = 9080
  Placement = pos=(0,0,3000) rot=(0,0,1;0rad)
  PredefinedType = 0
  VerticalArea = 1362000
  Width = 150
FEATURE [Part::FeaturePython] Structure234  label="L129"  # Arch/BIM 172 (typed FeaturePython)
  Base = -> Rectangle013
  FaceMaker = 0
  Height = 150
  HorizontalArea = 4.34e+06
  IfcData = attributes={"GlobalId": {"name": "GlobalId", "type": "IfcGloballyUniqueId", "is_enum": false, "enum_values": []}, "Description": {"... (+484 chars omitted),+1 more (map truncated)
  IfcType = 172
  Length = 0
  MoveBase = false
  MoveWithHost = false
  Nodes = (2) [(9785,1725,3000),(9785,1725,2850)]
  NodesOffset = 0
  Normal = (0,0,-1)
  PerimeterLength = 9000
  Placement = pos=(0,0,3000) rot=(0,0,1;0rad)
  PredefinedType = 0
  VerticalArea = 1350000
  Width = 150
FEATURE [Part::FeaturePython] Structure235  label="L130"  # Arch/BIM 172 (typed FeaturePython)
  Base = -> Rectangle009
  FaceMaker = 0
  Height = 150
  HorizontalArea = 1.794e+06
  IfcData = attributes={"GlobalId": {"name": "GlobalId", "type": "IfcGloballyUniqueId", "is_enum": false, "enum_values": []}, "Description": {"... (+484 chars omitted),+1 more (map truncated)
  IfcType = 172
  Length = 0
  MoveBase = false
  MoveWithHost = false
  Nodes = (2) [(11285,9135,3000),(11285,9135,2850)]
  NodesOffset = 0
  Normal = (0,0,-1)
  PerimeterLength = 5360
  Placement = pos=(0,0,3000) rot=(0,0,1;0rad)
  PredefinedType = 0
  VerticalArea = 804000
  Width = 150
FEATURE [Part::FeaturePython] Structure236  label="L131"  # Arch/BIM 172 (typed FeaturePython)
  Base = -> Rectangle018
  FaceMaker = 0
  Height = 150
  HorizontalArea = 3.211e+06
  IfcData = attributes={"GlobalId": {"name": "GlobalId", "type": "IfcGloballyUniqueId", "is_enum": false, "enum_values": []}, "Description": {"... (+484 chars omitted),+1 more (map truncated)
  IfcType = 172
  Length = 0
  MoveBase = false
  MoveWithHost = false
  Nodes = (2) [(11285,4660,3000),(11285,4660,2850)]
  NodesOffset = 0
  Normal = (0,0,-1)
  PerimeterLength = 7540
  Placement = pos=(0,0,2850) rot=(0,0,1;0rad)
  PredefinedType = 0
  VerticalArea = 1.131e+06
  Width = 150
FEATURE [Part::FeaturePython] Structure237  label="L132"  # Arch/BIM 172 (typed FeaturePython)
  Base = -> Rectangle020
  FaceMaker = 0
  Height = 150
  HorizontalArea = 9439500
  IfcData = attributes={"GlobalId": {"name": "GlobalId", "type": "IfcGloballyUniqueId", "is_enum": false, "enum_values": []}, "Description": {"... (+484 chars omitted),+1 more (map truncated)
  IfcType = 172
  Length = 0
  MoveBase = false
  MoveWithHost = false
  Nodes = (2) [(12157.5,1725,3000),(12157.5,1725,2850)]
  NodesOffset = 0
  Normal = (0,0,-1)
  PerimeterLength = 12290
  Placement = pos=(0,0,3000) rot=(0,0,1;0rad)
  PredefinedType = 0
  VerticalArea = 1843500
  Width = 150
FEATURE [Part::FeaturePython] Structure238  label="L133"  # Arch/BIM 172 (typed FeaturePython)
  Base = -> Rectangle019
  FaceMaker = 0
  Height = 150
  HorizontalArea = 3.93965e+06
  IfcData = attributes={"GlobalId": {"name": "GlobalId", "type": "IfcGloballyUniqueId", "is_enum": false, "enum_values": []}, "Description": {"... (+484 chars omitted),+1 more (map truncated)
  IfcType = 172
  Length = 0
  MoveBase = false
  MoveWithHost = false
  Nodes = (2) [(12882.5,4660,3000),(12882.5,4660,2850)]
  NodesOffset = 0
  Normal = (0,0,-1)
  PerimeterLength = 8130
  Placement = pos=(0,0,3000) rot=(0,0,1;0rad)
  PredefinedType = 0
  VerticalArea = 1.2195e+06
  Width = 150
FEATURE [Part::FeaturePython] Structure239  label="L134"  # Arch/BIM 172 (typed FeaturePython)
  Base = -> Rectangle017
  FaceMaker = 0
  Height = 150
  HorizontalArea = 4174500
  IfcData = attributes={"GlobalId": {"name": "GlobalId", "type": "IfcGloballyUniqueId", "is_enum": false, "enum_values": []}, "Description": {"... (+484 chars omitted),+1 more (map truncated)
  IfcType = 172
  Length = 0
  MoveBase = false
  MoveWithHost = false
  Nodes = (2) [(13597.5,9135,3000),(13597.5,9135,2850)]
  NodesOffset = 0
  Normal = (0,0,-1)
  PerimeterLength = 8810
  Placement = pos=(0,0,3000) rot=(0,0,1;0rad)
  PredefinedType = 0
  VerticalArea = 1321500
  Width = 150
FEATURE [App::GeometryPython] BuildingPart015  label="Losas sobre P1"  # Arch/BIM 172 (typed FeaturePython)
  Area = 0
  Group = -> [Structure219,Structure220,Structure221,Structure226,Structure227,Structure228,Structure229,Structure230,Structure231,Structure232,Structure233,Structure234,Structure235,Structure236,Structure237,Structure238,Structure239]
  Height = 0
  HeightPropagate = true
  IfcData = attributes={"GlobalId": {"name": "GlobalId", "type": "IfcGloballyUniqueId", "is_enum": false, "enum_values": []}, "Description": {"... (+484 chars omitted),+1 more (map truncated)
  IfcType = 172
  LevelOffset = 0
  PredefinedType = 0
FEATURE [App::GeometryPython] BuildingPart003  label="Piso 1"  # Arch/BIM 172 (typed FeaturePython)
  Area = 24900000
  Group = -> [BuildingPart012,BuildingPart015,Wall002,BuildingPart011]
  Height = 0
  HeightPropagate = true
  IfcData = attributes={"GlobalId": {"name": "GlobalId", "type": "IfcGloballyUniqueId", "is_enum": false, "enum_values": []}, "Description": {"... (+484 chars omitted),+1 more (map truncated)
  IfcType = 172
  LevelOffset = 0
  Placement = pos=(0,0,3000) rot=(0,0,1;0rad)
  PredefinedType = 0
FEATURE [Part::FeaturePython] Structure240  label="25x15 C045"  # Arch/BIM 24 (typed FeaturePython)
  FaceMaker = 0
  Height = 3000
  HorizontalArea = 37500
  IfcData = attributes={"GlobalId": {"name": "GlobalId", "type": "IfcGloballyUniqueId", "is_enum": false, "enum_values": []}, "Description": {"... (+438 chars omitted),+1 more (map truncated)
  IfcType = 24
  Length = 250
  MoveBase = false
  MoveWithHost = false
  Nodes = (2) [(-1.05471e-15,1.36424e-15,0),(-1.05471e-15,1.36424e-15,3000)]
  NodesOffset = 0
  Normal = (0,0,0)
  PerimeterLength = 800
  Placement = pos=(1930,9900,6000) rot=(0,0,1;0rad)
  PredefinedType = 0
  VerticalArea = 2400000
  Width = 150
FEATURE [Part::FeaturePython] Structure241  label="25x15 C046"  # Arch/BIM 172 (typed FeaturePython)
  FaceMaker = 0
  Height = 3000
  HorizontalArea = 37500
  IfcData = attributes={"GlobalId": {"name": "GlobalId", "type": "IfcGloballyUniqueId", "is_enum": false, "enum_values": []}, "Description": {"... (+484 chars omitted),+1 more (map truncated)
  IfcType = 172
  Length = 250
  MoveBase = false
  MoveWithHost = false
  Nodes = (2) [(-1.05471e-15,1.36424e-15,0),(-1.05471e-15,1.36424e-15,3000)]
  NodesOffset = 0
  Normal = (0,0,0)
  PerimeterLength = 800
  Placement = pos=(1930,100,6000) rot=(0,0,1;0rad)
  PredefinedType = 0
  VerticalArea = 2400000
  Width = 150
FEATURE [Part::FeaturePython] Structure242  label="25x20 C010"  # Arch/BIM 24 (typed FeaturePython)
  FaceMaker = 0
  Height = 3000
  HorizontalArea = 50000
  IfcData = attributes={"GlobalId": {"name": "GlobalId", "type": "IfcGloballyUniqueId", "is_enum": false, "enum_values": []}, "Description": {"... (+438 chars omitted),+1 more (map truncated)
  IfcType = 24
  Length = 250
  MoveBase = false
  MoveWithHost = false
  Nodes = (2) [(-1.05471e-15,-1.81899e-15,0),(-1.05471e-15,-1.81899e-15,3000)]
  NodesOffset = 0
  Normal = (0,0,0)
  PerimeterLength = 900
  Placement = pos=(1930,6640,6000) rot=(0,0,1;0rad)
  PredefinedType = 0
  VerticalArea = 2700000
  Width = 200
FEATURE [Part::FeaturePython] Structure243  label="25x20 C011"  # Arch/BIM 172 (typed FeaturePython)
  FaceMaker = 0
  Height = 3000
  HorizontalArea = 50000
  IfcData = attributes={"GlobalId": {"name": "GlobalId", "type": "IfcGloballyUniqueId", "is_enum": false, "enum_values": []}, "Description": {"... (+484 chars omitted),+1 more (map truncated)
  IfcType = 172
  Length = 250
  MoveBase = false
  MoveWithHost = false
  Nodes = (2) [(-1.05471e-15,-1.81899e-15,0),(-1.05471e-15,-1.81899e-15,3000)]
  NodesOffset = 0
  Normal = (0,0,0)
  PerimeterLength = 900
  Placement = pos=(1930,3350,6000) rot=(0,0,1;0rad)
  PredefinedType = 0
  VerticalArea = 2700000
  Width = 200
FEATURE [Part::FeaturePython] Structure244  label="25x15 C047"  # Arch/BIM 24 (typed FeaturePython)
  FaceMaker = 0
  Height = 3000
  HorizontalArea = 37500
  IfcData = attributes={"GlobalId": {"name": "GlobalId", "type": "IfcGloballyUniqueId", "is_enum": false, "enum_values": []}, "Description": {"... (+438 chars omitted),+1 more (map truncated)
  IfcType = 24
  Length = 250
  MoveBase = false
  MoveWithHost = false
  Nodes = (2) [(-1.05471e-15,1.36424e-15,0),(-1.05471e-15,1.36424e-15,3000)]
  NodesOffset = 0
  Normal = (0,0,0)
  PerimeterLength = 800
  Placement = pos=(6160,6640,6000) rot=(0,0,1;0rad)
  PredefinedType = 0
  VerticalArea = 2400000
  Width = 150
FEATURE [Part::FeaturePython] Structure245  label="25x15 C048"  # Arch/BIM 24 (typed FeaturePython)
  FaceMaker = 0
  Height = 3000
  HorizontalArea = 37500
  IfcData = attributes={"GlobalId": {"name": "GlobalId", "type": "IfcGloballyUniqueId", "is_enum": false, "enum_values": []}, "Description": {"... (+438 chars omitted),+1 more (map truncated)
  IfcType = 24
  Length = 250
  MoveBase = false
  MoveWithHost = false
  Nodes = (2) [(-1.05471e-15,1.36424e-15,0),(-1.05471e-15,1.36424e-15,3000)]
  NodesOffset = 0
  Normal = (0,0,0)
  PerimeterLength = 800
  Placement = pos=(6160,3350,6000) rot=(0,0,1;0rad)
  PredefinedType = 0
  VerticalArea = 2400000
  Width = 150
FEATURE [Part::FeaturePython] Structure246  label="25x15 C049"  # Arch/BIM 24 (typed FeaturePython)
  FaceMaker = 0
  Height = 3000
  HorizontalArea = 37500
  IfcData = attributes={"GlobalId": {"name": "GlobalId", "type": "IfcGloballyUniqueId", "is_enum": false, "enum_values": []}, "Description": {"... (+438 chars omitted),+1 more (map truncated)
  IfcType = 24
  Length = 250
  MoveBase = false
  MoveWithHost = false
  Nodes = (2) [(-1.05471e-15,1.36424e-15,0),(-1.05471e-15,1.36424e-15,3000)]
  NodesOffset = 0
  Normal = (0,0,0)
  PerimeterLength = 800
  Placement = pos=(6160,100,6000) rot=(0,0,1;0rad)
  PredefinedType = 0
  VerticalArea = 2400000
  Width = 150
FEATURE [Part::FeaturePython] Structure247  label="25x15 C050"  # Arch/BIM 24 (typed FeaturePython)
  FaceMaker = 0
  Height = 3000
  HorizontalArea = 37500
  IfcData = attributes={"GlobalId": {"name": "GlobalId", "type": "IfcGloballyUniqueId", "is_enum": false, "enum_values": []}, "Description": {"... (+438 chars omitted),+1 more (map truncated)
  IfcType = 24
  Length = 250
  MoveBase = false
  MoveWithHost = false
  Nodes = (2) [(-1.05471e-15,1.36424e-15,0),(-1.05471e-15,1.36424e-15,3000)]
  NodesOffset = 0
  Normal = (0,0,0)
  PerimeterLength = 800
  Placement = pos=(9010,100,6000) rot=(0,0,1;0rad)
  PredefinedType = 0
  VerticalArea = 2400000
  Width = 150
FEATURE [Part::FeaturePython] Structure248  label="25x15 C051"  # Arch/BIM 24 (typed FeaturePython)
  FaceMaker = 0
  Height = 3000
  HorizontalArea = 37500
  IfcData = attributes={"GlobalId": {"name": "GlobalId", "type": "IfcGloballyUniqueId", "is_enum": false, "enum_values": []}, "Description": {"... (+438 chars omitted),+1 more (map truncated)
  IfcType = 24
  Length = 250
  MoveBase = false
  MoveWithHost = false
  Nodes = (2) [(-1.05471e-15,1.36424e-15,0),(-1.05471e-15,1.36424e-15,3000)]
  NodesOffset = 0
  Normal = (0,0,0)
  PerimeterLength = 800
  Placement = pos=(10560,100,6000) rot=(0,0,1;0rad)
  PredefinedType = 0
  VerticalArea = 2400000
  Width = 150
FEATURE [Part::FeaturePython] Structure249  label="25x15 C052"  # Arch/BIM 24 (typed FeaturePython)
  FaceMaker = 0
  Height = 3000
  HorizontalArea = 37500
  IfcData = attributes={"GlobalId": {"name": "GlobalId", "type": "IfcGloballyUniqueId", "is_enum": false, "enum_values": []}, "Description": {"... (+438 chars omitted),+1 more (map truncated)
  IfcType = 24
  Length = 250
  MoveBase = false
  MoveWithHost = false
  Nodes = (2) [(-1.05471e-15,1.36424e-15,0),(-1.05471e-15,1.36424e-15,3000)]
  NodesOffset = 0
  Normal = (0,0,0)
  PerimeterLength = 800
  Placement = pos=(13780,100,6000) rot=(0,0,1;0rad)
  PredefinedType = 0
  VerticalArea = 2400000
  Width = 150
FEATURE [Part::FeaturePython] Structure250  label="25x15 C053"  # Arch/BIM 24 (typed FeaturePython)
  FaceMaker = 0
  Height = 3000
  HorizontalArea = 37500
  IfcData = attributes={"GlobalId": {"name": "GlobalId", "type": "IfcGloballyUniqueId", "is_enum": false, "enum_values": []}, "Description": {"... (+438 chars omitted),+1 more (map truncated)
  IfcType = 24
  Length = 250
  MoveBase = false
  MoveWithHost = false
  Nodes = (2) [(-1.05471e-15,1.36424e-15,0),(-1.05471e-15,1.36424e-15,3000)]
  NodesOffset = 0
  Normal = (0,0,0)
  PerimeterLength = 800
  Placement = pos=(15210,5970,6000) rot=(0,0,1;0rad)
  PredefinedType = 0
  VerticalArea = 2400000
  Width = 150
FEATURE [Part::FeaturePython] Structure251  label="25x15 C054"  # Arch/BIM 24 (typed FeaturePython)
  FaceMaker = 0
  Height = 3000
  HorizontalArea = 37500
  IfcData = attributes={"GlobalId": {"name": "GlobalId", "type": "IfcGloballyUniqueId", "is_enum": false, "enum_values": []}, "Description": {"... (+438 chars omitted),+1 more (map truncated)
  IfcType = 24
  Length = 250
  MoveBase = false
  MoveWithHost = false
  Nodes = (2) [(-1.05471e-15,1.36424e-15,0),(-1.05471e-15,1.36424e-15,3000)]
  NodesOffset = 0
  Normal = (0,0,0)
  PerimeterLength = 800
  Placement = pos=(13780,5970,6000) rot=(0,0,1;0rad)
  PredefinedType = 0
  VerticalArea = 2400000
  Width = 150
FEATURE [Part::FeaturePython] Structure252  label="25x15 C055"  # Arch/BIM 172 (typed FeaturePython)
  FaceMaker = 0
  Height = 3000
  HorizontalArea = 37500
  IfcData = attributes={"GlobalId": {"name": "GlobalId", "type": "IfcGloballyUniqueId", "is_enum": false, "enum_values": []}, "Description": {"... (+484 chars omitted),+1 more (map truncated)
  IfcType = 172
  Length = 250
  MoveBase = false
  MoveWithHost = false
  Nodes = (2) [(-1.05471e-15,1.36424e-15,0),(-1.05471e-15,1.36424e-15,3000)]
  NodesOffset = 0
  Normal = (0,0,0)
  PerimeterLength = 800
  Placement = pos=(1930,9900,6000) rot=(0,0,1;0rad)
  PredefinedType = 0
  VerticalArea = 2400000
  Width = 150
FEATURE [Part::FeaturePython] Structure253  label="25x15 C056"  # Arch/BIM 172 (typed FeaturePython)
  FaceMaker = 0
  Height = 3000
  HorizontalArea = 37500
  IfcData = attributes={"GlobalId": {"name": "GlobalId", "type": "IfcGloballyUniqueId", "is_enum": false, "enum_values": []}, "Description": {"... (+484 chars omitted),+1 more (map truncated)
  IfcType = 172
  Length = 250
  MoveBase = false
  MoveWithHost = false
  Nodes = (2) [(-1.05471e-15,1.36424e-15,0),(-1.05471e-15,1.36424e-15,3000)]
  NodesOffset = 0
  Normal = (0,0,0)
  PerimeterLength = 800
  Placement = pos=(9010,6640,6000) rot=(0,0,1;1.5708rad)
  PredefinedType = 0
  VerticalArea = 2400000
  Width = 150
FEATURE [Part::FeaturePython] Structure254  label="25x15 C057"  # Arch/BIM 172 (typed FeaturePython)
  FaceMaker = 0
  Height = 3000
  HorizontalArea = 37500
  IfcData = attributes={"GlobalId": {"name": "GlobalId", "type": "IfcGloballyUniqueId", "is_enum": false, "enum_values": []}, "Description": {"... (+484 chars omitted),+1 more (map truncated)
  IfcType = 172
  Length = 250
  MoveBase = false
  MoveWithHost = false
  Nodes = (2) [(-1.05471e-15,1.36424e-15,0),(-1.05471e-15,1.36424e-15,3000)]
  NodesOffset = 0
  Normal = (0,0,0)
  PerimeterLength = 800
  Placement = pos=(9010,3350,6000) rot=(0,0,1;1.5708rad)
  PredefinedType = 0
  VerticalArea = 2400000
  Width = 150
FEATURE [Part::FeaturePython] Structure255  label="25x15 C058"  # Arch/BIM 172 (typed FeaturePython)
  FaceMaker = 0
  Height = 3000
  HorizontalArea = 37500
  IfcData = attributes={"GlobalId": {"name": "GlobalId", "type": "IfcGloballyUniqueId", "is_enum": false, "enum_values": []}, "Description": {"... (+484 chars omitted),+1 more (map truncated)
  IfcType = 172
  Length = 250
  MoveBase = false
  MoveWithHost = false
  Nodes = (2) [(-1.05471e-15,1.36424e-15,0),(-1.05471e-15,1.36424e-15,3000)]
  NodesOffset = 0
  Normal = (0,0,0)
  PerimeterLength = 800
  Placement = pos=(10560,3350,6000) rot=(0,0,1;1.5708rad)
  PredefinedType = 0
  VerticalArea = 2400000
  Width = 150
FEATURE [Part::FeaturePython] Structure256  label="25x15 C059"  # Arch/BIM 172 (typed FeaturePython)
  FaceMaker = 0
  Height = 3000
  HorizontalArea = 37500
  IfcData = attributes={"GlobalId": {"name": "GlobalId", "type": "IfcGloballyUniqueId", "is_enum": false, "enum_values": []}, "Description": {"... (+484 chars omitted),+1 more (map truncated)
  IfcType = 172
  Length = 250
  MoveBase = false
  MoveWithHost = false
  Nodes = (2) [(-1.05471e-15,1.36424e-15,0),(-1.05471e-15,1.36424e-15,3000)]
  NodesOffset = 0
  Normal = (0,0,0)
  PerimeterLength = 800
  Placement = pos=(13780,3350,6000) rot=(0,0,1;1.5708rad)
  PredefinedType = 0
  VerticalArea = 2400000
  Width = 150
FEATURE [Part::FeaturePython] Structure257  label="25x15 C060"  # Arch/BIM 172 (typed FeaturePython)
  FaceMaker = 0
  Height = 3000
  HorizontalArea = 37500
  IfcData = attributes={"GlobalId": {"name": "GlobalId", "type": "IfcGloballyUniqueId", "is_enum": false, "enum_values": []}, "Description": {"... (+484 chars omitted),+1 more (map truncated)
  IfcType = 172
  Length = 250
  MoveBase = false
  MoveWithHost = false
  Nodes = (2) [(-1.05471e-15,1.36424e-15,0),(-1.05471e-15,1.36424e-15,3000)]
  NodesOffset = 0
  Normal = (0,0,0)
  PerimeterLength = 800
  Placement = pos=(9010,9900,6000) rot=(0,0,1;0rad)
  PredefinedType = 0
  VerticalArea = 2400000
  Width = 150
FEATURE [Part::FeaturePython] Structure258  label="25x15 C061"  # Arch/BIM 172 (typed FeaturePython)
  FaceMaker = 0
  Height = 3000
  HorizontalArea = 37500
  IfcData = attributes={"GlobalId": {"name": "GlobalId", "type": "IfcGloballyUniqueId", "is_enum": false, "enum_values": []}, "Description": {"... (+484 chars omitted),+1 more (map truncated)
  IfcType = 172
  Length = 250
  MoveBase = false
  MoveWithHost = false
  Nodes = (2) [(-1.05471e-15,1.36424e-15,0),(-1.05471e-15,1.36424e-15,3000)]
  NodesOffset = 0
  Normal = (0,0,0)
  PerimeterLength = 800
  Placement = pos=(6160,9900,6000) rot=(0,0,1;0rad)
  PredefinedType = 0
  VerticalArea = 2400000
  Width = 150
FEATURE [Part::FeaturePython] Structure259  label="25x15 C062"  # Arch/BIM 172 (typed FeaturePython)
  FaceMaker = 0
  Height = 3000
  HorizontalArea = 37500
  IfcData = attributes={"GlobalId": {"name": "GlobalId", "type": "IfcGloballyUniqueId", "is_enum": false, "enum_values": []}, "Description": {"... (+484 chars omitted),+1 more (map truncated)
  IfcType = 172
  Length = 250
  MoveBase = false
  MoveWithHost = false
  Nodes = (2) [(-1.05471e-15,1.36424e-15,0),(-1.05471e-15,1.36424e-15,3000)]
  NodesOffset = 0
  Normal = (0,0,0)
  PerimeterLength = 800
  Placement = pos=(12010,9900,6000) rot=(0,0,1;0rad)
  PredefinedType = 0
  VerticalArea = 2400000
  Width = 150
FEATURE [Part::FeaturePython] Structure260  label="25x15 C063"  # Arch/BIM 172 (typed FeaturePython)
  FaceMaker = 0
  Height = 3000
  HorizontalArea = 37500
  IfcData = attributes={"GlobalId": {"name": "GlobalId", "type": "IfcGloballyUniqueId", "is_enum": false, "enum_values": []}, "Description": {"... (+484 chars omitted),+1 more (map truncated)
  IfcType = 172
  Length = 250
  MoveBase = false
  MoveWithHost = false
  Nodes = (2) [(-1.05471e-15,1.36424e-15,0),(-1.05471e-15,1.36424e-15,3000)]
  NodesOffset = 0
  Normal = (0,0,0)
  PerimeterLength = 800
  Placement = pos=(15210,9900,6000) rot=(0,0,1;0rad)
  PredefinedType = 0
  VerticalArea = 2400000
  Width = 150
FEATURE [App::GeometryPython] BuildingPart016  label="Columnas P2"  # Arch/BIM 172 (typed FeaturePython)
  Area = 0
  Group = -> [Structure240,Structure241,Structure244,Structure245,Structure246,Structure247,Structure248,Structure249,Structure250,Structure251,Structure252,Structure253,Structure254,Structure255,Structure256,Structure257,Structure258,Structure259,Structure260,Structure242,Structure243]
  Height = 0
  HeightPropagate = true
  IfcData = attributes={"GlobalId": {"name": "GlobalId", "type": "IfcGloballyUniqueId", "is_enum": false, "enum_values": []}, "Description": {"... (+484 chars omitted),+1 more (map truncated)
  IfcType = 172
  LevelOffset = 0
  PredefinedType = 0
FEATURE [Part::FeaturePython] Wall003  label="Tabique Ascensor P2"  # Arch/BIM 166 (typed FeaturePython)
  Align = 1
  Area = 24900000
  Base = -> Rectangle003
  BlockHeight = 0
  BlockLength = 0
  CountBroken = 0
  CountEntire = 0
  Face = 0
  Height = 3000
  HorizontalArea = 1155000
  IfcData = attributes={"GlobalId": {"name": "GlobalId", "type": "IfcGloballyUniqueId", "is_enum": false, "enum_values": []}, "Description": {"... (+533 chars omitted),+1 more (map truncated)
  IfcType = 166
  Joint = 0
  Length = 8300
  MakeBlocks = false
  MoveBase = false
  MoveWithHost = false
  Normal = (0,0,0)
  OffsetFirst = 0
  OffsetSecond = 0
  PerimeterLength = 8300
  Placement = pos=(0,0,6000) rot=(0,0,1;0rad)
  PredefinedType = 0
  VerticalArea = 46200000
  Width = 150
FEATURE [Part::FeaturePython] Structure261  label="V15x40 V161"  # Arch/BIM 7 (typed FeaturePython)
  FaceMaker = 0
  Height = 400
  HorizontalArea = 597000
  IfcData = attributes={"GlobalId": {"name": "GlobalId", "type": "IfcGloballyUniqueId", "is_enum": false, "enum_values": []}, "Description": {"... (+475 chars omitted),+1 more (map truncated)
  IfcType = 7
  Length = 3980
  MoveBase = false
  MoveWithHost = false
  Nodes = (2) [(-1.72563e-31,-1.42109e-15,-7.77156e-16),(3980,-1.42109e-15,-7.77156e-16)]
  NodesOffset = 0
  Normal = (0,0,0)
  PerimeterLength = 8260
  Placement = pos=(2055,9900,8800) rot=(0,0,1;0rad)
  PredefinedType = 0
  VerticalArea = 3.304e+06
  Width = 150
FEATURE [Part::FeaturePython] Structure262  label="V15x40 V162"  # Arch/BIM 7 (typed FeaturePython)
  FaceMaker = 0
  Height = 400
  HorizontalArea = 390000
  IfcData = attributes={"GlobalId": {"name": "GlobalId", "type": "IfcGloballyUniqueId", "is_enum": false, "enum_values": []}, "Description": {"... (+475 chars omitted),+1 more (map truncated)
  IfcType = 7
  Length = 2600
  MoveBase = false
  MoveWithHost = false
  Nodes = (2) [(-1.72563e-31,-1.42109e-15,-7.77156e-16),(2600,-1.42109e-15,-7.77156e-16)]
  NodesOffset = 0
  Normal = (0,0,0)
  PerimeterLength = 5500
  Placement = pos=(6285,9900,8800) rot=(0,0,1;0rad)
  PredefinedType = 0
  VerticalArea = 2200000
  Width = 150
FEATURE [Part::FeaturePython] Structure263  label="V15x40 V163"  # Arch/BIM 7 (typed FeaturePython)
  FaceMaker = 0
  Height = 400
  HorizontalArea = 412500
  IfcData = attributes={"GlobalId": {"name": "GlobalId", "type": "IfcGloballyUniqueId", "is_enum": false, "enum_values": []}, "Description": {"... (+475 chars omitted),+1 more (map truncated)
  IfcType = 7
  Length = 2750
  MoveBase = false
  MoveWithHost = false
  Nodes = (2) [(-1.72563e-31,-1.42109e-15,-7.77156e-16),(2750,-1.42109e-15,-7.77156e-16)]
  NodesOffset = 0
  Normal = (0,0,0)
  PerimeterLength = 5800
  Placement = pos=(9135,9900,8800) rot=(0,0,1;0rad)
  PredefinedType = 0
  VerticalArea = 2320000
  Width = 150
FEATURE [Part::FeaturePython] Structure264  label="V15x40 V164"  # Arch/BIM 7 (typed FeaturePython)
  FaceMaker = 0
  Height = 400
  HorizontalArea = 442500
  IfcData = attributes={"GlobalId": {"name": "GlobalId", "type": "IfcGloballyUniqueId", "is_enum": false, "enum_values": []}, "Description": {"... (+475 chars omitted),+1 more (map truncated)
  IfcType = 7
  Length = 2950
  MoveBase = false
  MoveWithHost = false
  Nodes = (2) [(-1.72563e-31,-1.42109e-15,-7.77156e-16),(2950,-1.42109e-15,-7.77156e-16)]
  NodesOffset = 0
  Normal = (0,0,0)
  PerimeterLength = 6200
  Placement = pos=(12135,9900,8800) rot=(0,0,1;0rad)
  PredefinedType = 0
  VerticalArea = 2.48e+06
  Width = 150
FEATURE [Part::FeaturePython] Structure265  label="V15x40 V165"  # Arch/BIM 7 (typed FeaturePython)
  FaceMaker = 0
  Height = 400
  HorizontalArea = 453750
  IfcData = attributes={"GlobalId": {"name": "GlobalId", "type": "IfcGloballyUniqueId", "is_enum": false, "enum_values": []}, "Description": {"... (+475 chars omitted),+1 more (map truncated)
  IfcType = 7
  Length = 3025
  MoveBase = false
  MoveWithHost = false
  Nodes = (2) [(-1.72563e-31,-1.42109e-15,-7.77156e-16),(3025,-1.42109e-15,-7.77156e-16)]
  NodesOffset = 0
  Normal = (0,0,0)
  PerimeterLength = 6350
  Placement = pos=(12085,8370,8800) rot=(0,0,1;0rad)
  PredefinedType = 0
  VerticalArea = 2.54e+06
  Width = 150
FEATURE [Part::FeaturePython] Structure266  label="V15x40 V166"  # Arch/BIM 7 (typed FeaturePython)
  FaceMaker = 0
  Height = 400
  HorizontalArea = 597000
  IfcData = attributes={"GlobalId": {"name": "GlobalId", "type": "IfcGloballyUniqueId", "is_enum": false, "enum_values": []}, "Description": {"... (+475 chars omitted),+1 more (map truncated)
  IfcType = 7
  Length = 3980
  MoveBase = false
  MoveWithHost = false
  Nodes = (2) [(-1.72563e-31,-1.42109e-15,-7.77156e-16),(3980,-1.42109e-15,-7.77156e-16)]
  NodesOffset = 0
  Normal = (0,0,0)
  PerimeterLength = 8260
  Placement = pos=(2055,6640,8800) rot=(0,0,1;0rad)
  PredefinedType = 0
  VerticalArea = 3.304e+06
  Width = 150
FEATURE [Part::FeaturePython] Structure267  label="V15x40 V167"  # Arch/BIM 7 (typed FeaturePython)
  FaceMaker = 0
  Height = 400
  HorizontalArea = 397500
  IfcData = attributes={"GlobalId": {"name": "GlobalId", "type": "IfcGloballyUniqueId", "is_enum": false, "enum_values": []}, "Description": {"... (+475 chars omitted),+1 more (map truncated)
  IfcType = 7
  Length = 2650
  MoveBase = false
  MoveWithHost = false
  Nodes = (2) [(-1.72563e-31,-1.42109e-15,-7.77156e-16),(2650,-1.42109e-15,-7.77156e-16)]
  NodesOffset = 0
  Normal = (0,0,0)
  PerimeterLength = 5600
  Placement = pos=(6285,6640,8800) rot=(0,0,1;0rad)
  PredefinedType = 0
  VerticalArea = 2240000
  Width = 150
FEATURE [Part::FeaturePython] Structure268  label="V15x40 V168"  # Arch/BIM 7 (typed FeaturePython)
  FaceMaker = 0
  Height = 400
  HorizontalArea = 210000
  IfcData = attributes={"GlobalId": {"name": "GlobalId", "type": "IfcGloballyUniqueId", "is_enum": false, "enum_values": []}, "Description": {"... (+475 chars omitted),+1 more (map truncated)
  IfcType = 7
  Length = 1400
  MoveBase = false
  MoveWithHost = false
  Nodes = (2) [(-1.72563e-31,-1.42109e-15,-7.77156e-16),(1400,-1.42109e-15,-7.77156e-16)]
  NodesOffset = 0
  Normal = (0,0,0)
  PerimeterLength = 3100
  Placement = pos=(9085,6640,8800) rot=(0,0,1;0rad)
  PredefinedType = 0
  VerticalArea = 1240000
  Width = 150
FEATURE [Part::FeaturePython] Structure269  label="V15x40 V169"  # Arch/BIM 7 (typed FeaturePython)
  FaceMaker = 0
  Height = 400
  HorizontalArea = 235500
  IfcData = attributes={"GlobalId": {"name": "GlobalId", "type": "IfcGloballyUniqueId", "is_enum": false, "enum_values": []}, "Description": {"... (+475 chars omitted),+1 more (map truncated)
  IfcType = 7
  Length = 1570
  MoveBase = false
  MoveWithHost = false
  Nodes = (2) [(-1.72563e-31,-1.42109e-15,-7.77156e-16),(1570,-1.42109e-15,-7.77156e-16)]
  NodesOffset = 0
  Normal = (0,0,0)
  PerimeterLength = 3440
  Placement = pos=(13655,5970,8800) rot=(0,0,1;3.14159rad)
  PredefinedType = 0
  VerticalArea = 1.376e+06
  Width = 150
FEATURE [Part::FeaturePython] Structure270  label="V15x40 V170"  # Arch/BIM 7 (typed FeaturePython)
  FaceMaker = 0
  Height = 400
  HorizontalArea = 177000
  IfcData = attributes={"GlobalId": {"name": "GlobalId", "type": "IfcGloballyUniqueId", "is_enum": false, "enum_values": []}, "Description": {"... (+475 chars omitted),+1 more (map truncated)
  IfcType = 7
  Length = 1180
  MoveBase = false
  MoveWithHost = false
  Nodes = (2) [(-1.72563e-31,-1.42109e-15,-7.77156e-16),(1180,-1.42109e-15,-7.77156e-16)]
  NodesOffset = 0
  Normal = (0,0,0)
  PerimeterLength = 2660
  Placement = pos=(13905,5970,8800) rot=(0,0,1;0rad)
  PredefinedType = 0
  VerticalArea = 1064000
  Width = 150
FEATURE [Part::FeaturePython] Structure271  label="V15x40 V171"  # Arch/BIM 7 (typed FeaturePython)
  FaceMaker = 0
  Height = 400
  HorizontalArea = 597000
  IfcData = attributes={"GlobalId": {"name": "GlobalId", "type": "IfcGloballyUniqueId", "is_enum": false, "enum_values": []}, "Description": {"... (+475 chars omitted),+1 more (map truncated)
  IfcType = 7
  Length = 3980
  MoveBase = false
  MoveWithHost = false
  Nodes = (2) [(-1.72563e-31,-1.42109e-15,-7.77156e-16),(3980,-1.42109e-15,-7.77156e-16)]
  NodesOffset = 0
  Normal = (0,0,0)
  PerimeterLength = 8260
  Placement = pos=(2055,3350,8800) rot=(0,0,1;0rad)
  PredefinedType = 0
  VerticalArea = 3.304e+06
  Width = 150
FEATURE [Part::FeaturePython] Structure272  label="V15x40 V172"  # Arch/BIM 7 (typed FeaturePython)
  FaceMaker = 0
  Height = 400
  HorizontalArea = 397500
  IfcData = attributes={"GlobalId": {"name": "GlobalId", "type": "IfcGloballyUniqueId", "is_enum": false, "enum_values": []}, "Description": {"... (+475 chars omitted),+1 more (map truncated)
  IfcType = 7
  Length = 2650
  MoveBase = false
  MoveWithHost = false
  Nodes = (2) [(-1.72563e-31,-1.42109e-15,-7.77156e-16),(2650,-1.42109e-15,-7.77156e-16)]
  NodesOffset = 0
  Normal = (0,0,0)
  PerimeterLength = 5600
  Placement = pos=(6285,3350,8800) rot=(0,0,1;0rad)
  PredefinedType = 0
  VerticalArea = 2240000
  Width = 150
FEATURE [Part::FeaturePython] Structure273  label="V15x40 V173"  # Arch/BIM 7 (typed FeaturePython)
  FaceMaker = 0
  Height = 400
  HorizontalArea = 210000
  IfcData = attributes={"GlobalId": {"name": "GlobalId", "type": "IfcGloballyUniqueId", "is_enum": false, "enum_values": []}, "Description": {"... (+475 chars omitted),+1 more (map truncated)
  IfcType = 7
  Length = 1400
  MoveBase = false
  MoveWithHost = false
  Nodes = (2) [(-1.72563e-31,-1.42109e-15,-7.77156e-16),(1400,-1.42109e-15,-7.77156e-16)]
  NodesOffset = 0
  Normal = (0,0,0)
  PerimeterLength = 3100
  Placement = pos=(9085,3350,8800) rot=(0,0,1;0rad)
  PredefinedType = 0
  VerticalArea = 1240000
  Width = 150
FEATURE [Part::FeaturePython] Structure274  label="V15x40 V174"  # Arch/BIM 7 (typed FeaturePython)
  FaceMaker = 0
  Height = 400
  HorizontalArea = 460500
  IfcData = attributes={"GlobalId": {"name": "GlobalId", "type": "IfcGloballyUniqueId", "is_enum": false, "enum_values": []}, "Description": {"... (+475 chars omitted),+1 more (map truncated)
  IfcType = 7
  Length = 3070
  MoveBase = false
  MoveWithHost = false
  Nodes = (2) [(-1.72563e-31,-1.42109e-15,-7.77156e-16),(3070,-1.42109e-15,-7.77156e-16)]
  NodesOffset = 0
  Normal = (0,0,0)
  PerimeterLength = 6440
  Placement = pos=(10635,3350,8800) rot=(0,0,1;0rad)
  PredefinedType = 0
  VerticalArea = 2.576e+06
  Width = 150
FEATURE [Part::FeaturePython] Structure275  label="V15x40 V175"  # Arch/BIM 7 (typed FeaturePython)
  FaceMaker = 0
  Height = 400
  HorizontalArea = 597000
  IfcData = attributes={"GlobalId": {"name": "GlobalId", "type": "IfcGloballyUniqueId", "is_enum": false, "enum_values": []}, "Description": {"... (+475 chars omitted),+1 more (map truncated)
  IfcType = 7
  Length = 3980
  MoveBase = false
  MoveWithHost = false
  Nodes = (2) [(-1.72563e-31,-1.42109e-15,-7.77156e-16),(3980,-1.42109e-15,-7.77156e-16)]
  NodesOffset = 0
  Normal = (0,0,0)
  PerimeterLength = 8260
  Placement = pos=(2055,100,8800) rot=(0,0,1;0rad)
  PredefinedType = 0
  VerticalArea = 3.304e+06
  Width = 150
FEATURE [Part::FeaturePython] Structure276  label="V15x40 V176"  # Arch/BIM 7 (typed FeaturePython)
  FaceMaker = 0
  Height = 400
  HorizontalArea = 390000
  IfcData = attributes={"GlobalId": {"name": "GlobalId", "type": "IfcGloballyUniqueId", "is_enum": false, "enum_values": []}, "Description": {"... (+475 chars omitted),+1 more (map truncated)
  IfcType = 7
  Length = 2600
  MoveBase = false
  MoveWithHost = false
  Nodes = (2) [(-1.72563e-31,-1.42109e-15,-7.77156e-16),(2600,-1.42109e-15,-7.77156e-16)]
  NodesOffset = 0
  Normal = (0,0,0)
  PerimeterLength = 5500
  Placement = pos=(6285,100,8800) rot=(0,0,1;0rad)
  PredefinedType = 0
  VerticalArea = 2200000
  Width = 150
FEATURE [Part::FeaturePython] Structure277  label="V15x40 V177"  # Arch/BIM 7 (typed FeaturePython)
  FaceMaker = 0
  Height = 400
  HorizontalArea = 195000
  IfcData = attributes={"GlobalId": {"name": "GlobalId", "type": "IfcGloballyUniqueId", "is_enum": false, "enum_values": []}, "Description": {"... (+475 chars omitted),+1 more (map truncated)
  IfcType = 7
  Length = 1300
  MoveBase = false
  MoveWithHost = false
  Nodes = (2) [(-1.72563e-31,-1.42109e-15,-7.77156e-16),(1300,-1.42109e-15,-7.77156e-16)]
  NodesOffset = 0
  Normal = (0,0,0)
  PerimeterLength = 2900
  Placement = pos=(9135,100,8800) rot=(0,0,1;0rad)
  PredefinedType = 0
  VerticalArea = 1160000
  Width = 150
FEATURE [Part::FeaturePython] Structure278  label="V15x40 V178"  # Arch/BIM 7 (typed FeaturePython)
  FaceMaker = 0
  Height = 400
  HorizontalArea = 445500
  IfcData = attributes={"GlobalId": {"name": "GlobalId", "type": "IfcGloballyUniqueId", "is_enum": false, "enum_values": []}, "Description": {"... (+475 chars omitted),+1 more (map truncated)
  IfcType = 7
  Length = 2970
  MoveBase = false
  MoveWithHost = false
  Nodes = (2) [(-1.72563e-31,-1.42109e-15,-7.77156e-16),(2970,-1.42109e-15,-7.77156e-16)]
  NodesOffset = 0
  Normal = (0,0,0)
  PerimeterLength = 6240
  Placement = pos=(10685,100,8800) rot=(0,0,1;0rad)
  PredefinedType = 0
  VerticalArea = 2.496e+06
  Width = 150
FEATURE [Part::FeaturePython] Structure279  label="V15x40 V179"  # Arch/BIM 7 (typed FeaturePython)
  FaceMaker = 0
  Height = 400
  HorizontalArea = 465000
  IfcData = attributes={"GlobalId": {"name": "GlobalId", "type": "IfcGloballyUniqueId", "is_enum": false, "enum_values": []}, "Description": {"... (+475 chars omitted),+1 more (map truncated)
  IfcType = 7
  Length = 3100
  MoveBase = false
  MoveWithHost = false
  Nodes = (2) [(-1.72563e-31,-1.42109e-15,-7.77156e-16),(3100,-1.42109e-15,-7.77156e-16)]
  NodesOffset = 0
  Normal = (0,0,0)
  PerimeterLength = 6500
  Placement = pos=(6160,3275,8800) rot=(0,0,-1;1.5708rad)
  PredefinedType = 0
  VerticalArea = 2.6e+06
  Width = 150
FEATURE [Part::FeaturePython] Structure280  label="V15x40 V180"  # Arch/BIM 7 (typed FeaturePython)
  FaceMaker = 0
  Height = 400
  HorizontalArea = 471000
  IfcData = attributes={"GlobalId": {"name": "GlobalId", "type": "IfcGloballyUniqueId", "is_enum": false, "enum_values": []}, "Description": {"... (+475 chars omitted),+1 more (map truncated)
  IfcType = 7
  Length = 3140
  MoveBase = false
  MoveWithHost = false
  Nodes = (2) [(-1.72563e-31,-1.42109e-15,-7.77156e-16),(3140,-1.42109e-15,-7.77156e-16)]
  NodesOffset = 0
  Normal = (0,0,0)
  PerimeterLength = 6580
  Placement = pos=(6160,6565,8800) rot=(0,0,-1;1.5708rad)
  PredefinedType = 0
  VerticalArea = 2.632e+06
  Width = 150
FEATURE [Part::FeaturePython] Structure281  label="V15x40 V181"  # Arch/BIM 7 (typed FeaturePython)
  FaceMaker = 0
  Height = 400
  HorizontalArea = 466500
  IfcData = attributes={"GlobalId": {"name": "GlobalId", "type": "IfcGloballyUniqueId", "is_enum": false, "enum_values": []}, "Description": {"... (+475 chars omitted),+1 more (map truncated)
  IfcType = 7
  Length = 3110
  MoveBase = false
  MoveWithHost = false
  Nodes = (2) [(-1.72563e-31,-1.42109e-15,-7.77156e-16),(3110,-1.42109e-15,-7.77156e-16)]
  NodesOffset = 0
  Normal = (0,0,0)
  PerimeterLength = 6520
  Placement = pos=(6160,9825,8800) rot=(0,0,-1;1.5708rad)
  PredefinedType = 0
  VerticalArea = 2.608e+06
  Width = 150
FEATURE [Part::FeaturePython] Structure282  label="V15x40 V182"  # Arch/BIM 7 (typed FeaturePython)
  FaceMaker = 0
  Height = 400
  HorizontalArea = 457500
  IfcData = attributes={"GlobalId": {"name": "GlobalId", "type": "IfcGloballyUniqueId", "is_enum": false, "enum_values": []}, "Description": {"... (+475 chars omitted),+1 more (map truncated)
  IfcType = 7
  Length = 3050
  MoveBase = false
  MoveWithHost = false
  Nodes = (2) [(-1.72563e-31,-1.42109e-15,-7.77156e-16),(3050,-1.42109e-15,-7.77156e-16)]
  NodesOffset = 0
  Normal = (0,0,0)
  PerimeterLength = 6400
  Placement = pos=(9010,3225,8800) rot=(0,0,-1;1.5708rad)
  PredefinedType = 0
  VerticalArea = 2.56e+06
  Width = 150
FEATURE [Part::FeaturePython] Structure283  label="V15x40 V183"  # Arch/BIM 7 (typed FeaturePython)
  FaceMaker = 0
  Height = 400
  HorizontalArea = 456000
  IfcData = attributes={"GlobalId": {"name": "GlobalId", "type": "IfcGloballyUniqueId", "is_enum": false, "enum_values": []}, "Description": {"... (+475 chars omitted),+1 more (map truncated)
  IfcType = 7
  Length = 3040
  MoveBase = false
  MoveWithHost = false
  Nodes = (2) [(-1.72563e-31,-1.42109e-15,-7.77156e-16),(3040,-1.42109e-15,-7.77156e-16)]
  NodesOffset = 0
  Normal = (0,0,0)
  PerimeterLength = 6380
  Placement = pos=(9010,6515,8800) rot=(0,0,-1;1.5708rad)
  PredefinedType = 0
  VerticalArea = 2.552e+06
  Width = 150
FEATURE [Part::FeaturePython] Structure284  label="V15x40 V184"  # Arch/BIM 7 (typed FeaturePython)
  FaceMaker = 0
  Height = 400
  HorizontalArea = 459000
  IfcData = attributes={"GlobalId": {"name": "GlobalId", "type": "IfcGloballyUniqueId", "is_enum": false, "enum_values": []}, "Description": {"... (+475 chars omitted),+1 more (map truncated)
  IfcType = 7
  Length = 3060
  MoveBase = false
  MoveWithHost = false
  Nodes = (2) [(-1.72563e-31,-1.42109e-15,-7.77156e-16),(3060,-1.42109e-15,-7.77156e-16)]
  NodesOffset = 0
  Normal = (0,0,0)
  PerimeterLength = 6420
  Placement = pos=(9010,9825,8800) rot=(0,0,-1;1.5708rad)
  PredefinedType = 0
  VerticalArea = 2.568e+06
  Width = 150
FEATURE [Part::FeaturePython] Structure285  label="V15x40 V185"  # Arch/BIM 7 (typed FeaturePython)
  FaceMaker = 0
  Height = 400
  HorizontalArea = 457500
  IfcData = attributes={"GlobalId": {"name": "GlobalId", "type": "IfcGloballyUniqueId", "is_enum": false, "enum_values": []}, "Description": {"... (+475 chars omitted),+1 more (map truncated)
  IfcType = 7
  Length = 3050
  MoveBase = false
  MoveWithHost = false
  Nodes = (2) [(-1.72563e-31,-1.42109e-15,-7.77156e-16),(3050,-1.42109e-15,-7.77156e-16)]
  NodesOffset = 0
  Normal = (0,0,0)
  PerimeterLength = 6400
  Placement = pos=(10560,3225,8800) rot=(0,0,-1;1.5708rad)
  PredefinedType = 0
  VerticalArea = 2.56e+06
  Width = 150
FEATURE [Part::FeaturePython] Structure286  label="V15x40 V186"  # Arch/BIM 7 (typed FeaturePython)
  FaceMaker = 0
  Height = 400
  HorizontalArea = 363000
  IfcData = attributes={"GlobalId": {"name": "GlobalId", "type": "IfcGloballyUniqueId", "is_enum": false, "enum_values": []}, "Description": {"... (+475 chars omitted),+1 more (map truncated)
  IfcType = 7
  Length = 2420
  MoveBase = false
  MoveWithHost = false
  Nodes = (2) [(-1.72563e-31,-1.42109e-15,-7.77156e-16),(2420,-1.42109e-15,-7.77156e-16)]
  NodesOffset = 0
  Normal = (0,0,0)
  PerimeterLength = 5140
  Placement = pos=(10560,3475,8800) rot=(0,0,1;1.5708rad)
  PredefinedType = 0
  VerticalArea = 2056000
  Width = 150
FEATURE [Part::FeaturePython] Structure287  label="V15x40 V187"  # Arch/BIM 7 (typed FeaturePython)
  FaceMaker = 0
  Height = 400
  HorizontalArea = 207000
  IfcData = attributes={"GlobalId": {"name": "GlobalId", "type": "IfcGloballyUniqueId", "is_enum": false, "enum_values": []}, "Description": {"... (+475 chars omitted),+1 more (map truncated)
  IfcType = 7
  Length = 1380
  MoveBase = false
  MoveWithHost = false
  Nodes = (2) [(-1.72563e-31,-1.42109e-15,-7.77156e-16),(1380,-1.42109e-15,-7.77156e-16)]
  NodesOffset = 0
  Normal = (0,0,0)
  PerimeterLength = 3060
  Placement = pos=(10560,8445,8800) rot=(0,0,1;1.5708rad)
  PredefinedType = 0
  VerticalArea = 1224000
  Width = 150
FEATURE [Part::FeaturePython] Structure288  label="V15x40 V188"  # Arch/BIM 7 (typed FeaturePython)
  FaceMaker = 0
  Height = 400
  HorizontalArea = 207000
  IfcData = attributes={"GlobalId": {"name": "GlobalId", "type": "IfcGloballyUniqueId", "is_enum": false, "enum_values": []}, "Description": {"... (+475 chars omitted),+1 more (map truncated)
  IfcType = 7
  Length = 1380
  MoveBase = false
  MoveWithHost = false
  Nodes = (2) [(-1.72563e-31,-1.42109e-15,-7.77156e-16),(1380,-1.42109e-15,-7.77156e-16)]
  NodesOffset = 0
  Normal = (0,0,0)
  PerimeterLength = 3060
  Placement = pos=(12010,9825,8800) rot=(0,0,-1;1.5708rad)
  PredefinedType = 0
  VerticalArea = 1224000
  Width = 150
FEATURE [Part::FeaturePython] Structure289  label="V20x40 V142"  # Arch/BIM 7 (typed FeaturePython)
  FaceMaker = 0
  Height = 400
  HorizontalArea = 615000
  IfcData = attributes={"GlobalId": {"name": "GlobalId", "type": "IfcGloballyUniqueId", "is_enum": false, "enum_values": []}, "Description": {"... (+475 chars omitted),+1 more (map truncated)
  IfcType = 7
  Length = 3075
  MoveBase = false
  MoveWithHost = false
  Nodes = (2) [(-1.72563e-31,0,-7.77156e-16),(3075,0,-7.77156e-16)]
  NodesOffset = 0
  Normal = (0,0,0)
  PerimeterLength = 6550
  Placement = pos=(1930,3250,8800) rot=(0,0,-1;1.5708rad)
  PredefinedType = 0
  VerticalArea = 2.62e+06
  Width = 200
FEATURE [Part::FeaturePython] Structure290  label="V20x40 V143"  # Arch/BIM 7 (typed FeaturePython)
  FaceMaker = 0
  Height = 400
  HorizontalArea = 618000
  IfcData = attributes={"GlobalId": {"name": "GlobalId", "type": "IfcGloballyUniqueId", "is_enum": false, "enum_values": []}, "Description": {"... (+475 chars omitted),+1 more (map truncated)
  IfcType = 7
  Length = 3090
  MoveBase = false
  MoveWithHost = false
  Nodes = (2) [(-1.72563e-31,0,-7.77156e-16),(3090,0,-7.77156e-16)]
  NodesOffset = 0
  Normal = (0,0,0)
  PerimeterLength = 6580
  Placement = pos=(1930,6540,8800) rot=(0,0,-1;1.5708rad)
  PredefinedType = 0
  VerticalArea = 2.632e+06
  Width = 200
FEATURE [Part::FeaturePython] Structure291  label="V20x40 V144"  # Arch/BIM 7 (typed FeaturePython)
  FaceMaker = 0
  Height = 400
  HorizontalArea = 617000
  IfcData = attributes={"GlobalId": {"name": "GlobalId", "type": "IfcGloballyUniqueId", "is_enum": false, "enum_values": []}, "Description": {"... (+475 chars omitted),+1 more (map truncated)
  IfcType = 7
  Length = 3085
  MoveBase = false
  MoveWithHost = false
  Nodes = (2) [(-1.72563e-31,0,-7.77156e-16),(3085,0,-7.77156e-16)]
  NodesOffset = 0
  Normal = (0,0,0)
  PerimeterLength = 6570
  Placement = pos=(1930,9825,8800) rot=(0,0,-1;1.5708rad)
  PredefinedType = 0
  VerticalArea = 2.628e+06
  Width = 200
FEATURE [Part::FeaturePython] Structure292  label="V20x40 V145"  # Arch/BIM 7 (typed FeaturePython)
  FaceMaker = 0
  Height = 400
  HorizontalArea = 635000
  IfcData = attributes={"GlobalId": {"name": "GlobalId", "type": "IfcGloballyUniqueId", "is_enum": false, "enum_values": []}, "Description": {"... (+475 chars omitted),+1 more (map truncated)
  IfcType = 7
  Length = 3175
  MoveBase = false
  MoveWithHost = false
  Nodes = (2) [(-1.72563e-31,0,-7.77156e-16),(3175,0,-7.77156e-16)]
  NodesOffset = 0
  Normal = (0,0,0)
  PerimeterLength = 6750
  Placement = pos=(13780,175,8800) rot=(0,0,1;1.5708rad)
  PredefinedType = 0
  VerticalArea = 2.7e+06
  Width = 200
FEATURE [Part::FeaturePython] Structure293  label="V20x40 V146"  # Arch/BIM 7 (typed FeaturePython)
  FaceMaker = 0
  Height = 400
  HorizontalArea = 509000
  IfcData = attributes={"GlobalId": {"name": "GlobalId", "type": "IfcGloballyUniqueId", "is_enum": false, "enum_values": []}, "Description": {"... (+475 chars omitted),+1 more (map truncated)
  IfcType = 7
  Length = 2545
  MoveBase = false
  MoveWithHost = false
  Nodes = (2) [(-1.72563e-31,0,-7.77156e-16),(2545,0,-7.77156e-16)]
  NodesOffset = 0
  Normal = (0,0,0)
  PerimeterLength = 5490
  Placement = pos=(13780,3350,8800) rot=(0,0,1;1.5708rad)
  PredefinedType = 0
  VerticalArea = 2196000
  Width = 200
FEATURE [Part::FeaturePython] Structure294  label="V20x40 V147"  # Arch/BIM 7 (typed FeaturePython)
  FaceMaker = 0
  Height = 400
  HorizontalArea = 756000
  IfcData = attributes={"GlobalId": {"name": "GlobalId", "type": "IfcGloballyUniqueId", "is_enum": false, "enum_values": []}, "Description": {"... (+475 chars omitted),+1 more (map truncated)
  IfcType = 7
  Length = 3780
  MoveBase = false
  MoveWithHost = false
  Nodes = (2) [(-1.72563e-31,0,-7.77156e-16),(3780,0,-7.77156e-16)]
  NodesOffset = 0
  Normal = (0,0,0)
  PerimeterLength = 7960
  Placement = pos=(15210,6045,8800) rot=(0,0,1;1.5708rad)
  PredefinedType = 0
  VerticalArea = 3.184e+06
  Width = 200
FEATURE [Part::FeaturePython] Structure295  label="L135"  # Arch/BIM 172 (typed FeaturePython)
  Base = -> Rectangle004
  FaceMaker = 0
  Height = 150
  HorizontalArea = 12611050
  IfcData = attributes={"GlobalId": {"name": "GlobalId", "type": "IfcGloballyUniqueId", "is_enum": false, "enum_values": []}, "Description": {"... (+484 chars omitted),+1 more (map truncated)
  IfcType = 172
  Length = 0
  MoveBase = false
  MoveWithHost = false
  Nodes = (2) [(4057.5,8270,3000),(4057.5,8270,2850)]
  NodesOffset = 0
  Normal = (0,0,-1)
  PerimeterLength = 14330
  Placement = pos=(0,0,6000) rot=(0,0,1;0rad)
  PredefinedType = 0
  VerticalArea = 2149500
  Width = 150
FEATURE [Part::FeaturePython] Structure296  label="L136"  # Arch/BIM 172 (typed FeaturePython)
  Base = -> Rectangle005
  FaceMaker = 0
  Height = 150
  HorizontalArea = 12732700
  IfcData = attributes={"GlobalId": {"name": "GlobalId", "type": "IfcGloballyUniqueId", "is_enum": false, "enum_values": []}, "Description": {"... (+484 chars omitted),+1 more (map truncated)
  IfcType = 172
  Length = 0
  MoveBase = false
  MoveWithHost = false
  Nodes = (2) [(4057.5,4995,3000),(4057.5,4995,2850)]
  NodesOffset = 0
  Normal = (0,0,-1)
  PerimeterLength = 14390
  Placement = pos=(0,0,6000) rot=(0,0,1;0rad)
  PredefinedType = 0
  VerticalArea = 2158500
  Width = 150
FEATURE [Part::FeaturePython] Structure297  label="L137"  # Arch/BIM 172 (typed FeaturePython)
  Base = -> Rectangle006
  FaceMaker = 0
  Height = 150
  HorizontalArea = 1.25705e+07
  IfcData = attributes={"GlobalId": {"name": "GlobalId", "type": "IfcGloballyUniqueId", "is_enum": false, "enum_values": []}, "Description": {"... (+484 chars omitted),+1 more (map truncated)
  IfcType = 172
  Length = 0
  MoveBase = false
  MoveWithHost = false
  Nodes = (2) [(4057.5,1725,3000),(4057.5,1725,2850)]
  NodesOffset = 0
  Normal = (0,0,-1)
  PerimeterLength = 14310
  Placement = pos=(0,0,6000) rot=(0,0,1;0rad)
  PredefinedType = 0
  VerticalArea = 2146500
  Width = 150
FEATURE [Part::FeaturePython] Structure298  label="V15x40 V102a002"  # Arch/BIM 7 (typed FeaturePython)
  FaceMaker = 0
  Height = 400
  HorizontalArea = 405000
  IfcData = attributes={"GlobalId": {"name": "GlobalId", "type": "IfcGloballyUniqueId", "is_enum": false, "enum_values": []}, "Description": {"... (+475 chars omitted),+1 more (map truncated)
  IfcType = 7
  Length = 2700
  MoveBase = false
  MoveWithHost = false
  Nodes = (2) [(-1.72563e-31,-1.42109e-15,-7.77156e-16),(2700,-1.42109e-15,-7.77156e-16)]
  NodesOffset = 0
  Normal = (0,0,0)
  PerimeterLength = 5700
  Placement = pos=(8935,8295,8800) rot=(0,0,1;3.14159rad)
  PredefinedType = 0
  VerticalArea = 2.28e+06
  Width = 150
FEATURE [Part::FeaturePython] Structure299  label="V15x40 V107a002"  # Arch/BIM 7 (typed FeaturePython)
  FaceMaker = 0
  Height = 400
  HorizontalArea = 405000
  IfcData = attributes={"GlobalId": {"name": "GlobalId", "type": "IfcGloballyUniqueId", "is_enum": false, "enum_values": []}, "Description": {"... (+475 chars omitted),+1 more (map truncated)
  IfcType = 7
  Length = 2700
  MoveBase = false
  MoveWithHost = false
  Nodes = (2) [(-1.72563e-31,-1.42109e-15,-7.77156e-16),(2700,-1.42109e-15,-7.77156e-16)]
  NodesOffset = 0
  Normal = (0,0,0)
  PerimeterLength = 5700
  Placement = pos=(8935,4995,8800) rot=(0,0,1;3.14159rad)
  PredefinedType = 0
  VerticalArea = 2.28e+06
  Width = 150
FEATURE [Part::FeaturePython] Structure300  label="V15x40 V112a002"  # Arch/BIM 7 (typed FeaturePython)
  FaceMaker = 0
  Height = 400
  HorizontalArea = 405000
  IfcData = attributes={"GlobalId": {"name": "GlobalId", "type": "IfcGloballyUniqueId", "is_enum": false, "enum_values": []}, "Description": {"... (+475 chars omitted),+1 more (map truncated)
  IfcType = 7
  Length = 2700
  MoveBase = false
  MoveWithHost = false
  Nodes = (2) [(-1.72563e-31,-1.42109e-15,-7.77156e-16),(2700,-1.42109e-15,-7.77156e-16)]
  NodesOffset = 0
  Normal = (0,0,0)
  PerimeterLength = 5700
  Placement = pos=(8935,1700,8800) rot=(0,0,1;3.14159rad)
  PredefinedType = 0
  VerticalArea = 2.28e+06
  Width = 150
FEATURE [Part::FeaturePython] Structure301  label="V15x40 V130a002"  # Arch/BIM 7 (typed FeaturePython)
  FaceMaker = 0
  Height = 400
  HorizontalArea = 370500
  IfcData = attributes={"GlobalId": {"name": "GlobalId", "type": "IfcGloballyUniqueId", "is_enum": false, "enum_values": []}, "Description": {"... (+475 chars omitted),+1 more (map truncated)
  IfcType = 7
  Length = 2470
  MoveBase = false
  MoveWithHost = false
  Nodes = (2) [(-1.72563e-31,-1.42109e-15,-7.77156e-16),(2470,-1.42109e-15,-7.77156e-16)]
  NodesOffset = 0
  Normal = (0,0,0)
  PerimeterLength = 5240
  Placement = pos=(12010,3425,8800) rot=(0,0,1;1.5708rad)
  PredefinedType = 0
  VerticalArea = 2096000
  Width = 150
FEATURE [App::GeometryPython] BuildingPart017  label="Vigas sobre P2"  # Arch/BIM 172 (typed FeaturePython)
  Area = 0
  Group = -> [Structure298,Structure299,Structure300,Structure301,Structure261,Structure262,Structure263,Structure264,Structure265,Structure266,Structure267,Structure268,Structure269,Structure270,Structure271,Structure272,Structure273,Structure274,Structure275,Structure276,Structure277,Structure278,Structure279,Structure280,Structure281,Structure282,Structure283,Structure284,Structure285,Structure286,+8 more]
  Height = 0
  HeightPropagate = true
  IfcData = attributes={"GlobalId": {"name": "GlobalId", "type": "IfcGloballyUniqueId", "is_enum": false, "enum_values": []}, "Description": {"... (+484 chars omitted),+1 more (map truncated)
  IfcType = 172
  LevelOffset = 0
  PredefinedType = 0
FEATURE [Part::FeaturePython] Structure302  label="L138"  # Arch/BIM 172 (typed FeaturePython)
  Base = -> Rectangle014
  FaceMaker = 0
  Height = 150
  HorizontalArea = 3928500
  IfcData = attributes={"GlobalId": {"name": "GlobalId", "type": "IfcGloballyUniqueId", "is_enum": false, "enum_values": []}, "Description": {"... (+484 chars omitted),+1 more (map truncated)
  IfcType = 172
  Length = 0
  MoveBase = false
  MoveWithHost = false
  Nodes = (2) [(7585,9097.5,3000),(7585,9097.5,2850)]
  NodesOffset = 0
  Normal = (0,0,-1)
  PerimeterLength = 8310
  Placement = pos=(0,0,6000) rot=(0,0,1;0rad)
  PredefinedType = 0
  VerticalArea = 1246500
  Width = 150
FEATURE [Part::FeaturePython] Structure303  label="L139"  # Arch/BIM 172 (typed FeaturePython)
  Base = -> Wire
  FaceMaker = 0
  Height = 150
  HorizontalArea = 3.9285e+06
  IfcData = attributes={"GlobalId": {"name": "GlobalId", "type": "IfcGloballyUniqueId", "is_enum": false, "enum_values": []}, "Description": {"... (+484 chars omitted),+1 more (map truncated)
  IfcType = 172
  Length = 0
  MoveBase = false
  MoveWithHost = false
  Nodes = (2) [(7543.76,7449.37,3000),(7543.76,7449.37,2850)]
  NodesOffset = 0
  Normal = (0,0,-1)
  PerimeterLength = 8410
  Placement = pos=(0,0,5850) rot=(0,0,1;0rad)
  PredefinedType = 0
  VerticalArea = 1261500
  Width = 150
FEATURE [Part::FeaturePython] Structure304  label="L140"  # Arch/BIM 172 (typed FeaturePython)
  Base = -> Wire001
  FaceMaker = 0
  Height = 150
  HorizontalArea = 3.90134e+06
  IfcData = attributes={"GlobalId": {"name": "GlobalId", "type": "IfcGloballyUniqueId", "is_enum": false, "enum_values": []}, "Description": {"... (+484 chars omitted),+1 more (map truncated)
  IfcType = 172
  Length = 0
  MoveBase = false
  MoveWithHost = false
  Nodes = (2) [(7543.46,5835.61,3000),(7543.46,5835.61,2850)]
  NodesOffset = 0
  Normal = (0,0,-1)
  PerimeterLength = 8389.89
  Placement = pos=(0,0,5850) rot=(0,0,1;0rad)
  PredefinedType = 0
  VerticalArea = 1.25848e+06
  Width = 150
FEATURE [Part::FeaturePython] Structure305  label="L141"  # Arch/BIM 172 (typed FeaturePython)
  Base = -> Rectangle015
  FaceMaker = 0
  Height = 150
  HorizontalArea = 4.0365e+06
  IfcData = attributes={"GlobalId": {"name": "GlobalId", "type": "IfcGloballyUniqueId", "is_enum": false, "enum_values": []}, "Description": {"... (+484 chars omitted),+1 more (map truncated)
  IfcType = 172
  Length = 0
  MoveBase = false
  MoveWithHost = false
  Nodes = (2) [(7585,4172.5,3000),(7585,4172.5,2850)]
  NodesOffset = 0
  Normal = (0,0,-1)
  PerimeterLength = 8390
  Placement = pos=(0,0,6000) rot=(0,0,1;0rad)
  PredefinedType = 0
  VerticalArea = 1258500
  Width = 150
FEATURE [Part::FeaturePython] Structure306  label="L142"  # Arch/BIM 172 (typed FeaturePython)
  Base = -> Wire002
  FaceMaker = 0
  Height = 150
  HorizontalArea = 3.91484e+06
  IfcData = attributes={"GlobalId": {"name": "GlobalId", "type": "IfcGloballyUniqueId", "is_enum": false, "enum_values": []}, "Description": {"... (+484 chars omitted),+1 more (map truncated)
  IfcType = 172
  Length = 0
  MoveBase = false
  MoveWithHost = false
  Nodes = (2) [(7543.6,2543.13,3000),(7543.6,2543.13,2850)]
  NodesOffset = 0
  Normal = (0,0,-1)
  PerimeterLength = 8399.89
  Placement = pos=(0,0,5850) rot=(0,0,1;0rad)
  PredefinedType = 0
  VerticalArea = 1.25998e+06
  Width = 150
FEATURE [Part::FeaturePython] Structure307  label="L143"  # Arch/BIM 172 (typed FeaturePython)
  Base = -> Rectangle016
  FaceMaker = 0
  Height = 150
  HorizontalArea = 3.915e+06
  IfcData = attributes={"GlobalId": {"name": "GlobalId", "type": "IfcGloballyUniqueId", "is_enum": false, "enum_values": []}, "Description": {"... (+484 chars omitted),+1 more (map truncated)
  IfcType = 172
  Length = 0
  MoveBase = false
  MoveWithHost = false
  Nodes = (2) [(7585,900,3000),(7585,900,2850)]
  NodesOffset = 0
  Normal = (0,0,-1)
  PerimeterLength = 8300
  Placement = pos=(0,0,6000) rot=(0,0,1;0rad)
  PredefinedType = 0
  VerticalArea = 1.245e+06
  Width = 150
FEATURE [Part::FeaturePython] Structure308  label="L144"  # Arch/BIM 172 (typed FeaturePython)
  Base = -> Rectangle008
  FaceMaker = 0
  Height = 150
  HorizontalArea = 4354000
  IfcData = attributes={"GlobalId": {"name": "GlobalId", "type": "IfcGloballyUniqueId", "is_enum": false, "enum_values": []}, "Description": {"... (+484 chars omitted),+1 more (map truncated)
  IfcType = 172
  Length = 0
  MoveBase = false
  MoveWithHost = false
  Nodes = (2) [(9785,8270,3000),(9785,8270,2850)]
  NodesOffset = 0
  Normal = (0,0,-1)
  PerimeterLength = 9020
  Placement = pos=(0,0,6000) rot=(0,0,1;0rad)
  PredefinedType = 0
  VerticalArea = 1353000
  Width = 150
FEATURE [Part::FeaturePython] Structure309  label="L145"  # Arch/BIM 172 (typed FeaturePython)
  Base = -> Rectangle011
  FaceMaker = 0
  Height = 150
  HorizontalArea = 4396000
  IfcData = attributes={"GlobalId": {"name": "GlobalId", "type": "IfcGloballyUniqueId", "is_enum": false, "enum_values": []}, "Description": {"... (+484 chars omitted),+1 more (map truncated)
  IfcType = 172
  Length = 0
  MoveBase = false
  MoveWithHost = false
  Nodes = (2) [(9785,4995,3000),(9785,4995,2850)]
  NodesOffset = 0
  Normal = (0,0,-1)
  PerimeterLength = 9080
  Placement = pos=(0,0,6000) rot=(0,0,1;0rad)
  PredefinedType = 0
  VerticalArea = 1362000
  Width = 150
FEATURE [Part::FeaturePython] Structure310  label="L146"  # Arch/BIM 172 (typed FeaturePython)
  Base = -> Rectangle013
  FaceMaker = 0
  Height = 150
  HorizontalArea = 4.34e+06
  IfcData = attributes={"GlobalId": {"name": "GlobalId", "type": "IfcGloballyUniqueId", "is_enum": false, "enum_values": []}, "Description": {"... (+484 chars omitted),+1 more (map truncated)
  IfcType = 172
  Length = 0
  MoveBase = false
  MoveWithHost = false
  Nodes = (2) [(9785,1725,3000),(9785,1725,2850)]
  NodesOffset = 0
  Normal = (0,0,-1)
  PerimeterLength = 9000
  Placement = pos=(0,0,6000) rot=(0,0,1;0rad)
  PredefinedType = 0
  VerticalArea = 1350000
  Width = 150
FEATURE [Part::FeaturePython] Structure311  label="L147"  # Arch/BIM 172 (typed FeaturePython)
  Base = -> Rectangle009
  FaceMaker = 0
  Height = 150
  HorizontalArea = 1.794e+06
  IfcData = attributes={"GlobalId": {"name": "GlobalId", "type": "IfcGloballyUniqueId", "is_enum": false, "enum_values": []}, "Description": {"... (+484 chars omitted),+1 more (map truncated)
  IfcType = 172
  Length = 0
  MoveBase = false
  MoveWithHost = false
  Nodes = (2) [(11285,9135,3000),(11285,9135,2850)]
  NodesOffset = 0
  Normal = (0,0,-1)
  PerimeterLength = 5360
  Placement = pos=(0,0,6000) rot=(0,0,1;0rad)
  PredefinedType = 0
  VerticalArea = 804000
  Width = 150
FEATURE [Part::FeaturePython] Structure312  label="L148"  # Arch/BIM 172 (typed FeaturePython)
  Base = -> Rectangle018
  FaceMaker = 0
  Height = 150
  HorizontalArea = 3.211e+06
  IfcData = attributes={"GlobalId": {"name": "GlobalId", "type": "IfcGloballyUniqueId", "is_enum": false, "enum_values": []}, "Description": {"... (+484 chars omitted),+1 more (map truncated)
  IfcType = 172
  Length = 0
  MoveBase = false
  MoveWithHost = false
  Nodes = (2) [(11285,4660,3000),(11285,4660,2850)]
  NodesOffset = 0
  Normal = (0,0,-1)
  PerimeterLength = 7540
  Placement = pos=(0,0,5850) rot=(0,0,1;0rad)
  PredefinedType = 0
  VerticalArea = 1.131e+06
  Width = 150
FEATURE [Part::FeaturePython] Structure313  label="L149"  # Arch/BIM 172 (typed FeaturePython)
  Base = -> Rectangle020
  FaceMaker = 0
  Height = 150
  HorizontalArea = 9439500
  IfcData = attributes={"GlobalId": {"name": "GlobalId", "type": "IfcGloballyUniqueId", "is_enum": false, "enum_values": []}, "Description": {"... (+484 chars omitted),+1 more (map truncated)
  IfcType = 172
  Length = 0
  MoveBase = false
  MoveWithHost = false
  Nodes = (2) [(12157.5,1725,3000),(12157.5,1725,2850)]
  NodesOffset = 0
  Normal = (0,0,-1)
  PerimeterLength = 12290
  Placement = pos=(0,0,6000) rot=(0,0,1;0rad)
  PredefinedType = 0
  VerticalArea = 1843500
  Width = 150
FEATURE [Part::FeaturePython] Structure314  label="L150"  # Arch/BIM 172 (typed FeaturePython)
  Base = -> Rectangle019
  FaceMaker = 0
  Height = 150
  HorizontalArea = 3.93965e+06
  IfcData = attributes={"GlobalId": {"name": "GlobalId", "type": "IfcGloballyUniqueId", "is_enum": false, "enum_values": []}, "Description": {"... (+484 chars omitted),+1 more (map truncated)
  IfcType = 172
  Length = 0
  MoveBase = false
  MoveWithHost = false
  Nodes = (2) [(12882.5,4660,3000),(12882.5,4660,2850)]
  NodesOffset = 0
  Normal = (0,0,-1)
  PerimeterLength = 8130
  Placement = pos=(0,0,6000) rot=(0,0,1;0rad)
  PredefinedType = 0
  VerticalArea = 1.2195e+06
  Width = 150
FEATURE [Part::FeaturePython] Structure315  label="L151"  # Arch/BIM 172 (typed FeaturePython)
  Base = -> Rectangle017
  FaceMaker = 0
  Height = 150
  HorizontalArea = 4174500
  IfcData = attributes={"GlobalId": {"name": "GlobalId", "type": "IfcGloballyUniqueId", "is_enum": false, "enum_values": []}, "Description": {"... (+484 chars omitted),+1 more (map truncated)
  IfcType = 172
  Length = 0
  MoveBase = false
  MoveWithHost = false
  Nodes = (2) [(13597.5,9135,3000),(13597.5,9135,2850)]
  NodesOffset = 0
  Normal = (0,0,-1)
  PerimeterLength = 8810
  Placement = pos=(0,0,6000) rot=(0,0,1;0rad)
  PredefinedType = 0
  VerticalArea = 1321500
  Width = 150
FEATURE [App::GeometryPython] BuildingPart018  label="Losas sobre P2"  # Arch/BIM 172 (typed FeaturePython)
  Area = 0
  Group = -> [Structure295,Structure296,Structure297,Structure302,Structure303,Structure304,Structure305,Structure306,Structure307,Structure308,Structure309,Structure310,Structure311,Structure312,Structure313,Structure314,Structure315]
  Height = 0
  HeightPropagate = true
  IfcData = attributes={"GlobalId": {"name": "GlobalId", "type": "IfcGloballyUniqueId", "is_enum": false, "enum_values": []}, "Description": {"... (+484 chars omitted),+1 more (map truncated)
  IfcType = 172
  LevelOffset = 0
  PredefinedType = 0
FEATURE [App::GeometryPython] BuildingPart010  label="Piso 2"  # Arch/BIM 172 (typed FeaturePython)
  Area = 24900000
  Group = -> [BuildingPart016,BuildingPart018,Wall003,BuildingPart017]
  Height = 0
  HeightPropagate = true
  IfcData = attributes={"GlobalId": {"name": "GlobalId", "type": "IfcGloballyUniqueId", "is_enum": false, "enum_values": []}, "Description": {"... (+484 chars omitted),+1 more (map truncated)
  IfcType = 172
  LevelOffset = 0
  Placement = pos=(0,0,6000) rot=(0,0,1;0rad)
  PredefinedType = 0
FEATURE [Part::FeaturePython] Structure316  label="25x15 C064"  # Arch/BIM 24 (typed FeaturePython)
  FaceMaker = 0
  Height = 3000
  HorizontalArea = 37500
  IfcData = attributes={"GlobalId": {"name": "GlobalId", "type": "IfcGloballyUniqueId", "is_enum": false, "enum_values": []}, "Description": {"... (+438 chars omitted),+1 more (map truncated)
  IfcType = 24
  Length = 250
  MoveBase = false
  MoveWithHost = false
  Nodes = (2) [(-1.05471e-15,1.36424e-15,0),(-1.05471e-15,1.36424e-15,3000)]
  NodesOffset = 0
  Normal = (0,0,0)
  PerimeterLength = 800
  Placement = pos=(1930,9900,9000) rot=(0,0,1;0rad)
  PredefinedType = 0
  VerticalArea = 2400000
  Width = 150
FEATURE [Part::FeaturePython] Structure317  label="25x15 C065"  # Arch/BIM 172 (typed FeaturePython)
  FaceMaker = 0
  Height = 3000
  HorizontalArea = 37500
  IfcData = attributes={"GlobalId": {"name": "GlobalId", "type": "IfcGloballyUniqueId", "is_enum": false, "enum_values": []}, "Description": {"... (+484 chars omitted),+1 more (map truncated)
  IfcType = 172
  Length = 250
  MoveBase = false
  MoveWithHost = false
  Nodes = (2) [(-1.05471e-15,1.36424e-15,0),(-1.05471e-15,1.36424e-15,3000)]
  NodesOffset = 0
  Normal = (0,0,0)
  PerimeterLength = 800
  Placement = pos=(1930,100,9000) rot=(0,0,1;0rad)
  PredefinedType = 0
  VerticalArea = 2400000
  Width = 150
FEATURE [Part::FeaturePython] Structure318  label="25x15 C066"  # Arch/BIM 24 (typed FeaturePython)
  FaceMaker = 0
  Height = 3000
  HorizontalArea = 37500
  IfcData = attributes={"GlobalId": {"name": "GlobalId", "type": "IfcGloballyUniqueId", "is_enum": false, "enum_values": []}, "Description": {"... (+438 chars omitted),+1 more (map truncated)
  IfcType = 24
  Length = 250
  MoveBase = false
  MoveWithHost = false
  Nodes = (2) [(-1.05471e-15,1.36424e-15,0),(-1.05471e-15,1.36424e-15,3000)]
  NodesOffset = 0
  Normal = (0,0,0)
  PerimeterLength = 800
  Placement = pos=(6160,6640,9000) rot=(0,0,1;0rad)
  PredefinedType = 0
  VerticalArea = 2400000
  Width = 150
FEATURE [Part::FeaturePython] Structure319  label="25x15 C067"  # Arch/BIM 24 (typed FeaturePython)
  FaceMaker = 0
  Height = 3000
  HorizontalArea = 37500
  IfcData = attributes={"GlobalId": {"name": "GlobalId", "type": "IfcGloballyUniqueId", "is_enum": false, "enum_values": []}, "Description": {"... (+438 chars omitted),+1 more (map truncated)
  IfcType = 24
  Length = 250
  MoveBase = false
  MoveWithHost = false
  Nodes = (2) [(-1.05471e-15,1.36424e-15,0),(-1.05471e-15,1.36424e-15,3000)]
  NodesOffset = 0
  Normal = (0,0,0)
  PerimeterLength = 800
  Placement = pos=(6160,3350,9000) rot=(0,0,1;0rad)
  PredefinedType = 0
  VerticalArea = 2400000
  Width = 150
FEATURE [Part::FeaturePython] Structure320  label="25x15 C068"  # Arch/BIM 24 (typed FeaturePython)
  FaceMaker = 0
  Height = 3000
  HorizontalArea = 37500
  IfcData = attributes={"GlobalId": {"name": "GlobalId", "type": "IfcGloballyUniqueId", "is_enum": false, "enum_values": []}, "Description": {"... (+438 chars omitted),+1 more (map truncated)
  IfcType = 24
  Length = 250
  MoveBase = false
  MoveWithHost = false
  Nodes = (2) [(-1.05471e-15,1.36424e-15,0),(-1.05471e-15,1.36424e-15,3000)]
  NodesOffset = 0
  Normal = (0,0,0)
  PerimeterLength = 800
  Placement = pos=(6160,100,9000) rot=(0,0,1;0rad)
  PredefinedType = 0
  VerticalArea = 2400000
  Width = 150
FEATURE [Part::FeaturePython] Structure321  label="25x15 C069"  # Arch/BIM 24 (typed FeaturePython)
  FaceMaker = 0
  Height = 3000
  HorizontalArea = 37500
  IfcData = attributes={"GlobalId": {"name": "GlobalId", "type": "IfcGloballyUniqueId", "is_enum": false, "enum_values": []}, "Description": {"... (+438 chars omitted),+1 more (map truncated)
  IfcType = 24
  Length = 250
  MoveBase = false
  MoveWithHost = false
  Nodes = (2) [(-1.05471e-15,1.36424e-15,0),(-1.05471e-15,1.36424e-15,3000)]
  NodesOffset = 0
  Normal = (0,0,0)
  PerimeterLength = 800
  Placement = pos=(9010,100,9000) rot=(0,0,1;0rad)
  PredefinedType = 0
  VerticalArea = 2400000
  Width = 150
FEATURE [Part::FeaturePython] Structure322  label="25x15 C070"  # Arch/BIM 24 (typed FeaturePython)
  FaceMaker = 0
  Height = 3000
  HorizontalArea = 37500
  IfcData = attributes={"GlobalId": {"name": "GlobalId", "type": "IfcGloballyUniqueId", "is_enum": false, "enum_values": []}, "Description": {"... (+438 chars omitted),+1 more (map truncated)
  IfcType = 24
  Length = 250
  MoveBase = false
  MoveWithHost = false
  Nodes = (2) [(-1.05471e-15,1.36424e-15,0),(-1.05471e-15,1.36424e-15,3000)]
  NodesOffset = 0
  Normal = (0,0,0)
  PerimeterLength = 800
  Placement = pos=(10560,100,9000) rot=(0,0,1;0rad)
  PredefinedType = 0
  VerticalArea = 2400000
  Width = 150
FEATURE [Part::FeaturePython] Structure323  label="25x15 C071"  # Arch/BIM 24 (typed FeaturePython)
  FaceMaker = 0
  Height = 3000
  HorizontalArea = 37500
  IfcData = attributes={"GlobalId": {"name": "GlobalId", "type": "IfcGloballyUniqueId", "is_enum": false, "enum_values": []}, "Description": {"... (+438 chars omitted),+1 more (map truncated)
  IfcType = 24
  Length = 250
  MoveBase = false
  MoveWithHost = false
  Nodes = (2) [(-1.05471e-15,1.36424e-15,0),(-1.05471e-15,1.36424e-15,3000)]
  NodesOffset = 0
  Normal = (0,0,0)
  PerimeterLength = 800
  Placement = pos=(13780,100,9000) rot=(0,0,1;0rad)
  PredefinedType = 0
  VerticalArea = 2400000
  Width = 150
FEATURE [Part::FeaturePython] Structure324  label="25x15 C072"  # Arch/BIM 24 (typed FeaturePython)
  FaceMaker = 0
  Height = 3000
  HorizontalArea = 37500
  IfcData = attributes={"GlobalId": {"name": "GlobalId", "type": "IfcGloballyUniqueId", "is_enum": false, "enum_values": []}, "Description": {"... (+438 chars omitted),+1 more (map truncated)
  IfcType = 24
  Length = 250
  MoveBase = false
  MoveWithHost = false
  Nodes = (2) [(-1.05471e-15,1.36424e-15,0),(-1.05471e-15,1.36424e-15,3000)]
  NodesOffset = 0
  Normal = (0,0,0)
  PerimeterLength = 800
  Placement = pos=(15210,5970,9000) rot=(0,0,1;0rad)
  PredefinedType = 0
  VerticalArea = 2400000
  Width = 150
FEATURE [Part::FeaturePython] Structure325  label="25x15 C073"  # Arch/BIM 24 (typed FeaturePython)
  FaceMaker = 0
  Height = 3000
  HorizontalArea = 37500
  IfcData = attributes={"GlobalId": {"name": "GlobalId", "type": "IfcGloballyUniqueId", "is_enum": false, "enum_values": []}, "Description": {"... (+438 chars omitted),+1 more (map truncated)
  IfcType = 24
  Length = 250
  MoveBase = false
  MoveWithHost = false
  Nodes = (2) [(-1.05471e-15,1.36424e-15,0),(-1.05471e-15,1.36424e-15,3000)]
  NodesOffset = 0
  Normal = (0,0,0)
  PerimeterLength = 800
  Placement = pos=(13780,5970,9000) rot=(0,0,1;0rad)
  PredefinedType = 0
  VerticalArea = 2400000
  Width = 150
FEATURE [Part::FeaturePython] Structure326  label="25x15 C074"  # Arch/BIM 172 (typed FeaturePython)
  FaceMaker = 0
  Height = 3000
  HorizontalArea = 37500
  IfcData = attributes={"GlobalId": {"name": "GlobalId", "type": "IfcGloballyUniqueId", "is_enum": false, "enum_values": []}, "Description": {"... (+484 chars omitted),+1 more (map truncated)
  IfcType = 172
  Length = 250
  MoveBase = false
  MoveWithHost = false
  Nodes = (2) [(-1.05471e-15,1.36424e-15,0),(-1.05471e-15,1.36424e-15,3000)]
  NodesOffset = 0
  Normal = (0,0,0)
  PerimeterLength = 800
  Placement = pos=(1930,9900,9000) rot=(0,0,1;0rad)
  PredefinedType = 0
  VerticalArea = 2400000
  Width = 150
FEATURE [Part::FeaturePython] Structure327  label="25x15 C075"  # Arch/BIM 172 (typed FeaturePython)
  FaceMaker = 0
  Height = 3000
  HorizontalArea = 37500
  IfcData = attributes={"GlobalId": {"name": "GlobalId", "type": "IfcGloballyUniqueId", "is_enum": false, "enum_values": []}, "Description": {"... (+484 chars omitted),+1 more (map truncated)
  IfcType = 172
  Length = 250
  MoveBase = false
  MoveWithHost = false
  Nodes = (2) [(-1.05471e-15,1.36424e-15,0),(-1.05471e-15,1.36424e-15,3000)]
  NodesOffset = 0
  Normal = (0,0,0)
  PerimeterLength = 800
  Placement = pos=(9010,6640,9000) rot=(0,0,1;1.5708rad)
  PredefinedType = 0
  VerticalArea = 2400000
  Width = 150
FEATURE [Part::FeaturePython] Structure328  label="25x15 C076"  # Arch/BIM 172 (typed FeaturePython)
  FaceMaker = 0
  Height = 3000
  HorizontalArea = 37500
  IfcData = attributes={"GlobalId": {"name": "GlobalId", "type": "IfcGloballyUniqueId", "is_enum": false, "enum_values": []}, "Description": {"... (+484 chars omitted),+1 more (map truncated)
  IfcType = 172
  Length = 250
  MoveBase = false
  MoveWithHost = false
  Nodes = (2) [(-1.05471e-15,1.36424e-15,0),(-1.05471e-15,1.36424e-15,3000)]
  NodesOffset = 0
  Normal = (0,0,0)
  PerimeterLength = 800
  Placement = pos=(9010,3350,9000) rot=(0,0,1;1.5708rad)
  PredefinedType = 0
  VerticalArea = 2400000
  Width = 150
FEATURE [Part::FeaturePython] Structure329  label="25x15 C077"  # Arch/BIM 172 (typed FeaturePython)
  FaceMaker = 0
  Height = 3000
  HorizontalArea = 37500
  IfcData = attributes={"GlobalId": {"name": "GlobalId", "type": "IfcGloballyUniqueId", "is_enum": false, "enum_values": []}, "Description": {"... (+484 chars omitted),+1 more (map truncated)
  IfcType = 172
  Length = 250
  MoveBase = false
  MoveWithHost = false
  Nodes = (2) [(-1.05471e-15,1.36424e-15,0),(-1.05471e-15,1.36424e-15,3000)]
  NodesOffset = 0
  Normal = (0,0,0)
  PerimeterLength = 800
  Placement = pos=(10560,3350,9000) rot=(0,0,1;1.5708rad)
  PredefinedType = 0
  VerticalArea = 2400000
  Width = 150
FEATURE [Part::FeaturePython] Structure330  label="25x15 C078"  # Arch/BIM 172 (typed FeaturePython)
  FaceMaker = 0
  Height = 3000
  HorizontalArea = 37500
  IfcData = attributes={"GlobalId": {"name": "GlobalId", "type": "IfcGloballyUniqueId", "is_enum": false, "enum_values": []}, "Description": {"... (+484 chars omitted),+1 more (map truncated)
  IfcType = 172
  Length = 250
  MoveBase = false
  MoveWithHost = false
  Nodes = (2) [(-1.05471e-15,1.36424e-15,0),(-1.05471e-15,1.36424e-15,3000)]
  NodesOffset = 0
  Normal = (0,0,0)
  PerimeterLength = 800
  Placement = pos=(13780,3350,9000) rot=(0,0,1;1.5708rad)
  PredefinedType = 0
  VerticalArea = 2400000
  Width = 150
FEATURE [Part::FeaturePython] Structure331  label="25x15 C079"  # Arch/BIM 172 (typed FeaturePython)
  FaceMaker = 0
  Height = 3000
  HorizontalArea = 37500
  IfcData = attributes={"GlobalId": {"name": "GlobalId", "type": "IfcGloballyUniqueId", "is_enum": false, "enum_values": []}, "Description": {"... (+484 chars omitted),+1 more (map truncated)
  IfcType = 172
  Length = 250
  MoveBase = false
  MoveWithHost = false
  Nodes = (2) [(-1.05471e-15,1.36424e-15,0),(-1.05471e-15,1.36424e-15,3000)]
  NodesOffset = 0
  Normal = (0,0,0)
  PerimeterLength = 800
  Placement = pos=(9010,9900,9000) rot=(0,0,1;0rad)
  PredefinedType = 0
  VerticalArea = 2400000
  Width = 150
FEATURE [Part::FeaturePython] Structure332  label="25x15 C080"  # Arch/BIM 172 (typed FeaturePython)
  FaceMaker = 0
  Height = 3000
  HorizontalArea = 37500
  IfcData = attributes={"GlobalId": {"name": "GlobalId", "type": "IfcGloballyUniqueId", "is_enum": false, "enum_values": []}, "Description": {"... (+484 chars omitted),+1 more (map truncated)
  IfcType = 172
  Length = 250
  MoveBase = false
  MoveWithHost = false
  Nodes = (2) [(-1.05471e-15,1.36424e-15,0),(-1.05471e-15,1.36424e-15,3000)]
  NodesOffset = 0
  Normal = (0,0,0)
  PerimeterLength = 800
  Placement = pos=(6160,9900,9000) rot=(0,0,1;0rad)
  PredefinedType = 0
  VerticalArea = 2400000
  Width = 150
FEATURE [Part::FeaturePython] Structure333  label="25x15 C081"  # Arch/BIM 172 (typed FeaturePython)
  FaceMaker = 0
  Height = 3000
  HorizontalArea = 37500
  IfcData = attributes={"GlobalId": {"name": "GlobalId", "type": "IfcGloballyUniqueId", "is_enum": false, "enum_values": []}, "Description": {"... (+484 chars omitted),+1 more (map truncated)
  IfcType = 172
  Length = 250
  MoveBase = false
  MoveWithHost = false
  Nodes = (2) [(-1.05471e-15,1.36424e-15,0),(-1.05471e-15,1.36424e-15,3000)]
  NodesOffset = 0
  Normal = (0,0,0)
  PerimeterLength = 800
  Placement = pos=(12010,9900,9000) rot=(0,0,1;0rad)
  PredefinedType = 0
  VerticalArea = 2400000
  Width = 150
FEATURE [Part::FeaturePython] Structure334  label="25x15 C082"  # Arch/BIM 172 (typed FeaturePython)
  FaceMaker = 0
  Height = 3000
  HorizontalArea = 37500
  IfcData = attributes={"GlobalId": {"name": "GlobalId", "type": "IfcGloballyUniqueId", "is_enum": false, "enum_values": []}, "Description": {"... (+484 chars omitted),+1 more (map truncated)
  IfcType = 172
  Length = 250
  MoveBase = false
  MoveWithHost = false
  Nodes = (2) [(-1.05471e-15,1.36424e-15,0),(-1.05471e-15,1.36424e-15,3000)]
  NodesOffset = 0
  Normal = (0,0,0)
  PerimeterLength = 800
  Placement = pos=(15210,9900,9000) rot=(0,0,1;0rad)
  PredefinedType = 0
  VerticalArea = 2400000
  Width = 150
FEATURE [Part::FeaturePython] Structure335  label="25x20 C012"  # Arch/BIM 24 (typed FeaturePython)
  FaceMaker = 0
  Height = 3000
  HorizontalArea = 50000
  IfcData = attributes={"GlobalId": {"name": "GlobalId", "type": "IfcGloballyUniqueId", "is_enum": false, "enum_values": []}, "Description": {"... (+438 chars omitted),+1 more (map truncated)
  IfcType = 24
  Length = 250
  MoveBase = false
  MoveWithHost = false
  Nodes = (2) [(-1.05471e-15,-1.81899e-15,0),(-1.05471e-15,-1.81899e-15,3000)]
  NodesOffset = 0
  Normal = (0,0,0)
  PerimeterLength = 900
  Placement = pos=(1930,6640,9000) rot=(0,0,1;0rad)
  PredefinedType = 0
  VerticalArea = 2700000
  Width = 200
FEATURE [Part::FeaturePython] Structure336  label="25x20 C013"  # Arch/BIM 172 (typed FeaturePython)
  FaceMaker = 0
  Height = 3000
  HorizontalArea = 50000
  IfcData = attributes={"GlobalId": {"name": "GlobalId", "type": "IfcGloballyUniqueId", "is_enum": false, "enum_values": []}, "Description": {"... (+484 chars omitted),+1 more (map truncated)
  IfcType = 172
  Length = 250
  MoveBase = false
  MoveWithHost = false
  Nodes = (2) [(-1.05471e-15,-1.81899e-15,0),(-1.05471e-15,-1.81899e-15,3000)]
  NodesOffset = 0
  Normal = (0,0,0)
  PerimeterLength = 900
  Placement = pos=(1930,3350,9000) rot=(0,0,1;0rad)
  PredefinedType = 0
  VerticalArea = 2700000
  Width = 200
FEATURE [App::GeometryPython] BuildingPart020  label="Columnas sobre P3"  # Arch/BIM 172 (typed FeaturePython)
  Area = 0
  Group = -> [Structure316,Structure317,Structure318,Structure319,Structure320,Structure321,Structure322,Structure323,Structure324,Structure325,Structure326,Structure327,Structure328,Structure329,Structure330,Structure331,Structure332,Structure333,Structure334,Structure335,Structure336]
  Height = 0
  HeightPropagate = true
  IfcData = attributes={"GlobalId": {"name": "GlobalId", "type": "IfcGloballyUniqueId", "is_enum": false, "enum_values": []}, "Description": {"... (+484 chars omitted),+1 more (map truncated)
  IfcType = 172
  LevelOffset = 0
  PredefinedType = 0
FEATURE [Part::FeaturePython] Structure337  label="L152"  # Arch/BIM 172 (typed FeaturePython)
  Base = -> Rectangle004
  FaceMaker = 0
  Height = 150
  HorizontalArea = 12611050
  IfcData = attributes={"GlobalId": {"name": "GlobalId", "type": "IfcGloballyUniqueId", "is_enum": false, "enum_values": []}, "Description": {"... (+484 chars omitted),+1 more (map truncated)
  IfcType = 172
  Length = 0
  MoveBase = false
  MoveWithHost = false
  Nodes = (2) [(4057.5,8270,3000),(4057.5,8270,2850)]
  NodesOffset = 0
  Normal = (0,0,-1)
  PerimeterLength = 14330
  Placement = pos=(0,0,9000) rot=(0,0,1;0rad)
  PredefinedType = 0
  VerticalArea = 2149500
  Width = 150
FEATURE [Part::FeaturePython] Structure338  label="L153"  # Arch/BIM 172 (typed FeaturePython)
  Base = -> Rectangle005
  FaceMaker = 0
  Height = 150
  HorizontalArea = 12732700
  IfcData = attributes={"GlobalId": {"name": "GlobalId", "type": "IfcGloballyUniqueId", "is_enum": false, "enum_values": []}, "Description": {"... (+484 chars omitted),+1 more (map truncated)
  IfcType = 172
  Length = 0
  MoveBase = false
  MoveWithHost = false
  Nodes = (2) [(4057.5,4995,3000),(4057.5,4995,2850)]
  NodesOffset = 0
  Normal = (0,0,-1)
  PerimeterLength = 14390
  Placement = pos=(0,0,9000) rot=(0,0,1;0rad)
  PredefinedType = 0
  VerticalArea = 2158500
  Width = 150
FEATURE [Part::FeaturePython] Structure339  label="L154"  # Arch/BIM 172 (typed FeaturePython)
  Base = -> Rectangle006
  FaceMaker = 0
  Height = 150
  HorizontalArea = 1.25705e+07
  IfcData = attributes={"GlobalId": {"name": "GlobalId", "type": "IfcGloballyUniqueId", "is_enum": false, "enum_values": []}, "Description": {"... (+484 chars omitted),+1 more (map truncated)
  IfcType = 172
  Length = 0
  MoveBase = false
  MoveWithHost = false
  Nodes = (2) [(4057.5,1725,3000),(4057.5,1725,2850)]
  NodesOffset = 0
  Normal = (0,0,-1)
  PerimeterLength = 14310
  Placement = pos=(0,0,9000) rot=(0,0,1;0rad)
  PredefinedType = 0
  VerticalArea = 2146500
  Width = 150
FEATURE [Part::FeaturePython] Structure340  label="L155"  # Arch/BIM 172 (typed FeaturePython)
  Base = -> Rectangle014
  FaceMaker = 0
  Height = 150
  HorizontalArea = 3928500
  IfcData = attributes={"GlobalId": {"name": "GlobalId", "type": "IfcGloballyUniqueId", "is_enum": false, "enum_values": []}, "Description": {"... (+484 chars omitted),+1 more (map truncated)
  IfcType = 172
  Length = 0
  MoveBase = false
  MoveWithHost = false
  Nodes = (2) [(7585,9097.5,3000),(7585,9097.5,2850)]
  NodesOffset = 0
  Normal = (0,0,-1)
  PerimeterLength = 8310
  Placement = pos=(0,0,9000) rot=(0,0,1;0rad)
  PredefinedType = 0
  VerticalArea = 1246500
  Width = 150
FEATURE [Part::FeaturePython] Structure341  label="L156"  # Arch/BIM 172 (typed FeaturePython)
  Base = -> Wire
  FaceMaker = 0
  Height = 150
  HorizontalArea = 3.9285e+06
  IfcData = attributes={"GlobalId": {"name": "GlobalId", "type": "IfcGloballyUniqueId", "is_enum": false, "enum_values": []}, "Description": {"... (+484 chars omitted),+1 more (map truncated)
  IfcType = 172
  Length = 0
  MoveBase = false
  MoveWithHost = false
  Nodes = (2) [(7543.76,7449.37,3000),(7543.76,7449.37,2850)]
  NodesOffset = 0
  Normal = (0,0,-1)
  PerimeterLength = 8410
  Placement = pos=(0,0,8850) rot=(0,0,1;0rad)
  PredefinedType = 0
  VerticalArea = 1261500
  Width = 150
FEATURE [Part::FeaturePython] Structure342  label="L157"  # Arch/BIM 172 (typed FeaturePython)
  Base = -> Wire001
  FaceMaker = 0
  Height = 150
  HorizontalArea = 3.90134e+06
  IfcData = attributes={"GlobalId": {"name": "GlobalId", "type": "IfcGloballyUniqueId", "is_enum": false, "enum_values": []}, "Description": {"... (+484 chars omitted),+1 more (map truncated)
  IfcType = 172
  Length = 0
  MoveBase = false
  MoveWithHost = false
  Nodes = (2) [(7543.46,5835.61,3000),(7543.46,5835.61,2850)]
  NodesOffset = 0
  Normal = (0,0,-1)
  PerimeterLength = 8389.89
  Placement = pos=(0,0,8850) rot=(0,0,1;0rad)
  PredefinedType = 0
  VerticalArea = 1.25848e+06
  Width = 150
FEATURE [Part::FeaturePython] Structure343  label="L158"  # Arch/BIM 172 (typed FeaturePython)
  Base = -> Rectangle015
  FaceMaker = 0
  Height = 150
  HorizontalArea = 4.0365e+06
  IfcData = attributes={"GlobalId": {"name": "GlobalId", "type": "IfcGloballyUniqueId", "is_enum": false, "enum_values": []}, "Description": {"... (+484 chars omitted),+1 more (map truncated)
  IfcType = 172
  Length = 0
  MoveBase = false
  MoveWithHost = false
  Nodes = (2) [(7585,4172.5,3000),(7585,4172.5,2850)]
  NodesOffset = 0
  Normal = (0,0,-1)
  PerimeterLength = 8390
  Placement = pos=(0,0,9000) rot=(0,0,1;0rad)
  PredefinedType = 0
  VerticalArea = 1258500
  Width = 150
FEATURE [Part::FeaturePython] Structure344  label="L159"  # Arch/BIM 172 (typed FeaturePython)
  Base = -> Wire002
  FaceMaker = 0
  Height = 150
  HorizontalArea = 3.91484e+06
  IfcData = attributes={"GlobalId": {"name": "GlobalId", "type": "IfcGloballyUniqueId", "is_enum": false, "enum_values": []}, "Description": {"... (+484 chars omitted),+1 more (map truncated)
  IfcType = 172
  Length = 0
  MoveBase = false
  MoveWithHost = false
  Nodes = (2) [(7543.6,2543.13,3000),(7543.6,2543.13,2850)]
  NodesOffset = 0
  Normal = (0,0,-1)
  PerimeterLength = 8399.89
  Placement = pos=(0,0,8850) rot=(0,0,1;0rad)
  PredefinedType = 0
  VerticalArea = 1.25998e+06
  Width = 150
FEATURE [Part::FeaturePython] Structure345  label="L160"  # Arch/BIM 172 (typed FeaturePython)
  Base = -> Rectangle016
  FaceMaker = 0
  Height = 150
  HorizontalArea = 3.915e+06
  IfcData = attributes={"GlobalId": {"name": "GlobalId", "type": "IfcGloballyUniqueId", "is_enum": false, "enum_values": []}, "Description": {"... (+484 chars omitted),+1 more (map truncated)
  IfcType = 172
  Length = 0
  MoveBase = false
  MoveWithHost = false
  Nodes = (2) [(7585,900,3000),(7585,900,2850)]
  NodesOffset = 0
  Normal = (0,0,-1)
  PerimeterLength = 8300
  Placement = pos=(0,0,9000) rot=(0,0,1;0rad)
  PredefinedType = 0
  VerticalArea = 1.245e+06
  Width = 150
FEATURE [Part::FeaturePython] Structure346  label="L161"  # Arch/BIM 172 (typed FeaturePython)
  Base = -> Rectangle008
  FaceMaker = 0
  Height = 150
  HorizontalArea = 4354000
  IfcData = attributes={"GlobalId": {"name": "GlobalId", "type": "IfcGloballyUniqueId", "is_enum": false, "enum_values": []}, "Description": {"... (+484 chars omitted),+1 more (map truncated)
  IfcType = 172
  Length = 0
  MoveBase = false
  MoveWithHost = false
  Nodes = (2) [(9785,8270,3000),(9785,8270,2850)]
  NodesOffset = 0
  Normal = (0,0,-1)
  PerimeterLength = 9020
  Placement = pos=(0,0,9000) rot=(0,0,1;0rad)
  PredefinedType = 0
  VerticalArea = 1353000
  Width = 150
FEATURE [Part::FeaturePython] Structure347  label="L162"  # Arch/BIM 172 (typed FeaturePython)
  Base = -> Rectangle011
  FaceMaker = 0
  Height = 150
  HorizontalArea = 4396000
  IfcData = attributes={"GlobalId": {"name": "GlobalId", "type": "IfcGloballyUniqueId", "is_enum": false, "enum_values": []}, "Description": {"... (+484 chars omitted),+1 more (map truncated)
  IfcType = 172
  Length = 0
  MoveBase = false
  MoveWithHost = false
  Nodes = (2) [(9785,4995,3000),(9785,4995,2850)]
  NodesOffset = 0
  Normal = (0,0,-1)
  PerimeterLength = 9080
  Placement = pos=(0,0,9000) rot=(0,0,1;0rad)
  PredefinedType = 0
  VerticalArea = 1362000
  Width = 150
FEATURE [Part::FeaturePython] Structure348  label="L163"  # Arch/BIM 172 (typed FeaturePython)
  Base = -> Rectangle013
  FaceMaker = 0
  Height = 150
  HorizontalArea = 4.34e+06
  IfcData = attributes={"GlobalId": {"name": "GlobalId", "type": "IfcGloballyUniqueId", "is_enum": false, "enum_values": []}, "Description": {"... (+484 chars omitted),+1 more (map truncated)
  IfcType = 172
  Length = 0
  MoveBase = false
  MoveWithHost = false
  Nodes = (2) [(9785,1725,3000),(9785,1725,2850)]
  NodesOffset = 0
  Normal = (0,0,-1)
  PerimeterLength = 9000
  Placement = pos=(0,0,9000) rot=(0,0,1;0rad)
  PredefinedType = 0
  VerticalArea = 1350000
  Width = 150
FEATURE [Part::FeaturePython] Structure349  label="L164"  # Arch/BIM 172 (typed FeaturePython)
  Base = -> Rectangle009
  FaceMaker = 0
  Height = 150
  HorizontalArea = 1.794e+06
  IfcData = attributes={"GlobalId": {"name": "GlobalId", "type": "IfcGloballyUniqueId", "is_enum": false, "enum_values": []}, "Description": {"... (+484 chars omitted),+1 more (map truncated)
  IfcType = 172
  Length = 0
  MoveBase = false
  MoveWithHost = false
  Nodes = (2) [(11285,9135,3000),(11285,9135,2850)]
  NodesOffset = 0
  Normal = (0,0,-1)
  PerimeterLength = 5360
  Placement = pos=(0,0,9000) rot=(0,0,1;0rad)
  PredefinedType = 0
  VerticalArea = 804000
  Width = 150
FEATURE [Part::FeaturePython] Structure350  label="L165"  # Arch/BIM 172 (typed FeaturePython)
  Base = -> Rectangle018
  FaceMaker = 0
  Height = 150
  HorizontalArea = 3.211e+06
  IfcData = attributes={"GlobalId": {"name": "GlobalId", "type": "IfcGloballyUniqueId", "is_enum": false, "enum_values": []}, "Description": {"... (+484 chars omitted),+1 more (map truncated)
  IfcType = 172
  Length = 0
  MoveBase = false
  MoveWithHost = false
  Nodes = (2) [(11285,4660,3000),(11285,4660,2850)]
  NodesOffset = 0
  Normal = (0,0,-1)
  PerimeterLength = 7540
  Placement = pos=(0,0,8850) rot=(0,0,1;0rad)
  PredefinedType = 0
  VerticalArea = 1.131e+06
  Width = 150
FEATURE [Part::FeaturePython] Structure351  label="L166"  # Arch/BIM 172 (typed FeaturePython)
  Base = -> Rectangle020
  FaceMaker = 0
  Height = 150
  HorizontalArea = 9439500
  IfcData = attributes={"GlobalId": {"name": "GlobalId", "type": "IfcGloballyUniqueId", "is_enum": false, "enum_values": []}, "Description": {"... (+484 chars omitted),+1 more (map truncated)
  IfcType = 172
  Length = 0
  MoveBase = false
  MoveWithHost = false
  Nodes = (2) [(12157.5,1725,3000),(12157.5,1725,2850)]
  NodesOffset = 0
  Normal = (0,0,-1)
  PerimeterLength = 12290
  Placement = pos=(0,0,9000) rot=(0,0,1;0rad)
  PredefinedType = 0
  VerticalArea = 1843500
  Width = 150
FEATURE [Part::FeaturePython] Structure352  label="L167"  # Arch/BIM 172 (typed FeaturePython)
  Base = -> Rectangle019
  FaceMaker = 0
  Height = 150
  HorizontalArea = 3.93965e+06
  IfcData = attributes={"GlobalId": {"name": "GlobalId", "type": "IfcGloballyUniqueId", "is_enum": false, "enum_values": []}, "Description": {"... (+484 chars omitted),+1 more (map truncated)
  IfcType = 172
  Length = 0
  MoveBase = false
  MoveWithHost = false
  Nodes = (2) [(12882.5,4660,3000),(12882.5,4660,2850)]
  NodesOffset = 0
  Normal = (0,0,-1)
  PerimeterLength = 8130
  Placement = pos=(0,0,9000) rot=(0,0,1;0rad)
  PredefinedType = 0
  VerticalArea = 1.2195e+06
  Width = 150
FEATURE [Part::FeaturePython] Structure353  label="L168"  # Arch/BIM 172 (typed FeaturePython)
  Base = -> Rectangle017
  FaceMaker = 0
  Height = 150
  HorizontalArea = 4174500
  IfcData = attributes={"GlobalId": {"name": "GlobalId", "type": "IfcGloballyUniqueId", "is_enum": false, "enum_values": []}, "Description": {"... (+484 chars omitted),+1 more (map truncated)
  IfcType = 172
  Length = 0
  MoveBase = false
  MoveWithHost = false
  Nodes = (2) [(13597.5,9135,3000),(13597.5,9135,2850)]
  NodesOffset = 0
  Normal = (0,0,-1)
  PerimeterLength = 8810
  Placement = pos=(0,0,9000) rot=(0,0,1;0rad)
  PredefinedType = 0
  VerticalArea = 1321500
  Width = 150
FEATURE [App::GeometryPython] BuildingPart021  label="Losas sobre P3"  # Arch/BIM 172 (typed FeaturePython)
  Area = 0
  Group = -> [Structure337,Structure338,Structure339,Structure340,Structure341,Structure342,Structure343,Structure344,Structure345,Structure346,Structure347,Structure348,Structure349,Structure350,Structure351,Structure352,Structure353]
  Height = 0
  HeightPropagate = true
  IfcData = attributes={"GlobalId": {"name": "GlobalId", "type": "IfcGloballyUniqueId", "is_enum": false, "enum_values": []}, "Description": {"... (+484 chars omitted),+1 more (map truncated)
  IfcType = 172
  LevelOffset = 0
  PredefinedType = 0
FEATURE [Part::FeaturePython] Wall004  label="Tabique Ascensor P3"  # Arch/BIM 166 (typed FeaturePython)
  Align = 1
  Area = 24900000
  Base = -> Rectangle003
  BlockHeight = 0
  BlockLength = 0
  CountBroken = 0
  CountEntire = 0
  Face = 0
  Height = 3000
  HorizontalArea = 1155000
  IfcData = attributes={"GlobalId": {"name": "GlobalId", "type": "IfcGloballyUniqueId", "is_enum": false, "enum_values": []}, "Description": {"... (+533 chars omitted),+1 more (map truncated)
  IfcType = 166
  Joint = 0
  Length = 8300
  MakeBlocks = false
  MoveBase = false
  MoveWithHost = false
  Normal = (0,0,0)
  OffsetFirst = 0
  OffsetSecond = 0
  PerimeterLength = 8300
  Placement = pos=(0,0,9000) rot=(0,0,1;0rad)
  PredefinedType = 0
  VerticalArea = 46200000
  Width = 150
FEATURE [Part::FeaturePython] Structure354  label="V15x40 V102a003"  # Arch/BIM 7 (typed FeaturePython)
  FaceMaker = 0
  Height = 400
  HorizontalArea = 405000
  IfcData = attributes={"GlobalId": {"name": "GlobalId", "type": "IfcGloballyUniqueId", "is_enum": false, "enum_values": []}, "Description": {"... (+475 chars omitted),+1 more (map truncated)
  IfcType = 7
  Length = 2700
  MoveBase = false
  MoveWithHost = false
  Nodes = (2) [(-1.72563e-31,-1.42109e-15,-7.77156e-16),(2700,-1.42109e-15,-7.77156e-16)]
  NodesOffset = 0
  Normal = (0,0,0)
  PerimeterLength = 5700
  Placement = pos=(8935,8295,11800) rot=(0,0,1;3.14159rad)
  PredefinedType = 0
  VerticalArea = 2.28e+06
  Width = 150
FEATURE [Part::FeaturePython] Structure355  label="V15x40 V107a003"  # Arch/BIM 7 (typed FeaturePython)
  FaceMaker = 0
  Height = 400
  HorizontalArea = 405000
  IfcData = attributes={"GlobalId": {"name": "GlobalId", "type": "IfcGloballyUniqueId", "is_enum": false, "enum_values": []}, "Description": {"... (+475 chars omitted),+1 more (map truncated)
  IfcType = 7
  Length = 2700
  MoveBase = false
  MoveWithHost = false
  Nodes = (2) [(-1.72563e-31,-1.42109e-15,-7.77156e-16),(2700,-1.42109e-15,-7.77156e-16)]
  NodesOffset = 0
  Normal = (0,0,0)
  PerimeterLength = 5700
  Placement = pos=(8935,4995,11800) rot=(0,0,1;3.14159rad)
  PredefinedType = 0
  VerticalArea = 2.28e+06
  Width = 150
FEATURE [Part::FeaturePython] Structure356  label="V15x40 V112a003"  # Arch/BIM 7 (typed FeaturePython)
  FaceMaker = 0
  Height = 400
  HorizontalArea = 405000
  IfcData = attributes={"GlobalId": {"name": "GlobalId", "type": "IfcGloballyUniqueId", "is_enum": false, "enum_values": []}, "Description": {"... (+475 chars omitted),+1 more (map truncated)
  IfcType = 7
  Length = 2700
  MoveBase = false
  MoveWithHost = false
  Nodes = (2) [(-1.72563e-31,-1.42109e-15,-7.77156e-16),(2700,-1.42109e-15,-7.77156e-16)]
  NodesOffset = 0
  Normal = (0,0,0)
  PerimeterLength = 5700
  Placement = pos=(8935,1700,11800) rot=(0,0,1;3.14159rad)
  PredefinedType = 0
  VerticalArea = 2.28e+06
  Width = 150
FEATURE [Part::FeaturePython] Structure357  label="V15x40 V130a003"  # Arch/BIM 7 (typed FeaturePython)
  FaceMaker = 0
  Height = 400
  HorizontalArea = 370500
  IfcData = attributes={"GlobalId": {"name": "GlobalId", "type": "IfcGloballyUniqueId", "is_enum": false, "enum_values": []}, "Description": {"... (+475 chars omitted),+1 more (map truncated)
  IfcType = 7
  Length = 2470
  MoveBase = false
  MoveWithHost = false
  Nodes = (2) [(-1.72563e-31,-1.42109e-15,-7.77156e-16),(2470,-1.42109e-15,-7.77156e-16)]
  NodesOffset = 0
  Normal = (0,0,0)
  PerimeterLength = 5240
  Placement = pos=(12010,3425,11800) rot=(0,0,1;1.5708rad)
  PredefinedType = 0
  VerticalArea = 2096000
  Width = 150
FEATURE [Part::FeaturePython] Structure358  label="V15x40 V189"  # Arch/BIM 7 (typed FeaturePython)
  FaceMaker = 0
  Height = 400
  HorizontalArea = 597000
  IfcData = attributes={"GlobalId": {"name": "GlobalId", "type": "IfcGloballyUniqueId", "is_enum": false, "enum_values": []}, "Description": {"... (+475 chars omitted),+1 more (map truncated)
  IfcType = 7
  Length = 3980
  MoveBase = false
  MoveWithHost = false
  Nodes = (2) [(-1.72563e-31,-1.42109e-15,-7.77156e-16),(3980,-1.42109e-15,-7.77156e-16)]
  NodesOffset = 0
  Normal = (0,0,0)
  PerimeterLength = 8260
  Placement = pos=(2055,9900,11800) rot=(0,0,1;0rad)
  PredefinedType = 0
  VerticalArea = 3.304e+06
  Width = 150
FEATURE [Part::FeaturePython] Structure359  label="V15x40 V190"  # Arch/BIM 7 (typed FeaturePython)
  FaceMaker = 0
  Height = 400
  HorizontalArea = 390000
  IfcData = attributes={"GlobalId": {"name": "GlobalId", "type": "IfcGloballyUniqueId", "is_enum": false, "enum_values": []}, "Description": {"... (+475 chars omitted),+1 more (map truncated)
  IfcType = 7
  Length = 2600
  MoveBase = false
  MoveWithHost = false
  Nodes = (2) [(-1.72563e-31,-1.42109e-15,-7.77156e-16),(2600,-1.42109e-15,-7.77156e-16)]
  NodesOffset = 0
  Normal = (0,0,0)
  PerimeterLength = 5500
  Placement = pos=(6285,9900,11800) rot=(0,0,1;0rad)
  PredefinedType = 0
  VerticalArea = 2200000
  Width = 150
FEATURE [Part::FeaturePython] Structure360  label="V15x40 V191"  # Arch/BIM 7 (typed FeaturePython)
  FaceMaker = 0
  Height = 400
  HorizontalArea = 412500
  IfcData = attributes={"GlobalId": {"name": "GlobalId", "type": "IfcGloballyUniqueId", "is_enum": false, "enum_values": []}, "Description": {"... (+475 chars omitted),+1 more (map truncated)
  IfcType = 7
  Length = 2750
  MoveBase = false
  MoveWithHost = false
  Nodes = (2) [(-1.72563e-31,-1.42109e-15,-7.77156e-16),(2750,-1.42109e-15,-7.77156e-16)]
  NodesOffset = 0
  Normal = (0,0,0)
  PerimeterLength = 5800
  Placement = pos=(9135,9900,11800) rot=(0,0,1;0rad)
  PredefinedType = 0
  VerticalArea = 2320000
  Width = 150
FEATURE [Part::FeaturePython] Structure361  label="V15x40 V192"  # Arch/BIM 7 (typed FeaturePython)
  FaceMaker = 0
  Height = 400
  HorizontalArea = 442500
  IfcData = attributes={"GlobalId": {"name": "GlobalId", "type": "IfcGloballyUniqueId", "is_enum": false, "enum_values": []}, "Description": {"... (+475 chars omitted),+1 more (map truncated)
  IfcType = 7
  Length = 2950
  MoveBase = false
  MoveWithHost = false
  Nodes = (2) [(-1.72563e-31,-1.42109e-15,-7.77156e-16),(2950,-1.42109e-15,-7.77156e-16)]
  NodesOffset = 0
  Normal = (0,0,0)
  PerimeterLength = 6200
  Placement = pos=(12135,9900,11800) rot=(0,0,1;0rad)
  PredefinedType = 0
  VerticalArea = 2.48e+06
  Width = 150
FEATURE [Part::FeaturePython] Structure362  label="V15x40 V193"  # Arch/BIM 7 (typed FeaturePython)
  FaceMaker = 0
  Height = 400
  HorizontalArea = 453750
  IfcData = attributes={"GlobalId": {"name": "GlobalId", "type": "IfcGloballyUniqueId", "is_enum": false, "enum_values": []}, "Description": {"... (+475 chars omitted),+1 more (map truncated)
  IfcType = 7
  Length = 3025
  MoveBase = false
  MoveWithHost = false
  Nodes = (2) [(-1.72563e-31,-1.42109e-15,-7.77156e-16),(3025,-1.42109e-15,-7.77156e-16)]
  NodesOffset = 0
  Normal = (0,0,0)
  PerimeterLength = 6350
  Placement = pos=(12085,8370,11800) rot=(0,0,1;0rad)
  PredefinedType = 0
  VerticalArea = 2.54e+06
  Width = 150
FEATURE [Part::FeaturePython] Structure363  label="V15x40 V194"  # Arch/BIM 7 (typed FeaturePython)
  FaceMaker = 0
  Height = 400
  HorizontalArea = 597000
  IfcData = attributes={"GlobalId": {"name": "GlobalId", "type": "IfcGloballyUniqueId", "is_enum": false, "enum_values": []}, "Description": {"... (+475 chars omitted),+1 more (map truncated)
  IfcType = 7
  Length = 3980
  MoveBase = false
  MoveWithHost = false
  Nodes = (2) [(-1.72563e-31,-1.42109e-15,-7.77156e-16),(3980,-1.42109e-15,-7.77156e-16)]
  NodesOffset = 0
  Normal = (0,0,0)
  PerimeterLength = 8260
  Placement = pos=(2055,6640,11800) rot=(0,0,1;0rad)
  PredefinedType = 0
  VerticalArea = 3.304e+06
  Width = 150
FEATURE [Part::FeaturePython] Structure364  label="V15x40 V195"  # Arch/BIM 7 (typed FeaturePython)
  FaceMaker = 0
  Height = 400
  HorizontalArea = 397500
  IfcData = attributes={"GlobalId": {"name": "GlobalId", "type": "IfcGloballyUniqueId", "is_enum": false, "enum_values": []}, "Description": {"... (+475 chars omitted),+1 more (map truncated)
  IfcType = 7
  Length = 2650
  MoveBase = false
  MoveWithHost = false
  Nodes = (2) [(-1.72563e-31,-1.42109e-15,-7.77156e-16),(2650,-1.42109e-15,-7.77156e-16)]
  NodesOffset = 0
  Normal = (0,0,0)
  PerimeterLength = 5600
  Placement = pos=(6285,6640,11800) rot=(0,0,1;0rad)
  PredefinedType = 0
  VerticalArea = 2240000
  Width = 150
FEATURE [Part::FeaturePython] Structure365  label="V15x40 V196"  # Arch/BIM 7 (typed FeaturePython)
  FaceMaker = 0
  Height = 400
  HorizontalArea = 210000
  IfcData = attributes={"GlobalId": {"name": "GlobalId", "type": "IfcGloballyUniqueId", "is_enum": false, "enum_values": []}, "Description": {"... (+475 chars omitted),+1 more (map truncated)
  IfcType = 7
  Length = 1400
  MoveBase = false
  MoveWithHost = false
  Nodes = (2) [(-1.72563e-31,-1.42109e-15,-7.77156e-16),(1400,-1.42109e-15,-7.77156e-16)]
  NodesOffset = 0
  Normal = (0,0,0)
  PerimeterLength = 3100
  Placement = pos=(9085,6640,11800) rot=(0,0,1;0rad)
  PredefinedType = 0
  VerticalArea = 1240000
  Width = 150
FEATURE [Part::FeaturePython] Structure366  label="V15x40 V197"  # Arch/BIM 7 (typed FeaturePython)
  FaceMaker = 0
  Height = 400
  HorizontalArea = 235500
  IfcData = attributes={"GlobalId": {"name": "GlobalId", "type": "IfcGloballyUniqueId", "is_enum": false, "enum_values": []}, "Description": {"... (+475 chars omitted),+1 more (map truncated)
  IfcType = 7
  Length = 1570
  MoveBase = false
  MoveWithHost = false
  Nodes = (2) [(-1.72563e-31,-1.42109e-15,-7.77156e-16),(1570,-1.42109e-15,-7.77156e-16)]
  NodesOffset = 0
  Normal = (0,0,0)
  PerimeterLength = 3440
  Placement = pos=(13655,5970,11800) rot=(0,0,1;3.14159rad)
  PredefinedType = 0
  VerticalArea = 1.376e+06
  Width = 150
FEATURE [Part::FeaturePython] Structure367  label="V15x40 V198"  # Arch/BIM 7 (typed FeaturePython)
  FaceMaker = 0
  Height = 400
  HorizontalArea = 177000
  IfcData = attributes={"GlobalId": {"name": "GlobalId", "type": "IfcGloballyUniqueId", "is_enum": false, "enum_values": []}, "Description": {"... (+475 chars omitted),+1 more (map truncated)
  IfcType = 7
  Length = 1180
  MoveBase = false
  MoveWithHost = false
  Nodes = (2) [(-1.72563e-31,-1.42109e-15,-7.77156e-16),(1180,-1.42109e-15,-7.77156e-16)]
  NodesOffset = 0
  Normal = (0,0,0)
  PerimeterLength = 2660
  Placement = pos=(13905,5970,11800) rot=(0,0,1;0rad)
  PredefinedType = 0
  VerticalArea = 1064000
  Width = 150
FEATURE [Part::FeaturePython] Structure368  label="V15x40 V199"  # Arch/BIM 7 (typed FeaturePython)
  FaceMaker = 0
  Height = 400
  HorizontalArea = 597000
  IfcData = attributes={"GlobalId": {"name": "GlobalId", "type": "IfcGloballyUniqueId", "is_enum": false, "enum_values": []}, "Description": {"... (+475 chars omitted),+1 more (map truncated)
  IfcType = 7
  Length = 3980
  MoveBase = false
  MoveWithHost = false
  Nodes = (2) [(-1.72563e-31,-1.42109e-15,-7.77156e-16),(3980,-1.42109e-15,-7.77156e-16)]
  NodesOffset = 0
  Normal = (0,0,0)
  PerimeterLength = 8260
  Placement = pos=(2055,3350,11800) rot=(0,0,1;0rad)
  PredefinedType = 0
  VerticalArea = 3.304e+06
  Width = 150
FEATURE [Part::FeaturePython] Structure369  label="V15x40 V200"  # Arch/BIM 7 (typed FeaturePython)
  FaceMaker = 0
  Height = 400
  HorizontalArea = 397500
  IfcData = attributes={"GlobalId": {"name": "GlobalId", "type": "IfcGloballyUniqueId", "is_enum": false, "enum_values": []}, "Description": {"... (+475 chars omitted),+1 more (map truncated)
  IfcType = 7
  Length = 2650
  MoveBase = false
  MoveWithHost = false
  Nodes = (2) [(-1.72563e-31,-1.42109e-15,-7.77156e-16),(2650,-1.42109e-15,-7.77156e-16)]
  NodesOffset = 0
  Normal = (0,0,0)
  PerimeterLength = 5600
  Placement = pos=(6285,3350,11800) rot=(0,0,1;0rad)
  PredefinedType = 0
  VerticalArea = 2240000
  Width = 150
FEATURE [Part::FeaturePython] Structure370  label="V15x40 V201"  # Arch/BIM 7 (typed FeaturePython)
  FaceMaker = 0
  Height = 400
  HorizontalArea = 210000
  IfcData = attributes={"GlobalId": {"name": "GlobalId", "type": "IfcGloballyUniqueId", "is_enum": false, "enum_values": []}, "Description": {"... (+475 chars omitted),+1 more (map truncated)
  IfcType = 7
  Length = 1400
  MoveBase = false
  MoveWithHost = false
  Nodes = (2) [(-1.72563e-31,-1.42109e-15,-7.77156e-16),(1400,-1.42109e-15,-7.77156e-16)]
  NodesOffset = 0
  Normal = (0,0,0)
  PerimeterLength = 3100
  Placement = pos=(9085,3350,11800) rot=(0,0,1;0rad)
  PredefinedType = 0
  VerticalArea = 1240000
  Width = 150
FEATURE [Part::FeaturePython] Structure371  label="V15x40 V202"  # Arch/BIM 7 (typed FeaturePython)
  FaceMaker = 0
  Height = 400
  HorizontalArea = 460500
  IfcData = attributes={"GlobalId": {"name": "GlobalId", "type": "IfcGloballyUniqueId", "is_enum": false, "enum_values": []}, "Description": {"... (+475 chars omitted),+1 more (map truncated)
  IfcType = 7
  Length = 3070
  MoveBase = false
  MoveWithHost = false
  Nodes = (2) [(-1.72563e-31,-1.42109e-15,-7.77156e-16),(3070,-1.42109e-15,-7.77156e-16)]
  NodesOffset = 0
  Normal = (0,0,0)
  PerimeterLength = 6440
  Placement = pos=(10635,3350,11800) rot=(0,0,1;0rad)
  PredefinedType = 0
  VerticalArea = 2.576e+06
  Width = 150
FEATURE [Part::FeaturePython] Structure372  label="V15x40 V203"  # Arch/BIM 7 (typed FeaturePython)
  FaceMaker = 0
  Height = 400
  HorizontalArea = 597000
  IfcData = attributes={"GlobalId": {"name": "GlobalId", "type": "IfcGloballyUniqueId", "is_enum": false, "enum_values": []}, "Description": {"... (+475 chars omitted),+1 more (map truncated)
  IfcType = 7
  Length = 3980
  MoveBase = false
  MoveWithHost = false
  Nodes = (2) [(-1.72563e-31,-1.42109e-15,-7.77156e-16),(3980,-1.42109e-15,-7.77156e-16)]
  NodesOffset = 0
  Normal = (0,0,0)
  PerimeterLength = 8260
  Placement = pos=(2055,100,11800) rot=(0,0,1;0rad)
  PredefinedType = 0
  VerticalArea = 3.304e+06
  Width = 150
FEATURE [Part::FeaturePython] Structure373  label="V15x40 V204"  # Arch/BIM 7 (typed FeaturePython)
  FaceMaker = 0
  Height = 400
  HorizontalArea = 390000
  IfcData = attributes={"GlobalId": {"name": "GlobalId", "type": "IfcGloballyUniqueId", "is_enum": false, "enum_values": []}, "Description": {"... (+475 chars omitted),+1 more (map truncated)
  IfcType = 7
  Length = 2600
  MoveBase = false
  MoveWithHost = false
  Nodes = (2) [(-1.72563e-31,-1.42109e-15,-7.77156e-16),(2600,-1.42109e-15,-7.77156e-16)]
  NodesOffset = 0
  Normal = (0,0,0)
  PerimeterLength = 5500
  Placement = pos=(6285,100,11800) rot=(0,0,1;0rad)
  PredefinedType = 0
  VerticalArea = 2200000
  Width = 150
FEATURE [Part::FeaturePython] Structure374  label="V15x40 V205"  # Arch/BIM 7 (typed FeaturePython)
  FaceMaker = 0
  Height = 400
  HorizontalArea = 195000
  IfcData = attributes={"GlobalId": {"name": "GlobalId", "type": "IfcGloballyUniqueId", "is_enum": false, "enum_values": []}, "Description": {"... (+475 chars omitted),+1 more (map truncated)
  IfcType = 7
  Length = 1300
  MoveBase = false
  MoveWithHost = false
  Nodes = (2) [(-1.72563e-31,-1.42109e-15,-7.77156e-16),(1300,-1.42109e-15,-7.77156e-16)]
  NodesOffset = 0
  Normal = (0,0,0)
  PerimeterLength = 2900
  Placement = pos=(9135,100,11800) rot=(0,0,1;0rad)
  PredefinedType = 0
  VerticalArea = 1160000
  Width = 150
FEATURE [Part::FeaturePython] Structure375  label="V15x40 V206"  # Arch/BIM 7 (typed FeaturePython)
  FaceMaker = 0
  Height = 400
  HorizontalArea = 445500
  IfcData = attributes={"GlobalId": {"name": "GlobalId", "type": "IfcGloballyUniqueId", "is_enum": false, "enum_values": []}, "Description": {"... (+475 chars omitted),+1 more (map truncated)
  IfcType = 7
  Length = 2970
  MoveBase = false
  MoveWithHost = false
  Nodes = (2) [(-1.72563e-31,-1.42109e-15,-7.77156e-16),(2970,-1.42109e-15,-7.77156e-16)]
  NodesOffset = 0
  Normal = (0,0,0)
  PerimeterLength = 6240
  Placement = pos=(10685,100,11800) rot=(0,0,1;0rad)
  PredefinedType = 0
  VerticalArea = 2.496e+06
  Width = 150
FEATURE [Part::FeaturePython] Structure376  label="V15x40 V207"  # Arch/BIM 7 (typed FeaturePython)
  FaceMaker = 0
  Height = 400
  HorizontalArea = 465000
  IfcData = attributes={"GlobalId": {"name": "GlobalId", "type": "IfcGloballyUniqueId", "is_enum": false, "enum_values": []}, "Description": {"... (+475 chars omitted),+1 more (map truncated)
  IfcType = 7
  Length = 3100
  MoveBase = false
  MoveWithHost = false
  Nodes = (2) [(-1.72563e-31,-1.42109e-15,-7.77156e-16),(3100,-1.42109e-15,-7.77156e-16)]
  NodesOffset = 0
  Normal = (0,0,0)
  PerimeterLength = 6500
  Placement = pos=(6160,3275,11800) rot=(0,0,-1;1.5708rad)
  PredefinedType = 0
  VerticalArea = 2.6e+06
  Width = 150
FEATURE [Part::FeaturePython] Structure377  label="V15x40 V208"  # Arch/BIM 7 (typed FeaturePython)
  FaceMaker = 0
  Height = 400
  HorizontalArea = 471000
  IfcData = attributes={"GlobalId": {"name": "GlobalId", "type": "IfcGloballyUniqueId", "is_enum": false, "enum_values": []}, "Description": {"... (+475 chars omitted),+1 more (map truncated)
  IfcType = 7
  Length = 3140
  MoveBase = false
  MoveWithHost = false
  Nodes = (2) [(-1.72563e-31,-1.42109e-15,-7.77156e-16),(3140,-1.42109e-15,-7.77156e-16)]
  NodesOffset = 0
  Normal = (0,0,0)
  PerimeterLength = 6580
  Placement = pos=(6160,6565,11800) rot=(0,0,-1;1.5708rad)
  PredefinedType = 0
  VerticalArea = 2.632e+06
  Width = 150
FEATURE [Part::FeaturePython] Structure378  label="V15x40 V209"  # Arch/BIM 7 (typed FeaturePython)
  FaceMaker = 0
  Height = 400
  HorizontalArea = 466500
  IfcData = attributes={"GlobalId": {"name": "GlobalId", "type": "IfcGloballyUniqueId", "is_enum": false, "enum_values": []}, "Description": {"... (+475 chars omitted),+1 more (map truncated)
  IfcType = 7
  Length = 3110
  MoveBase = false
  MoveWithHost = false
  Nodes = (2) [(-1.72563e-31,-1.42109e-15,-7.77156e-16),(3110,-1.42109e-15,-7.77156e-16)]
  NodesOffset = 0
  Normal = (0,0,0)
  PerimeterLength = 6520
  Placement = pos=(6160,9825,11800) rot=(0,0,-1;1.5708rad)
  PredefinedType = 0
  VerticalArea = 2.608e+06
  Width = 150
FEATURE [Part::FeaturePython] Structure379  label="V15x40 V210"  # Arch/BIM 7 (typed FeaturePython)
  FaceMaker = 0
  Height = 400
  HorizontalArea = 457500
  IfcData = attributes={"GlobalId": {"name": "GlobalId", "type": "IfcGloballyUniqueId", "is_enum": false, "enum_values": []}, "Description": {"... (+475 chars omitted),+1 more (map truncated)
  IfcType = 7
  Length = 3050
  MoveBase = false
  MoveWithHost = false
  Nodes = (2) [(-1.72563e-31,-1.42109e-15,-7.77156e-16),(3050,-1.42109e-15,-7.77156e-16)]
  NodesOffset = 0
  Normal = (0,0,0)
  PerimeterLength = 6400
  Placement = pos=(9010,3225,11800) rot=(0,0,-1;1.5708rad)
  PredefinedType = 0
  VerticalArea = 2.56e+06
  Width = 150
FEATURE [Part::FeaturePython] Structure380  label="V15x40 V211"  # Arch/BIM 7 (typed FeaturePython)
  FaceMaker = 0
  Height = 400
  HorizontalArea = 456000
  IfcData = attributes={"GlobalId": {"name": "GlobalId", "type": "IfcGloballyUniqueId", "is_enum": false, "enum_values": []}, "Description": {"... (+475 chars omitted),+1 more (map truncated)
  IfcType = 7
  Length = 3040
  MoveBase = false
  MoveWithHost = false
  Nodes = (2) [(-1.72563e-31,-1.42109e-15,-7.77156e-16),(3040,-1.42109e-15,-7.77156e-16)]
  NodesOffset = 0
  Normal = (0,0,0)
  PerimeterLength = 6380
  Placement = pos=(9010,6515,11800) rot=(0,0,-1;1.5708rad)
  PredefinedType = 0
  VerticalArea = 2.552e+06
  Width = 150
FEATURE [Part::FeaturePython] Structure381  label="V15x40 V212"  # Arch/BIM 7 (typed FeaturePython)
  FaceMaker = 0
  Height = 400
  HorizontalArea = 459000
  IfcData = attributes={"GlobalId": {"name": "GlobalId", "type": "IfcGloballyUniqueId", "is_enum": false, "enum_values": []}, "Description": {"... (+475 chars omitted),+1 more (map truncated)
  IfcType = 7
  Length = 3060
  MoveBase = false
  MoveWithHost = false
  Nodes = (2) [(-1.72563e-31,-1.42109e-15,-7.77156e-16),(3060,-1.42109e-15,-7.77156e-16)]
  NodesOffset = 0
  Normal = (0,0,0)
  PerimeterLength = 6420
  Placement = pos=(9010,9825,11800) rot=(0,0,-1;1.5708rad)
  PredefinedType = 0
  VerticalArea = 2.568e+06
  Width = 150
FEATURE [Part::FeaturePython] Structure382  label="V15x40 V213"  # Arch/BIM 7 (typed FeaturePython)
  FaceMaker = 0
  Height = 400
  HorizontalArea = 457500
  IfcData = attributes={"GlobalId": {"name": "GlobalId", "type": "IfcGloballyUniqueId", "is_enum": false, "enum_values": []}, "Description": {"... (+475 chars omitted),+1 more (map truncated)
  IfcType = 7
  Length = 3050
  MoveBase = false
  MoveWithHost = false
  Nodes = (2) [(-1.72563e-31,-1.42109e-15,-7.77156e-16),(3050,-1.42109e-15,-7.77156e-16)]
  NodesOffset = 0
  Normal = (0,0,0)
  PerimeterLength = 6400
  Placement = pos=(10560,3225,11800) rot=(0,0,-1;1.5708rad)
  PredefinedType = 0
  VerticalArea = 2.56e+06
  Width = 150
FEATURE [Part::FeaturePython] Structure383  label="V15x40 V214"  # Arch/BIM 7 (typed FeaturePython)
  FaceMaker = 0
  Height = 400
  HorizontalArea = 363000
  IfcData = attributes={"GlobalId": {"name": "GlobalId", "type": "IfcGloballyUniqueId", "is_enum": false, "enum_values": []}, "Description": {"... (+475 chars omitted),+1 more (map truncated)
  IfcType = 7
  Length = 2420
  MoveBase = false
  MoveWithHost = false
  Nodes = (2) [(-1.72563e-31,-1.42109e-15,-7.77156e-16),(2420,-1.42109e-15,-7.77156e-16)]
  NodesOffset = 0
  Normal = (0,0,0)
  PerimeterLength = 5140
  Placement = pos=(10560,3475,11800) rot=(0,0,1;1.5708rad)
  PredefinedType = 0
  VerticalArea = 2056000
  Width = 150
FEATURE [Part::FeaturePython] Structure384  label="V15x40 V215"  # Arch/BIM 7 (typed FeaturePython)
  FaceMaker = 0
  Height = 400
  HorizontalArea = 207000
  IfcData = attributes={"GlobalId": {"name": "GlobalId", "type": "IfcGloballyUniqueId", "is_enum": false, "enum_values": []}, "Description": {"... (+475 chars omitted),+1 more (map truncated)
  IfcType = 7
  Length = 1380
  MoveBase = false
  MoveWithHost = false
  Nodes = (2) [(-1.72563e-31,-1.42109e-15,-7.77156e-16),(1380,-1.42109e-15,-7.77156e-16)]
  NodesOffset = 0
  Normal = (0,0,0)
  PerimeterLength = 3060
  Placement = pos=(10560,8445,11800) rot=(0,0,1;1.5708rad)
  PredefinedType = 0
  VerticalArea = 1224000
  Width = 150
FEATURE [Part::FeaturePython] Structure385  label="V15x40 V216"  # Arch/BIM 7 (typed FeaturePython)
  FaceMaker = 0
  Height = 400
  HorizontalArea = 207000
  IfcData = attributes={"GlobalId": {"name": "GlobalId", "type": "IfcGloballyUniqueId", "is_enum": false, "enum_values": []}, "Description": {"... (+475 chars omitted),+1 more (map truncated)
  IfcType = 7
  Length = 1380
  MoveBase = false
  MoveWithHost = false
  Nodes = (2) [(-1.72563e-31,-1.42109e-15,-7.77156e-16),(1380,-1.42109e-15,-7.77156e-16)]
  NodesOffset = 0
  Normal = (0,0,0)
  PerimeterLength = 3060
  Placement = pos=(12010,9825,11800) rot=(0,0,-1;1.5708rad)
  PredefinedType = 0
  VerticalArea = 1224000
  Width = 150
FEATURE [Part::FeaturePython] Structure386  label="V20x40 V148"  # Arch/BIM 7 (typed FeaturePython)
  FaceMaker = 0
  Height = 400
  HorizontalArea = 615000
  IfcData = attributes={"GlobalId": {"name": "GlobalId", "type": "IfcGloballyUniqueId", "is_enum": false, "enum_values": []}, "Description": {"... (+475 chars omitted),+1 more (map truncated)
  IfcType = 7
  Length = 3075
  MoveBase = false
  MoveWithHost = false
  Nodes = (2) [(-1.72563e-31,0,-7.77156e-16),(3075,0,-7.77156e-16)]
  NodesOffset = 0
  Normal = (0,0,0)
  PerimeterLength = 6550
  Placement = pos=(1930,3250,11800) rot=(0,0,-1;1.5708rad)
  PredefinedType = 0
  VerticalArea = 2.62e+06
  Width = 200
FEATURE [Part::FeaturePython] Structure387  label="V20x40 V149"  # Arch/BIM 7 (typed FeaturePython)
  FaceMaker = 0
  Height = 400
  HorizontalArea = 618000
  IfcData = attributes={"GlobalId": {"name": "GlobalId", "type": "IfcGloballyUniqueId", "is_enum": false, "enum_values": []}, "Description": {"... (+475 chars omitted),+1 more (map truncated)
  IfcType = 7
  Length = 3090
  MoveBase = false
  MoveWithHost = false
  Nodes = (2) [(-1.72563e-31,0,-7.77156e-16),(3090,0,-7.77156e-16)]
  NodesOffset = 0
  Normal = (0,0,0)
  PerimeterLength = 6580
  Placement = pos=(1930,6540,11800) rot=(0,0,-1;1.5708rad)
  PredefinedType = 0
  VerticalArea = 2.632e+06
  Width = 200
FEATURE [Part::FeaturePython] Structure388  label="V20x40 V150"  # Arch/BIM 7 (typed FeaturePython)
  FaceMaker = 0
  Height = 400
  HorizontalArea = 617000
  IfcData = attributes={"GlobalId": {"name": "GlobalId", "type": "IfcGloballyUniqueId", "is_enum": false, "enum_values": []}, "Description": {"... (+475 chars omitted),+1 more (map truncated)
  IfcType = 7
  Length = 3085
  MoveBase = false
  MoveWithHost = false
  Nodes = (2) [(-1.72563e-31,0,-7.77156e-16),(3085,0,-7.77156e-16)]
  NodesOffset = 0
  Normal = (0,0,0)
  PerimeterLength = 6570
  Placement = pos=(1930,9825,11800) rot=(0,0,-1;1.5708rad)
  PredefinedType = 0
  VerticalArea = 2.628e+06
  Width = 200
FEATURE [Part::FeaturePython] Structure389  label="V20x40 V151"  # Arch/BIM 7 (typed FeaturePython)
  FaceMaker = 0
  Height = 400
  HorizontalArea = 635000
  IfcData = attributes={"GlobalId": {"name": "GlobalId", "type": "IfcGloballyUniqueId", "is_enum": false, "enum_values": []}, "Description": {"... (+475 chars omitted),+1 more (map truncated)
  IfcType = 7
  Length = 3175
  MoveBase = false
  MoveWithHost = false
  Nodes = (2) [(-1.72563e-31,0,-7.77156e-16),(3175,0,-7.77156e-16)]
  NodesOffset = 0
  Normal = (0,0,0)
  PerimeterLength = 6750
  Placement = pos=(13780,175,11800) rot=(0,0,1;1.5708rad)
  PredefinedType = 0
  VerticalArea = 2.7e+06
  Width = 200
FEATURE [Part::FeaturePython] Structure390  label="V20x40 V152"  # Arch/BIM 7 (typed FeaturePython)
  FaceMaker = 0
  Height = 400
  HorizontalArea = 509000
  IfcData = attributes={"GlobalId": {"name": "GlobalId", "type": "IfcGloballyUniqueId", "is_enum": false, "enum_values": []}, "Description": {"... (+475 chars omitted),+1 more (map truncated)
  IfcType = 7
  Length = 2545
  MoveBase = false
  MoveWithHost = false
  Nodes = (2) [(-1.72563e-31,0,-7.77156e-16),(2545,0,-7.77156e-16)]
  NodesOffset = 0
  Normal = (0,0,0)
  PerimeterLength = 5490
  Placement = pos=(13780,3350,11800) rot=(0,0,1;1.5708rad)
  PredefinedType = 0
  VerticalArea = 2196000
  Width = 200
FEATURE [Part::FeaturePython] Structure391  label="V20x40 V153"  # Arch/BIM 7 (typed FeaturePython)
  FaceMaker = 0
  Height = 400
  HorizontalArea = 756000
  IfcData = attributes={"GlobalId": {"name": "GlobalId", "type": "IfcGloballyUniqueId", "is_enum": false, "enum_values": []}, "Description": {"... (+475 chars omitted),+1 more (map truncated)
  IfcType = 7
  Length = 3780
  MoveBase = false
  MoveWithHost = false
  Nodes = (2) [(-1.72563e-31,0,-7.77156e-16),(3780,0,-7.77156e-16)]
  NodesOffset = 0
  Normal = (0,0,0)
  PerimeterLength = 7960
  Placement = pos=(15210,6045,11800) rot=(0,0,1;1.5708rad)
  PredefinedType = 0
  VerticalArea = 3.184e+06
  Width = 200
FEATURE [App::GeometryPython] BuildingPart022  label="Vigas sobre P3"  # Arch/BIM 172 (typed FeaturePython)
  Area = 0
  Group = -> [Structure354,Structure355,Structure356,Structure357,Structure358,Structure359,Structure360,Structure361,Structure362,Structure363,Structure364,Structure365,Structure366,Structure367,Structure368,Structure369,Structure370,Structure371,Structure372,Structure373,Structure374,Structure375,Structure376,Structure377,Structure378,Structure379,Structure380,Structure381,Structure382,Structure383,+8 more]
  Height = 0
  HeightPropagate = true
  IfcData = attributes={"GlobalId": {"name": "GlobalId", "type": "IfcGloballyUniqueId", "is_enum": false, "enum_values": []}, "Description": {"... (+484 chars omitted),+1 more (map truncated)
  IfcType = 172
  LevelOffset = 0
  PredefinedType = 0
FEATURE [App::GeometryPython] BuildingPart019  label="Piso 3"  # Arch/BIM 172 (typed FeaturePython)
  Area = 24900000
  Group = -> [BuildingPart020,BuildingPart021,Wall004,BuildingPart022]
  Height = 0
  HeightPropagate = true
  IfcData = attributes={"GlobalId": {"name": "GlobalId", "type": "IfcGloballyUniqueId", "is_enum": false, "enum_values": []}, "Description": {"... (+484 chars omitted),+1 more (map truncated)
  IfcType = 172
  LevelOffset = 0
  Placement = pos=(0,0,9000) rot=(0,0,1;0rad)
  PredefinedType = 0
FEATURE [App::GeometryPython] BuildingPart024  label="Sobre Terraza"  # Arch/BIM 172 (typed FeaturePython)
  Area = 0
  Height = 0
  HeightPropagate = true
  IfcData = attributes={"GlobalId": {"name": "GlobalId", "type": "IfcGloballyUniqueId", "is_enum": false, "enum_values": []}, "Description": {"... (+484 chars omitted),+1 more (map truncated)
  IfcType = 172
  LevelOffset = 0
  PredefinedType = 0
FEATURE [Part::FeaturePython] Structure392  label="Column"  # Arch/BIM 24 (typed FeaturePython)
  FaceMaker = 0
  Height = 3000
  HorizontalArea = 22500
  IfcData = attributes={"GlobalId": {"name": "GlobalId", "type": "IfcGloballyUniqueId", "is_enum": false, "enum_values": []}, "Description": {"... (+438 chars omitted),+1 more (map truncated)
  IfcType = 24
  Length = 150
  MoveBase = false
  MoveWithHost = false
  Nodes = (2) [(2.77556e-16,7.57912e-16,0),(2.77556e-16,7.57912e-16,3000)]
  NodesOffset = 0
  Normal = (0,0,0)
  PerimeterLength = 600
  Placement = pos=(15210,9900,12000) rot=(0,0,1;0rad)
  PredefinedType = 0
  VerticalArea = 1800000
  Width = 150
FEATURE [Part::FeaturePython] Structure393  label="Column001"  # Arch/BIM 24 (typed FeaturePython)
  FaceMaker = 0
  Height = 3000
  HorizontalArea = 22500
  IfcData = attributes={"GlobalId": {"name": "GlobalId", "type": "IfcGloballyUniqueId", "is_enum": false, "enum_values": []}, "Description": {"... (+438 chars omitted),+1 more (map truncated)
  IfcType = 24
  Length = 150
  MoveBase = false
  MoveWithHost = false
  Nodes = (2) [(2.77556e-16,7.57912e-16,0),(2.77556e-16,7.57912e-16,3000)]
  NodesOffset = 0
  Normal = (0,0,0)
  PerimeterLength = 600
  Placement = pos=(10560,9900,12000) rot=(0,0,1;0rad)
  PredefinedType = 0
  VerticalArea = 1800000
  Width = 150
FEATURE [Part::FeaturePython] Structure394  label="Column002"  # Arch/BIM 24 (typed FeaturePython)
  FaceMaker = 0
  Height = 3000
  HorizontalArea = 22500
  IfcData = attributes={"GlobalId": {"name": "GlobalId", "type": "IfcGloballyUniqueId", "is_enum": false, "enum_values": []}, "Description": {"... (+438 chars omitted),+1 more (map truncated)
  IfcType = 24
  Length = 150
  MoveBase = false
  MoveWithHost = false
  Nodes = (2) [(2.77556e-16,7.57912e-16,0),(2.77556e-16,7.57912e-16,3000)]
  NodesOffset = 0
  Normal = (0,0,0)
  PerimeterLength = 600
  Placement = pos=(15210,5970,12000) rot=(0,0,1;0rad)
  PredefinedType = 0
  VerticalArea = 1800000
  Width = 150
FEATURE [Part::FeaturePython] Structure395  label="Column003"  # Arch/BIM 24 (typed FeaturePython)
  FaceMaker = 0
  Height = 3000
  HorizontalArea = 22500
  IfcData = attributes={"GlobalId": {"name": "GlobalId", "type": "IfcGloballyUniqueId", "is_enum": false, "enum_values": []}, "Description": {"... (+438 chars omitted),+1 more (map truncated)
  IfcType = 24
  Length = 150
  MoveBase = false
  MoveWithHost = false
  Nodes = (2) [(2.77556e-16,7.57912e-16,0),(2.77556e-16,7.57912e-16,3000)]
  NodesOffset = 0
  Normal = (0,0,0)
  PerimeterLength = 600
  Placement = pos=(10560,5970,12000) rot=(0,0,1;0rad)
  PredefinedType = 0
  VerticalArea = 1800000
  Width = 150
FEATURE [Part::FeaturePython] Structure396  label="Beam042"  # Arch/BIM 7 (typed FeaturePython)
  FaceMaker = 0
  Height = 300
  HorizontalArea = 675000
  IfcData = attributes={"GlobalId": {"name": "GlobalId", "type": "IfcGloballyUniqueId", "is_enum": false, "enum_values": []}, "Description": {"... (+475 chars omitted),+1 more (map truncated)
  IfcType = 7
  Length = 4500
  MoveBase = false
  MoveWithHost = false
  Nodes = (2) [(1.2326e-31,-7.57912e-16,5.55112e-16),(4500,-7.57912e-16,5.55112e-16)]
  NodesOffset = 0
  Normal = (0,0,0)
  PerimeterLength = 9300
  Placement = pos=(10635,9900,14850) rot=(0,0,1;0rad)
  PredefinedType = 0
  VerticalArea = 2790000
  Width = 150
FEATURE [Part::FeaturePython] Structure397  label="Beam043"  # Arch/BIM 7 (typed FeaturePython)
  FaceMaker = 0
  Height = 300
  HorizontalArea = 567000
  IfcData = attributes={"GlobalId": {"name": "GlobalId", "type": "IfcGloballyUniqueId", "is_enum": false, "enum_values": []}, "Description": {"... (+475 chars omitted),+1 more (map truncated)
  IfcType = 7
  Length = 3780
  MoveBase = false
  MoveWithHost = false
  Nodes = (2) [(1.2326e-31,-7.57912e-16,5.55112e-16),(3780,-7.57912e-16,5.55112e-16)]
  NodesOffset = 0
  Normal = (0,0,0)
  PerimeterLength = 7860
  Placement = pos=(15210,9825,14850) rot=(0,0,-1;1.5708rad)
  PredefinedType = 0
  VerticalArea = 2.358e+06
  Width = 150
FEATURE [Part::FeaturePython] Structure398  label="Beam044"  # Arch/BIM 7 (typed FeaturePython)
  FaceMaker = 0
  Height = 300
  HorizontalArea = 675000
  IfcData = attributes={"GlobalId": {"name": "GlobalId", "type": "IfcGloballyUniqueId", "is_enum": false, "enum_values": []}, "Description": {"... (+475 chars omitted),+1 more (map truncated)
  IfcType = 7
  Length = 4500
  MoveBase = false
  MoveWithHost = false
  Nodes = (2) [(1.2326e-31,-7.57912e-16,5.55112e-16),(4500,-7.57912e-16,5.55112e-16)]
  NodesOffset = 0
  Normal = (0,0,0)
  PerimeterLength = 9300
  Placement = pos=(15135,5970,14850) rot=(0,0,1;3.14159rad)
  PredefinedType = 0
  VerticalArea = 2790000
  Width = 150
FEATURE [Part::FeaturePython] Structure399  label="Beam045"  # Arch/BIM 7 (typed FeaturePython)
  FaceMaker = 0
  Height = 300
  HorizontalArea = 567000
  IfcData = attributes={"GlobalId": {"name": "GlobalId", "type": "IfcGloballyUniqueId", "is_enum": false, "enum_values": []}, "Description": {"... (+475 chars omitted),+1 more (map truncated)
  IfcType = 7
  Length = 3780
  MoveBase = false
  MoveWithHost = false
  Nodes = (2) [(1.2326e-31,-7.57912e-16,5.55112e-16),(3780,-7.57912e-16,5.55112e-16)]
  NodesOffset = 0
  Normal = (0,0,0)
  PerimeterLength = 7860
  Placement = pos=(10560,6045,14850) rot=(0,0,1;1.5708rad)
  PredefinedType = 0
  VerticalArea = 2.358e+06
  Width = 150
FEATURE [App::GeometryPython] BuildingPart025  label="Vigas sobre Terraza"  # Arch/BIM 172 (typed FeaturePython)
  Area = 0
  Group = -> [Structure396,Structure397,Structure398,Structure399]
  Height = 0
  HeightPropagate = true
  IfcData = attributes={"GlobalId": {"name": "GlobalId", "type": "IfcGloballyUniqueId", "is_enum": false, "enum_values": []}, "Description": {"... (+484 chars omitted),+1 more (map truncated)
  IfcType = 172
  LevelOffset = 0
  Placement = pos=(0,0,12000) rot=(0,0,1;0rad)
  PredefinedType = 0
FEATURE [App::GeometryPython] BuildingPart026  label="Columnas Terraza"  # Arch/BIM 172 (typed FeaturePython)
  Area = 0
  Group = -> [Structure392,Structure393,Structure394,Structure395]
  Height = 0
  HeightPropagate = true
  IfcData = attributes={"GlobalId": {"name": "GlobalId", "type": "IfcGloballyUniqueId", "is_enum": false, "enum_values": []}, "Description": {"... (+484 chars omitted),+1 more (map truncated)
  IfcType = 172
  LevelOffset = 0
  Placement = pos=(0,0,12000) rot=(0,0,1;0rad)
  PredefinedType = 0
FEATURE [Part::Part2DObjectPython] Rectangle021  # Draft 2D object (typed FeaturePython)
  Area = 1.701e+07
  ChamferSize = 0
  Columns = 1
  FilletRadius = 0
  Height = 3780
  Length = 4500
  MakeFace = true
  Placement = pos=(10635,6045,15000) rot=(0,0,1;0rad)
  Rows = 1
FEATURE [Part::FeaturePython] Structure400  label="Structure"  # Arch/BIM 172 (typed FeaturePython)
  Base = -> Rectangle021
  FaceMaker = 0
  Height = 150
  HorizontalArea = 1.701e+07
  IfcData = attributes={"GlobalId": {"name": "GlobalId", "type": "IfcGloballyUniqueId", "is_enum": false, "enum_values": []}, "Description": {"... (+484 chars omitted),+1 more (map truncated)
  IfcType = 172
  Length = 0
  MoveBase = false
  MoveWithHost = false
  Nodes = (2) [(12885,7935,15000),(12885,7935,14850)]
  NodesOffset = 0
  Normal = (0,0,-1)
  PerimeterLength = 16560
  PredefinedType = 0
  VerticalArea = 2484000
  Width = 150
FEATURE [App::GeometryPython] BuildingPart027  label="Losas sobre Terraza"  # Arch/BIM 172 (typed FeaturePython)
  Area = 0
  Group = -> [Structure400]
  Height = 0
  HeightPropagate = true
  IfcData = attributes={"GlobalId": {"name": "GlobalId", "type": "IfcGloballyUniqueId", "is_enum": false, "enum_values": []}, "Description": {"... (+484 chars omitted),+1 more (map truncated)
  IfcType = 172
  LevelOffset = 0
  Placement = pos=(0,0,12000) rot=(0,0,1;0rad)
  PredefinedType = 0
FEATURE [App::GeometryPython] BuildingPart023  label="Terraza"  # Arch/BIM 172 (typed FeaturePython)
  Area = 0
  Group = -> [BuildingPart026,BuildingPart025,BuildingPart027]
  Height = 0
  HeightPropagate = true
  IfcData = attributes={"GlobalId": {"name": "GlobalId", "type": "IfcGloballyUniqueId", "is_enum": false, "enum_values": []}, "Description": {"... (+484 chars omitted),+1 more (map truncated)
  IfcType = 172
  LevelOffset = 0
  Placement = pos=(0,0,12000) rot=(0,0,1;0rad)
  PredefinedType = 0
FEATURE [App::GeometryPython] BuildingPart  label="Building"  # Arch/BIM 10 (typed FeaturePython)
  Area = 107900000
  BuildingType = 0
  CompositionType = 0
  ElevationOfRefHeight = 0
  ElevationOfTerrain = 0
  Group = -> [BuildingPart002,Rectangle001,BuildingPart001,BuildingPart003,BuildingPart010,BuildingPart019,Group,BuildingPart023,BuildingPart024]
  Height = 0
  HeightPropagate = true
  IfcData = attributes={"GlobalId": {"name": "GlobalId", "type": "IfcGloballyUniqueId", "is_enum": false, "enum_values": []}, "Description": {"... (+1010 chars omitted),+1 more (map truncated)
  IfcType = 10
  LevelOffset = 0
  LongName = Building
FEATURE [App::FeaturePython] Section  label="Planta Nivel 0"  # WARN: FeaturePython — macro-defined, semantics opaque (R4)
  Clip = false
  Objects = -> [BuildingPart]
  OnlySolids = false
  Placement = pos=(15000,5000,1000) rot=(0,0,1;0rad)
  UseMaterialColorForFill = false
FEATURE [TechDraw::DrawViewArch] ArchView
  AllOn = false
  CutLineWidth = 0.5
  FillSpaces = false
  FontSize = 12
  JoinArch = false
  LineWidth = 1
  LockPosition = false
  RenderMode = 0
  Rotation = 0
  Scale = 0.03
  ScaleType = 2
  ShowFill = true
  ShowHidden = false
  Source = -> Section
  Symbol = <blob: 30494 chars omitted>
  X = 595.872
  Y = 421.643
FEATURE [TechDraw::DrawPage] Page004  label="_Planta Nivel 0"
  KeepUpdated = true
  NextBalloonIndex = 1
  ProjectionType = 0
  Template = -> Template004
  Views = -> [ArchView]
FEATURE [App::FeaturePython] Section001  label="Planta Fundaciones"  # WARN: FeaturePython — macro-defined, semantics opaque (R4)
  Clip = true
  Objects = -> [BuildingPart]
  OnlySolids = false
  Placement = pos=(15000,5000,-300) rot=(0,0,1;0rad)
  UseMaterialColorForFill = false
FEATURE [TechDraw::DrawViewArch] ArchView001  label="__Planta Fundaciones"
  AllOn = false
  CutLineWidth = 0.5
  FillSpaces = false
  FontSize = 12
  JoinArch = false
  LineWidth = 0.25
  LockPosition = false
  RenderMode = 0
  Rotation = 0
  Scale = 0.02
  ScaleType = 2
  ShowFill = true
  ShowHidden = false
  Source = -> Section001
  Symbol = <blob: 30238 chars omitted>
  X = 418.877
  Y = 655.022
FEATURE [TechDraw::DrawPage] Page005  label="_Planta Fundaciones"
  KeepUpdated = true
  NextBalloonIndex = 1
  ProjectionType = 0
  Template = -> Template005
  Views = -> [ArchView001]
FEATURE [App::DocumentObjectGroup] Group002  label="Vistas ARCH"
  Group = -> [Page004,Section001,Section,Page005]
FEATURE [App::FeaturePython] Section002  label="AUX-Planta ARQ"  # WARN: FeaturePython — macro-defined, semantics opaque (R4)
  Clip = false
  Objects = -> [BuildingPart]
  OnlySolids = false
  Placement = pos=(15000,5000,1200) rot=(0,0,1;0rad)
  UseMaterialColorForFill = false
